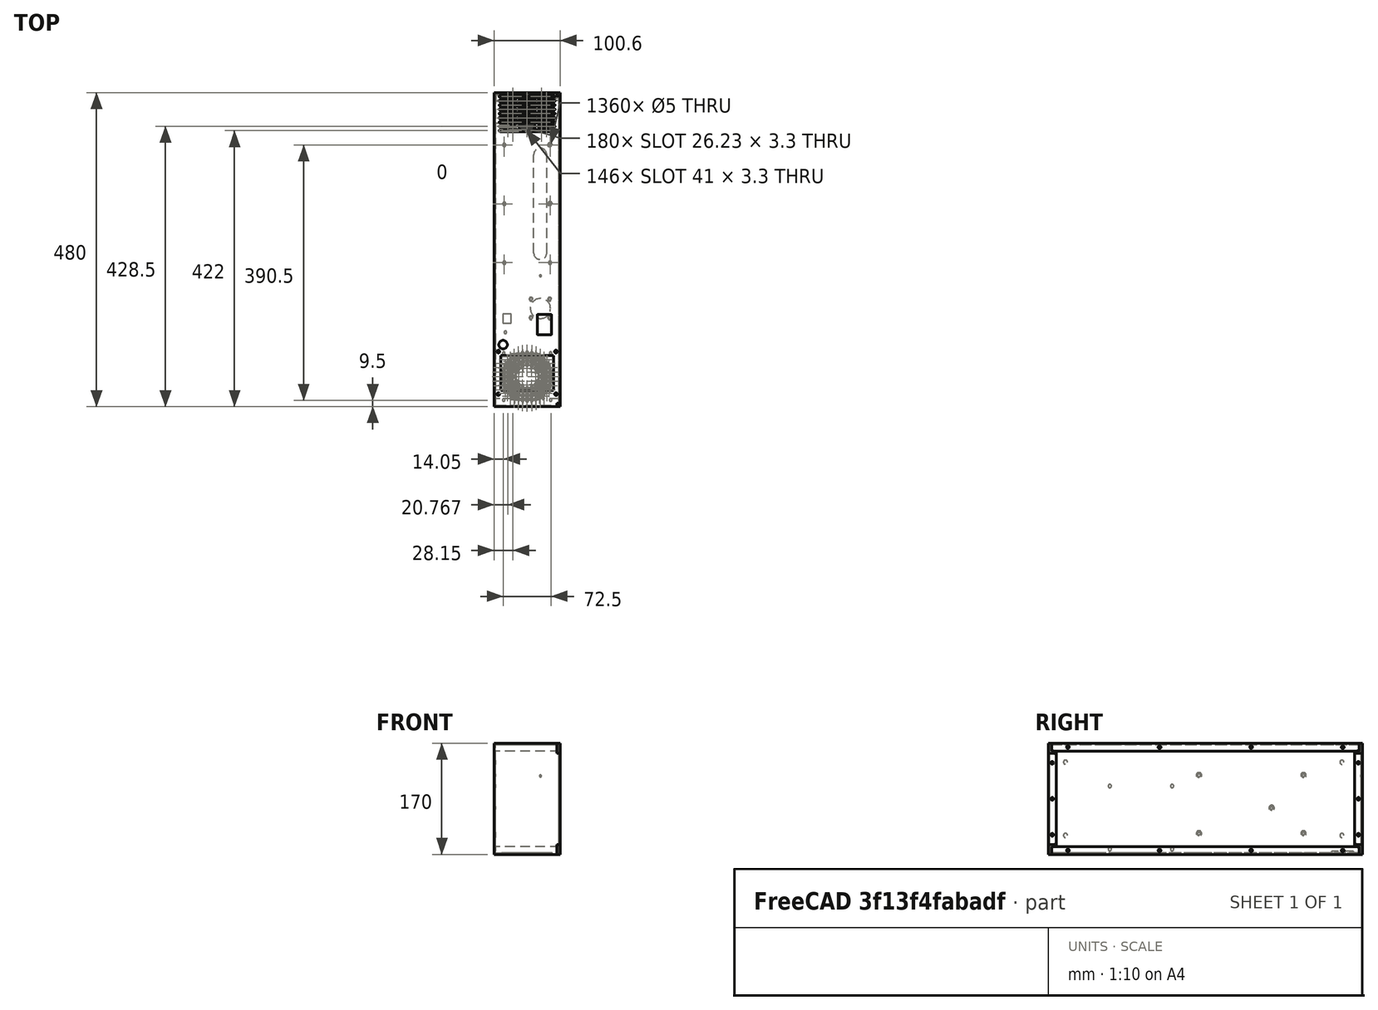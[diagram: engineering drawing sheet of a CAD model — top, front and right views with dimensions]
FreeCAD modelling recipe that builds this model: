
FCSTD DOCUMENT  (FreeCAD 0.17R13123 (Git))
Label: electronics_chassis_PP-FP0142_RevA
License: All rights reserved
LicenseURL: http://en.wikipedia.org/wiki/All_rights_reserved
objects: Drawing::FeatureView×251, Drawing::FeatureViewPython×31, Sketcher::SketchObject×21, PartDesign::Pocket×19, Drawing::FeatureViewPart×15, Drawing::FeaturePage×8, Drawing::FeatureViewSymbol×7, PartDesign::Fillet×4, PartDesign::Pad×2, PartDesign::Chamfer×2, Part::Feature×1
note: 70 computed .brp shape members not serialized (recipe doc carries the construction recipe); baked Part::Feature solids carry a one-line shape summary decoded from their .brp

FEATURE [Sketcher::SketchObject] Sketch
  MapMode = 5
  sketch-geometry (4):
    g0: LineSegment StartX=0 StartY=0 StartZ=0 EndX=-100.6 EndY=0 EndZ=0
    g1: LineSegment StartX=-100.6 StartY=0 StartZ=0 EndX=-100.6 EndY=480 EndZ=0
    g2: LineSegment StartX=-100.6 StartY=480 StartZ=0 EndX=0 EndY=480 EndZ=0
    g3: LineSegment StartX=0 StartY=480 StartZ=0 EndX=0 EndY=0 EndZ=0
  constraints (11):
    c: Coincident(g0,g1)
    c: Coincident(g1,g2)
    c: Coincident(g2,g3)
    c: Coincident(g3,g0)
    c: Horizontal(g0)
    c: Horizontal(g2)
    c: Vertical(g1)
    c: Vertical(g3)
    c: Coincident(g0,g-1)
    c: DistanceX(g0) = -100.6
    c: DistanceY(g3) = -480
FEATURE [PartDesign::Pad] Pad
  Length = 170
  Length2 = 100
  Profile = -> Sketch
  Type = 0
FEATURE [Sketcher::SketchObject] Sketch001
  ExternalGeometry = -> [Pad]
  MapMode = 5
  Placement = pos=(0,0,0) rot=(0.57735,0.57735,0.57735;2.0944rad)
  Support = -> [Pad]
  sketch-geometry (4):
    g0: LineSegment StartX=12 StartY=12 StartZ=0 EndX=468 EndY=12 EndZ=0
    g1: LineSegment StartX=468 StartY=12 StartZ=0 EndX=468 EndY=158 EndZ=0
    g2: LineSegment StartX=468 StartY=158 StartZ=0 EndX=12 EndY=158 EndZ=0
    g3: LineSegment StartX=12 StartY=158 StartZ=0 EndX=12 EndY=12 EndZ=0
  constraints (12):
    c: Coincident(g0,g1)
    c: Coincident(g0,g3)
    c: Coincident(g1,g2)
    c: Coincident(g2,g3)
    c: Horizontal(g0)
    c: Horizontal(g2)
    c: Vertical(g3)
    c: Vertical(g1)
    c: DistanceY(g-1,g0) = 12
    c: DistanceX(g-1,g0) = 12
    c: DistanceX(g0,g-5) = 12
    c: DistanceY(g-4,g2) = -12
FEATURE [PartDesign::Pocket] Pocket
  Length = 98.56
  Profile = -> Sketch001
  Type = 0
FEATURE [Sketcher::SketchObject] Sketch031
  ExternalGeometry = -> [Pocket]
  MapMode = 5
  Placement = pos=(-98.56,0,0) rot=(0.57735,0.57735,0.57735;2.0944rad)
  Support = -> [Pocket]
  sketch-geometry (4):
    g0: LineSegment StartX=2.03 StartY=167.97 StartZ=0 EndX=477.97 EndY=167.97 EndZ=0
    g1: LineSegment StartX=477.97 StartY=167.97 StartZ=0 EndX=477.97 EndY=2.03 EndZ=0
    g2: LineSegment StartX=477.97 StartY=2.03 StartZ=0 EndX=2.03 EndY=2.03 EndZ=0
    g3: LineSegment StartX=2.03 StartY=2.03 StartZ=0 EndX=2.03 EndY=167.97 EndZ=0
  constraints (12):
    c: Coincident(g0,g1)
    c: Coincident(g1,g2)
    c: Coincident(g2,g3)
    c: Coincident(g3,g0)
    c: Horizontal(g0)
    c: Horizontal(g2)
    c: Vertical(g1)
    c: Vertical(g3)
    c: DistanceX(g-1,g2) = 2.03
    c: DistanceY(g-1,g2) = 2.03
    c: DistanceY(g0,g-4) = 2.03
    c: DistanceX(g0,g-4) = 2.03
FEATURE [PartDesign::Pocket] Pocket001
  Length = 96.54
  Profile = -> Sketch031
  Reversed = true
  Type = 0
FEATURE [Sketcher::SketchObject] Sketch032
  ExternalGeometry = -> [Pocket001]
  MapMode = 5
  Placement = pos=(0,0,0) rot=(0.57735,0.57735,0.57735;2.0944rad)
  Support = -> [Pocket001]
  sketch-geometry (24):
    g0: LineSegment StartX=12 StartY=158 StartZ=0 EndX=5 EndY=158 EndZ=0
    g1: LineSegment StartX=5 StartY=158 StartZ=0 EndX=5 EndY=170 EndZ=0
    g2: LineSegment StartX=5 StartY=170 StartZ=0 EndX=0 EndY=170 EndZ=0
    g3: LineSegment StartX=0 StartY=170 StartZ=0 EndX=0 EndY=155 EndZ=0
    g4: LineSegment StartX=0 StartY=155 StartZ=0 EndX=12 EndY=155 EndZ=0
    g5: LineSegment StartX=12 StartY=155 StartZ=0 EndX=12 EndY=158 EndZ=0
    g6: LineSegment StartX=0 StartY=0 StartZ=0 EndX=0 EndY=15 EndZ=0
    g7: LineSegment StartX=0 StartY=15 StartZ=0 EndX=12 EndY=15 EndZ=0
    g8: LineSegment StartX=12 StartY=15 StartZ=0 EndX=12 EndY=12 EndZ=0
    g9: LineSegment StartX=12 StartY=12 StartZ=0 EndX=5 EndY=12 EndZ=0
    g10: LineSegment StartX=5 StartY=12 StartZ=0 EndX=5 EndY=0 EndZ=0
    g11: LineSegment StartX=5 StartY=0 StartZ=0 EndX=0 EndY=0 EndZ=0
    g12: LineSegment StartX=480 StartY=0 StartZ=0 EndX=480 EndY=15 EndZ=0
    g13: LineSegment StartX=480 StartY=15 StartZ=0 EndX=468 EndY=15 EndZ=0
    g14: LineSegment StartX=468 StartY=15 StartZ=0 EndX=468 EndY=12 EndZ=0
    g15: LineSegment StartX=468 StartY=12 StartZ=0 EndX=475 EndY=12 EndZ=0
    g16: LineSegment StartX=475 StartY=12 StartZ=0 EndX=475 EndY=0 EndZ=0
    g17: LineSegment StartX=480 StartY=0 StartZ=0 EndX=475 EndY=0 EndZ=0
    g18: LineSegment StartX=475 StartY=170 StartZ=0 EndX=480 EndY=170 EndZ=0
    g19: LineSegment StartX=480 StartY=170 StartZ=0 EndX=480 EndY=155 EndZ=0
    g20: LineSegment StartX=480 StartY=155 StartZ=0 EndX=468 EndY=155 EndZ=0
    g21: LineSegment StartX=468 StartY=155 StartZ=0 EndX=468 EndY=158 EndZ=0
    g22: LineSegment StartX=468 StartY=158 StartZ=0 EndX=475 EndY=158 EndZ=0
    g23: LineSegment StartX=475 StartY=158 StartZ=0 EndX=475 EndY=170 EndZ=0
  constraints (67):
    c: Coincident(g0,g1)
    c: Coincident(g1,g2)
    c: Coincident(g2,g3)
    c: Coincident(g3,g4)
    c: Coincident(g4,g5)
    c: Coincident(g6,g7)
    c: Coincident(g8,g9)
    c: Coincident(g9,g10)
    c: Coincident(g10,g11)
    c: Coincident(g12,g13)
    c: Coincident(g13,g14)
    c: Coincident(g14,g15)
    c: Coincident(g15,g16)
    c: Coincident(g18,g19)
    c: Coincident(g19,g20)
    c: Coincident(g20,g21)
    c: Coincident(g21,g22)
    c: Coincident(g22,g23)
    c: Vertical(g10)
    c: Vertical(g6)
    c: Vertical(g8)
    c: Horizontal(g7)
    c: Horizontal(g9)
    c: Horizontal(g11)
    c: Coincident(g6,g11)
    c: Distance(g6) = 15
    c: DistanceX(g11) = -5
    c: Coincident(g6,g-1)
    c: PointOnObject(g8,g-8)
    c: Coincident(g7,g8)
    c: Coincident(g8,g-8)
    c: Vertical(g3)
    c: Vertical(g1)
    c: Vertical(g5)
    c: Horizontal(g2)
    c: Horizontal(g0)
    c: Horizontal(g4)
    c: Coincident(g2,g-4)
    c: DistanceX(g1,g2) = -5
    c: DistanceY(g3,g2) = 15
    c: Coincident(g0,g5)
    c: PointOnObject(g0,g-5)
    c: Coincident(g0,g-6)
    c: Vertical(g23)
    c: Vertical(g21)
    c: Vertical(g19)
    c: Horizontal(g18)
    c: Horizontal(g22)
    c: Horizontal(g20)
    c: Coincident(g18,g23)
    c: DistanceY(g19) = -15
    c: DistanceX(g18) = 5
    c: Coincident(g18,g-10)
    c: Coincident(g21,g-9)
    c: Coincident(g12,g17)
    c: Horizontal(g13)
    c: Horizontal(g15)
    c: Horizontal(g17)
    c: Vertical(g14)
    c: Vertical(g16)
    c: Vertical(g12)
    c: Coincident(g16,g17)
    c: DistanceY(g12) = 15
    c: Coincident(g-10,g12)
    c: DistanceX(g16,g12) = 5
    c: PointOnObject(g-9,g15)
    c: Coincident(g14,g-9)
FEATURE [PartDesign::Pocket] Pocket002
  Length = 5
  Profile = -> Sketch032
  Type = 0
FEATURE [Sketcher::SketchObject] Sketch004  label="lcd"
  ExternalGeometry = -> [Pocket]
  MapMode = 5
  Placement = pos=(0,0,170) rot=(0,0,1;0rad)
  Support = -> [Pocket002]
  sketch-geometry (13):
    g0: LineSegment StartX=-90.6 StartY=25 StartZ=0 EndX=-10 EndY=25 EndZ=0
    g1: LineSegment StartX=-10 StartY=25 StartZ=0 EndX=-10 EndY=78.1 EndZ=0
    g2: LineSegment StartX=-10 StartY=78.1 StartZ=0 EndX=-90.6 EndY=78.1 EndZ=0
    g3: LineSegment StartX=-90.6 StartY=78.1 StartZ=0 EndX=-90.6 EndY=25 EndZ=0
    g4: Circle CenterX=-87.1 CenterY=94.75 CenterZ=0 NormalX=0 NormalY=0 NormalZ=1 AngleXU=0 Radius=6.5
    g5: LineSegment [constr] StartX=-94.3 StartY=84.05 StartZ=0 EndX=-6.3 EndY=84.05 EndZ=0
    g6: LineSegment [constr] StartX=-6.3 StartY=84.05 StartZ=0 EndX=-6.3 EndY=19.05 EndZ=0
    g7: LineSegment [constr] StartX=-6.3 StartY=19.05 StartZ=0 EndX=-94.3 EndY=19.05 EndZ=0
    g8: LineSegment [constr] StartX=-94.3 StartY=19.05 StartZ=0 EndX=-94.3 EndY=84.05 EndZ=0
    g9: Circle CenterX=-6.3 CenterY=84.05 CenterZ=0 NormalX=0 NormalY=0 NormalZ=1 AngleXU=0 Radius=2.11
    g10: Circle CenterX=-6.3 CenterY=19.05 CenterZ=0 NormalX=0 NormalY=0 NormalZ=1 AngleXU=0 Radius=2.11
    g11: Circle CenterX=-94.3 CenterY=19.05 CenterZ=0 NormalX=0 NormalY=0 NormalZ=1 AngleXU=0 Radius=2.11
    g12: Circle CenterX=-94.3 CenterY=84.05 CenterZ=0 NormalX=0 NormalY=0 NormalZ=1 AngleXU=0 Radius=2.11
  constraints (35):
    c: Coincident(g0,g1)
    c: Coincident(g0,g3)
    c: Coincident(g1,g2)
    c: Coincident(g2,g3)
    c: DistanceX(g-1,g1) = -10
    c: Distance(g0) = 80.6
    c: Vertical(g1)
    c: Vertical(g3)
    c: Horizontal(g0)
    c: Horizontal(g2)
    c: Distance(g3) = 53.1
    c: DistanceY(g2,g4) = 16.65
    c: Radius(g4) = 6.5
    c: DistanceY(g-1,g0) = 25
    c: DistanceX(g2,g4) = 3.5
    c: Coincident(g5,g6)
    c: Coincident(g6,g7)
    c: Coincident(g7,g8)
    c: Coincident(g8,g5)
    c: Horizontal(g5)
    c: Horizontal(g7)
    c: Vertical(g6)
    c: Vertical(g8)
    c: DistanceY(g8) = 65
    c: DistanceX(g7) = -88
    c: DistanceX(g6,g0) = -3.7
    c: DistanceY(g0,g6) = -5.95
    c: Coincident(g5,g9)
    c: Coincident(g6,g10)
    c: Coincident(g5,g12)
    c: Coincident(g7,g11)
    c: Radius(g9) = 2.11
    c: Equal(g9,g10)
    c: Equal(g10,g11)
    c: Equal(g11,g12)
FEATURE [PartDesign::Pocket] Pocket003  label="lcd-panel"
  Length = 5
  Profile = -> Sketch004
  Type = 0
FEATURE [Sketcher::SketchObject] Sketch015  label="intake"
  MapMode = 5
  Placement = pos=(0,0,170) rot=(0,0,1;0rad)
  Support = -> [Pocket003]
  sketch-geometry (99):
    g0: LineSegment [constr] StartX=-91.3 StartY=474 StartZ=0 EndX=-9.3 EndY=474 EndZ=0
    g1: LineSegment [constr] StartX=-9.3 StartY=474 StartZ=0 EndX=-9.3 EndY=422 EndZ=0
    g2: LineSegment [constr] StartX=-9.3 StartY=422 StartZ=0 EndX=-91.3 EndY=422 EndZ=0
    g3: LineSegment [constr] StartX=-91.3 StartY=422 StartZ=0 EndX=-91.3 EndY=474 EndZ=0
    g4: ArcOfCircle CenterX=-9.3 CenterY=422 CenterZ=0 NormalX=0 NormalY=0 NormalZ=1 AngleXU=0 Radius=1.65 StartAngle=4.71239 EndAngle=7.85398
    g5: ArcOfCircle CenterX=-47 CenterY=422 CenterZ=0 NormalX=0 NormalY=0 NormalZ=1 AngleXU=0 Radius=1.65 StartAngle=1.5708 EndAngle=4.71239
    g6: LineSegment StartX=-9.3 StartY=423.65 StartZ=0 EndX=-47 EndY=423.65 EndZ=0
    g7: LineSegment StartX=-9.3 StartY=420.35 StartZ=0 EndX=-47 EndY=420.35 EndZ=0
    g8: ArcOfCircle CenterX=-91.3 CenterY=422 CenterZ=0 NormalX=0 NormalY=0 NormalZ=1 AngleXU=0 Radius=1.65 StartAngle=1.5708 EndAngle=4.71239
    g9: ArcOfCircle CenterX=-53.6 CenterY=422 CenterZ=0 NormalX=0 NormalY=0 NormalZ=1 AngleXU=0 Radius=1.65 StartAngle=4.71239 EndAngle=7.85398
    g10: LineSegment StartX=-91.3 StartY=420.35 StartZ=0 EndX=-53.6 EndY=420.35 EndZ=0
    g11: LineSegment StartX=-91.3 StartY=423.65 StartZ=0 EndX=-53.6 EndY=423.65 EndZ=0
    g12: ArcOfCircle CenterX=-91.3 CenterY=428.5 CenterZ=0 NormalX=0 NormalY=0 NormalZ=1 AngleXU=0 Radius=1.65 StartAngle=1.5708 EndAngle=4.71239
    g13: ArcOfCircle CenterX=-68.3667 CenterY=428.5 CenterZ=0 NormalX=0 NormalY=0 NormalZ=1 AngleXU=0 Radius=1.65 StartAngle=4.71239 EndAngle=7.85398
    g14: LineSegment StartX=-91.3 StartY=426.85 StartZ=0 EndX=-68.3667 EndY=426.85 EndZ=0
    g15: LineSegment StartX=-91.3 StartY=430.15 StartZ=0 EndX=-68.3667 EndY=430.15 EndZ=0
    g16: ArcOfCircle CenterX=-61.7667 CenterY=428.5 CenterZ=0 NormalX=0 NormalY=0 NormalZ=1 AngleXU=0 Radius=1.65 StartAngle=1.5708 EndAngle=4.71239
    g17: ArcOfCircle CenterX=-38.8333 CenterY=428.5 CenterZ=0 NormalX=0 NormalY=0 NormalZ=1 AngleXU=0 Radius=1.65 StartAngle=4.71239 EndAngle=7.85398
    g18: LineSegment StartX=-61.7667 StartY=426.85 StartZ=0 EndX=-38.8333 EndY=426.85 EndZ=0
    g19: LineSegment StartX=-61.7667 StartY=430.15 StartZ=0 EndX=-38.8333 EndY=430.15 EndZ=0
    g20: ArcOfCircle CenterX=-32.2333 CenterY=428.5 CenterZ=0 NormalX=0 NormalY=0 NormalZ=1 AngleXU=0 Radius=1.65 StartAngle=1.5708 EndAngle=4.71239
    g21: ArcOfCircle CenterX=-9.3 CenterY=428.5 CenterZ=0 NormalX=0 NormalY=0 NormalZ=1 AngleXU=0 Radius=1.65 StartAngle=4.71239 EndAngle=7.85398
    g22: LineSegment StartX=-32.2333 StartY=426.85 StartZ=0 EndX=-9.3 EndY=426.85 EndZ=0
    g23: LineSegment StartX=-32.2333 StartY=430.15 StartZ=0 EndX=-9.3 EndY=430.15 EndZ=0
    g24: ArcOfCircle CenterX=-91.3 CenterY=435 CenterZ=0 NormalX=0 NormalY=0 NormalZ=1 AngleXU=0 Radius=1.65 StartAngle=1.5708 EndAngle=4.71239
    g25: ArcOfCircle CenterX=-53.6 CenterY=435 CenterZ=0 NormalX=0 NormalY=0 NormalZ=1 AngleXU=0 Radius=1.65 StartAngle=4.71239 EndAngle=7.85398
    g26: LineSegment StartX=-91.3 StartY=433.35 StartZ=0 EndX=-53.6 EndY=433.35 EndZ=0
    g27: LineSegment StartX=-91.3 StartY=436.65 StartZ=0 EndX=-53.6 EndY=436.65 EndZ=0
    g28: ArcOfCircle CenterX=-47 CenterY=435 CenterZ=0 NormalX=0 NormalY=0 NormalZ=1 AngleXU=0 Radius=1.65 StartAngle=1.5708 EndAngle=4.71239
    g29: ArcOfCircle CenterX=-9.3 CenterY=435 CenterZ=0 NormalX=0 NormalY=0 NormalZ=1 AngleXU=0 Radius=1.65 StartAngle=4.71239 EndAngle=7.85398
    g30: LineSegment StartX=-47 StartY=433.35 StartZ=0 EndX=-9.3 EndY=433.35 EndZ=0
    g31: LineSegment StartX=-47 StartY=436.65 StartZ=0 EndX=-9.3 EndY=436.65 EndZ=0
    g32: ArcOfCircle CenterX=-91.3 CenterY=441.5 CenterZ=0 NormalX=0 NormalY=0 NormalZ=1 AngleXU=0 Radius=1.65 StartAngle=1.5708 EndAngle=4.71239
    g33: ArcOfCircle CenterX=-68.3667 CenterY=441.5 CenterZ=0 NormalX=0 NormalY=0 NormalZ=1 AngleXU=0 Radius=1.65 StartAngle=4.71239 EndAngle=7.85398
    g34: LineSegment StartX=-91.3 StartY=439.85 StartZ=0 EndX=-68.3667 EndY=439.85 EndZ=0
    g35: LineSegment StartX=-91.3 StartY=443.15 StartZ=0 EndX=-68.3667 EndY=443.15 EndZ=0
    g36: ArcOfCircle CenterX=-61.7667 CenterY=441.5 CenterZ=0 NormalX=0 NormalY=0 NormalZ=1 AngleXU=0 Radius=1.65 StartAngle=1.5708 EndAngle=4.71239
    g37: ArcOfCircle CenterX=-38.8333 CenterY=441.5 CenterZ=0 NormalX=0 NormalY=0 NormalZ=1 AngleXU=0 Radius=1.65 StartAngle=4.71239 EndAngle=7.85398
    g38: LineSegment StartX=-61.7667 StartY=439.85 StartZ=0 EndX=-38.8333 EndY=439.85 EndZ=0
    g39: LineSegment StartX=-61.7667 StartY=443.15 StartZ=0 EndX=-38.8333 EndY=443.15 EndZ=0
    g40: ArcOfCircle CenterX=-32.2333 CenterY=441.5 CenterZ=0 NormalX=0 NormalY=0 NormalZ=1 AngleXU=0 Radius=1.65 StartAngle=1.5708 EndAngle=4.71239
    g41: ArcOfCircle CenterX=-9.3 CenterY=441.5 CenterZ=0 NormalX=0 NormalY=0 NormalZ=1 AngleXU=0 Radius=1.65 StartAngle=4.71239 EndAngle=7.85398
    g42: LineSegment StartX=-32.2333 StartY=439.85 StartZ=0 EndX=-9.3 EndY=439.85 EndZ=0
    g43: LineSegment StartX=-32.2333 StartY=443.15 StartZ=0 EndX=-9.3 EndY=443.15 EndZ=0
    g44: ArcOfCircle CenterX=-91.3 CenterY=448 CenterZ=0 NormalX=0 NormalY=0 NormalZ=1 AngleXU=0 Radius=1.65 StartAngle=1.5708 EndAngle=4.71239
    g45: ArcOfCircle CenterX=-53.6 CenterY=448 CenterZ=0 NormalX=0 NormalY=0 NormalZ=1 AngleXU=0 Radius=1.65 StartAngle=4.71239 EndAngle=7.85398
    g46: LineSegment StartX=-91.3 StartY=446.35 StartZ=0 EndX=-53.6 EndY=446.35 EndZ=0
    g47: LineSegment StartX=-91.3 StartY=449.65 StartZ=0 EndX=-53.6 EndY=449.65 EndZ=0
    g48: ArcOfCircle CenterX=-47 CenterY=448 CenterZ=0 NormalX=0 NormalY=0 NormalZ=1 AngleXU=0 Radius=1.65 StartAngle=1.5708 EndAngle=4.71239
    g49: ArcOfCircle CenterX=-9.3 CenterY=448 CenterZ=0 NormalX=0 NormalY=0 NormalZ=1 AngleXU=0 Radius=1.65 StartAngle=4.71239 EndAngle=7.85398
    g50: LineSegment StartX=-47 StartY=446.35 StartZ=0 EndX=-9.3 EndY=446.35 EndZ=0
    g51: LineSegment StartX=-47 StartY=449.65 StartZ=0 EndX=-9.3 EndY=449.65 EndZ=0
    g52: ArcOfCircle CenterX=-91.3 CenterY=454.5 CenterZ=0 NormalX=0 NormalY=0 NormalZ=1 AngleXU=0 Radius=1.65 StartAngle=1.5708 EndAngle=4.71239
    g53: ArcOfCircle CenterX=-68.3667 CenterY=454.5 CenterZ=0 NormalX=0 NormalY=0 NormalZ=1 AngleXU=0 Radius=1.65 StartAngle=4.71239 EndAngle=7.85398
    g54: LineSegment StartX=-91.3 StartY=452.85 StartZ=0 EndX=-68.3667 EndY=452.85 EndZ=0
    g55: LineSegment StartX=-91.3 StartY=456.15 StartZ=0 EndX=-68.3667 EndY=456.15 EndZ=0
    g56: ArcOfCircle CenterX=-61.7667 CenterY=454.5 CenterZ=0 NormalX=0 NormalY=0 NormalZ=1 AngleXU=0 Radius=1.65 StartAngle=1.5708 EndAngle=4.71239
    g57: ArcOfCircle CenterX=-38.8333 CenterY=454.5 CenterZ=0 NormalX=0 NormalY=0 NormalZ=1 AngleXU=0 Radius=1.65 StartAngle=4.71239 EndAngle=7.85398
    g58: LineSegment StartX=-61.7667 StartY=452.85 StartZ=0 EndX=-38.8333 EndY=452.85 EndZ=0
    g59: LineSegment StartX=-61.7667 StartY=456.15 StartZ=0 EndX=-38.8333 EndY=456.15 EndZ=0
    g60: ArcOfCircle CenterX=-32.2333 CenterY=454.5 CenterZ=0 NormalX=0 NormalY=0 NormalZ=1 AngleXU=0 Radius=1.65 StartAngle=1.5708 EndAngle=4.71239
    g61: ArcOfCircle CenterX=-9.3 CenterY=454.5 CenterZ=0 NormalX=0 NormalY=0 NormalZ=1 AngleXU=0 Radius=1.65 StartAngle=4.71239 EndAngle=7.85398
    g62: LineSegment StartX=-32.2333 StartY=452.85 StartZ=0 EndX=-9.3 EndY=452.85 EndZ=0
    g63: LineSegment StartX=-32.2333 StartY=456.15 StartZ=0 EndX=-9.3 EndY=456.15 EndZ=0
    g64: ArcOfCircle CenterX=-91.3 CenterY=461 CenterZ=0 NormalX=0 NormalY=0 NormalZ=1 AngleXU=0 Radius=1.65 StartAngle=1.5708 EndAngle=4.71239
    g65: ArcOfCircle CenterX=-53.6 CenterY=461 CenterZ=0 NormalX=0 NormalY=0 NormalZ=1 AngleXU=0 Radius=1.65 StartAngle=4.71239 EndAngle=7.85398
    g66: LineSegment StartX=-91.3 StartY=459.35 StartZ=0 EndX=-53.6 EndY=459.35 EndZ=0
    g67: LineSegment StartX=-91.3 StartY=462.65 StartZ=0 EndX=-53.6 EndY=462.65 EndZ=0
    g68: ArcOfCircle CenterX=-47 CenterY=461 CenterZ=0 NormalX=0 NormalY=0 NormalZ=1 AngleXU=0 Radius=1.65 StartAngle=1.5708 EndAngle=4.71239
    g69: ArcOfCircle CenterX=-9.3 CenterY=461 CenterZ=0 NormalX=0 NormalY=0 NormalZ=1 AngleXU=0 Radius=1.65 StartAngle=4.71239 EndAngle=7.85398
    g70: LineSegment StartX=-47 StartY=459.35 StartZ=0 EndX=-9.3 EndY=459.35 EndZ=0
    g71: LineSegment StartX=-47 StartY=462.65 StartZ=0 EndX=-9.3 EndY=462.65 EndZ=0
    g72: ArcOfCircle CenterX=-91.3 CenterY=467.5 CenterZ=0 NormalX=0 NormalY=0 NormalZ=1 AngleXU=0 Radius=1.65 StartAngle=1.5708 EndAngle=4.71239
    g73: ArcOfCircle CenterX=-68.3667 CenterY=467.5 CenterZ=0 NormalX=0 NormalY=0 NormalZ=1 AngleXU=0 Radius=1.65 StartAngle=4.71239 EndAngle=7.85398
    g74: LineSegment StartX=-91.3 StartY=465.85 StartZ=0 EndX=-68.3667 EndY=465.85 EndZ=0
    g75: LineSegment StartX=-91.3 StartY=469.15 StartZ=0 EndX=-68.3667 EndY=469.15 EndZ=0
    g76: ArcOfCircle CenterX=-61.7667 CenterY=467.5 CenterZ=0 NormalX=0 NormalY=0 NormalZ=1 AngleXU=0 Radius=1.65 StartAngle=1.5708 EndAngle=4.71239
    g77: ArcOfCircle CenterX=-38.8333 CenterY=467.5 CenterZ=0 NormalX=0 NormalY=0 NormalZ=1 AngleXU=0 Radius=1.65 StartAngle=4.71239 EndAngle=7.85398
    g78: LineSegment StartX=-61.7667 StartY=465.85 StartZ=0 EndX=-38.8333 EndY=465.85 EndZ=0
    g79: LineSegment StartX=-61.7667 StartY=469.15 StartZ=0 EndX=-38.8333 EndY=469.15 EndZ=0
    g80: ArcOfCircle CenterX=-32.2333 CenterY=467.5 CenterZ=0 NormalX=0 NormalY=0 NormalZ=1 AngleXU=0 Radius=1.65 StartAngle=1.5708 EndAngle=4.71239
    g81: ArcOfCircle CenterX=-9.3 CenterY=467.5 CenterZ=0 NormalX=0 NormalY=0 NormalZ=1 AngleXU=0 Radius=1.65 StartAngle=4.71239 EndAngle=7.85398
    g82: LineSegment StartX=-32.2333 StartY=465.85 StartZ=0 EndX=-9.3 EndY=465.85 EndZ=0
    g83: LineSegment StartX=-32.2333 StartY=469.15 StartZ=0 EndX=-9.3 EndY=469.15 EndZ=0
    g84: ArcOfCircle CenterX=-91.3 CenterY=474 CenterZ=0 NormalX=0 NormalY=0 NormalZ=1 AngleXU=0 Radius=1.65 StartAngle=1.5708 EndAngle=4.71239
    g85: ArcOfCircle CenterX=-53.6 CenterY=474 CenterZ=0 NormalX=0 NormalY=0 NormalZ=1 AngleXU=0 Radius=1.65 StartAngle=4.71239 EndAngle=7.85398
    g86: LineSegment StartX=-91.3 StartY=472.35 StartZ=0 EndX=-53.6 EndY=472.35 EndZ=0
    g87: LineSegment StartX=-91.3 StartY=475.65 StartZ=0 EndX=-53.6 EndY=475.65 EndZ=0
    g88: LineSegment [constr] StartX=-91.3 StartY=435 StartZ=0 EndX=-9.3 EndY=435 EndZ=0
    g89: LineSegment [constr] StartX=-9.3 StartY=448 StartZ=0 EndX=-91.3 EndY=448 EndZ=0
    g90: LineSegment [constr] StartX=-91.3 StartY=441.5 StartZ=0 EndX=-9.3 EndY=441.5 EndZ=0
    g91: LineSegment [constr] StartX=-91.3 StartY=428.5 StartZ=0 EndX=-9.3 EndY=428.5 EndZ=0
    g92: LineSegment [constr] StartX=-91.3 StartY=454.5 StartZ=0 EndX=-9.3 EndY=454.5 EndZ=0
    g93: LineSegment [constr] StartX=-91.3 StartY=461 StartZ=0 EndX=-9.3 EndY=461 EndZ=0
    g94: LineSegment [constr] StartX=-91.3 StartY=467.5 StartZ=0 EndX=-9.3 EndY=467.5 EndZ=0
    g95: ArcOfCircle CenterX=-47 CenterY=474 CenterZ=0 NormalX=0 NormalY=0 NormalZ=1 AngleXU=0 Radius=1.65 StartAngle=1.5708 EndAngle=4.71239
    g96: ArcOfCircle CenterX=-9.3 CenterY=474 CenterZ=0 NormalX=0 NormalY=0 NormalZ=1 AngleXU=0 Radius=1.65 StartAngle=4.71239 EndAngle=7.85398
    g97: LineSegment StartX=-47 StartY=472.35 StartZ=0 EndX=-9.3 EndY=472.35 EndZ=0
    g98: LineSegment StartX=-47 StartY=475.65 StartZ=0 EndX=-9.3 EndY=475.65 EndZ=0
  constraints (243):
    c: Coincident(g1,g2)
    c: Coincident(g2,g3)
    c: Coincident(g3,g0)
    c: Horizontal(g0)
    c: Horizontal(g2)
    c: Vertical(g1)
    c: Vertical(g3)
    c: DistanceX(g2) = -82
    c: DistanceX(g-1,g1) = -9.3
    c: Tangent(g4,g7) = 1.5708
    c: Tangent(g4,g6) = -1.5708
    c: Tangent(g6,g5) = -1.5708
    c: Tangent(g7,g5) = 1.5708
    c: Horizontal(g6)
    c: Equal(g4,g5)
    c: Tangent(g8,g11) = 1.5708
    c: Tangent(g8,g10) = -1.5708
    c: Tangent(g10,g9) = -1.5708
    c: Tangent(g11,g9) = 1.5708
    c: Horizontal(g10)
    c: Equal(g8,g9)
    c: Tangent(g12,g15) = 1.5708
    c: Tangent(g12,g14) = -1.5708
    c: Tangent(g14,g13) = -1.5708
    c: Tangent(g15,g13) = 1.5708
    c: Horizontal(g14)
    c: Equal(g12,g13)
    c: Tangent(g16,g19) = 1.5708
    c: Tangent(g16,g18) = -1.5708
    c: Tangent(g18,g17) = -1.5708
    c: Tangent(g19,g17) = 1.5708
    c: Horizontal(g18)
    c: Equal(g16,g17)
    c: Tangent(g20,g23) = 1.5708
    c: Tangent(g20,g22) = -1.5708
    c: Tangent(g22,g21) = -1.5708
    c: Tangent(g23,g21) = 1.5708
    c: Horizontal(g22)
    c: Equal(g20,g21)
    c: Tangent(g24,g27) = 1.5708
    c: Tangent(g24,g26) = -1.5708
    c: Tangent(g26,g25) = -1.5708
    c: Tangent(g27,g25) = 1.5708
    c: Horizontal(g26)
    c: Equal(g24,g25)
    c: Tangent(g28,g31) = 1.5708
    c: Tangent(g28,g30) = -1.5708
    c: Tangent(g30,g29) = -1.5708
    c: Tangent(g31,g29) = 1.5708
    c: Horizontal(g30)
    c: Equal(g28,g29)
    c: Tangent(g32,g35) = 1.5708
    c: Tangent(g32,g34) = -1.5708
    c: Tangent(g34,g33) = -1.5708
    c: Tangent(g35,g33) = 1.5708
    c: Horizontal(g34)
    c: Equal(g32,g33)
    c: Tangent(g36,g39) = 1.5708
    c: Tangent(g36,g38) = -1.5708
    c: Tangent(g38,g37) = -1.5708
    c: Tangent(g39,g37) = 1.5708
    c: Horizontal(g38)
    c: Equal(g36,g37)
    c: Tangent(g40,g43) = 1.5708
    c: Tangent(g40,g42) = -1.5708
    c: Tangent(g42,g41) = -1.5708
    c: Tangent(g43,g41) = 1.5708
    c: Horizontal(g42)
    c: Equal(g40,g41)
    c: Tangent(g44,g47) = 1.5708
    c: Tangent(g44,g46) = -1.5708
    c: Tangent(g46,g45) = -1.5708
    c: Tangent(g47,g45) = 1.5708
    c: Horizontal(g46)
    c: Equal(g44,g45)
    c: Tangent(g48,g51) = 1.5708
    c: Tangent(g48,g50) = -1.5708
    c: Tangent(g50,g49) = -1.5708
    c: Tangent(g51,g49) = 1.5708
    c: Horizontal(g50)
    c: Equal(g48,g49)
    c: Coincident(g1,g4)
    c: Radius(g4) = 1.65
    c: Coincident(g2,g8)
    c: DistanceX(g5,g9) = -6.6
    c: Tangent(g52,g55) = 1.5708
    c: Tangent(g52,g54) = -1.5708
    c: Tangent(g54,g53) = -1.5708
    c: Tangent(g55,g53) = 1.5708
    c: Horizontal(g54)
    c: Equal(g52,g53)
    c: Tangent(g56,g59) = 1.5708
    c: Tangent(g56,g58) = -1.5708
    c: Tangent(g58,g57) = -1.5708
    c: Tangent(g59,g57) = 1.5708
    c: Horizontal(g58)
    c: Equal(g56,g57)
    c: Tangent(g60,g63) = 1.5708
    c: Tangent(g60,g62) = -1.5708
    c: Tangent(g62,g61) = -1.5708
    c: Tangent(g63,g61) = 1.5708
    c: Horizontal(g62)
    c: Equal(g60,g61)
    c: Tangent(g64,g67) = 1.5708
    c: Tangent(g64,g66) = -1.5708
    c: Tangent(g66,g65) = -1.5708
    c: Tangent(g67,g65) = 1.5708
    c: Horizontal(g66)
    c: Equal(g64,g65)
    c: Tangent(g68,g71) = 1.5708
    c: Tangent(g68,g70) = -1.5708
    c: Tangent(g70,g69) = -1.5708
    c: Tangent(g71,g69) = 1.5708
    c: Horizontal(g70)
    c: Equal(g68,g69)
    c: Tangent(g72,g75) = 1.5708
    c: Tangent(g72,g74) = -1.5708
    c: Tangent(g74,g73) = -1.5708
    c: Tangent(g75,g73) = 1.5708
    c: Horizontal(g74)
    c: Equal(g72,g73)
    c: Tangent(g76,g79) = 1.5708
    c: Tangent(g76,g78) = -1.5708
    c: Tangent(g78,g77) = -1.5708
    c: Tangent(g79,g77) = 1.5708
    c: Horizontal(g78)
    c: Equal(g76,g77)
    c: Tangent(g80,g83) = 1.5708
    c: Tangent(g80,g82) = -1.5708
    c: Tangent(g82,g81) = -1.5708
    c: Tangent(g83,g81) = 1.5708
    c: Horizontal(g82)
    c: Equal(g80,g81)
    c: Tangent(g84,g87) = 1.5708
    c: Tangent(g84,g86) = -1.5708
    c: Tangent(g86,g85) = -1.5708
    c: Tangent(g87,g85) = 1.5708
    c: Horizontal(g86)
    c: Equal(g84,g85)
    c: Horizontal(g94)
    c: Horizontal(g93)
    c: Horizontal(g92)
    c: Horizontal(g89)
    c: Horizontal(g90)
    c: Horizontal(g88)
    c: Horizontal(g91)
    c: PointOnObject(g94,g1)
    c: PointOnObject(g93,g1)
    c: DistanceY(g94,g93) = -6.5
    c: PointOnObject(g92,g1)
    c: DistanceY(g92,g93) = 6.5
    c: PointOnObject(g89,g1)
    c: DistanceY(g89,g92) = 6.5
    c: DistanceY(g94,g0) = 6.5
    c: PointOnObject(g90,g1)
    c: DistanceY(g90,g89) = 6.5
    c: DistanceY(g88,g90) = 6.5
    c: PointOnObject(g88,g1)
    c: PointOnObject(g91,g1)
    c: DistanceY(g91,g88) = 6.5
    c: DistanceY(g1,g91) = 6.5
    c: Equal(g4,g9)
    c: Equal(g9,g21)
    c: Equal(g21,g13)
    c: Equal(g13,g17)
    c: Equal(g17,g25)
    c: Equal(g25,g29)
    c: Equal(g29,g33)
    c: Equal(g33,g37)
    c: Equal(g37,g41)
    c: Equal(g41,g49)
    c: Equal(g49,g45)
    c: Equal(g45,g53)
    c: Equal(g53,g57)
    c: Equal(g57,g61)
    c: Equal(g61,g69)
    c: Equal(g69,g65)
    c: Equal(g65,g81)
    c: Equal(g81,g77)
    c: Equal(g77,g73)
    c: Equal(g73,g85)
    c: PointOnObject(g91,g3)
    c: PointOnObject(g88,g3)
    c: PointOnObject(g90,g3)
    c: PointOnObject(g89,g3)
    c: PointOnObject(g92,g3)
    c: PointOnObject(g93,g3)
    c: PointOnObject(g94,g3)
    c: Coincident(g12,g91)
    c: Coincident(g24,g88)
    c: Coincident(g32,g90)
    c: PointOnObject(g16,g91)
    c: PointOnObject(g20,g91)
    c: DistanceX(g13,g16) = 6.6
    c: Equal(g7,g10)
    c: Equal(g10,g30)
    c: Equal(g30,g26)
    c: Equal(g26,g46)
    c: Equal(g46,g50)
    c: Equal(g50,g66)
    c: Equal(g66,g70)
    c: Equal(g70,g86)
    c: DistanceX(g17,g20) = 6.6
    c: Coincident(g21,g91)
    c: Coincident(g44,g89)
    c: Coincident(g52,g92)
    c: Coincident(g64,g93)
    c: Coincident(g72,g94)
    c: Coincident(g84,g0)
    c: Tangent(g95,g98) = 1.5708
    c: Tangent(g95,g97) = -1.5708
    c: Tangent(g97,g96) = -1.5708
    c: Tangent(g98,g96) = 1.5708
    c: Horizontal(g97)
    c: Equal(g95,g96)
    c: Equal(g4,g96)
    c: Coincident(g0,g1)
    c: Coincident(g0,g96)
    c: Coincident(g81,g94)
    c: Coincident(g69,g93)
    c: Coincident(g61,g92)
    c: Coincident(g49,g89)
    c: Coincident(g41,g90)
    c: Coincident(g29,g88)
    c: Equal(g14,g18)
    c: Equal(g18,g22)
    c: Equal(g22,g39)
    c: Equal(g39,g35)
    c: Equal(g35,g43)
    c: Equal(g43,g62)
    c: Equal(g62,g58)
    c: Equal(g58,g54)
    c: Equal(g54,g74)
    c: Equal(g74,g78)
    c: Equal(g78,g82)
    c: PointOnObject(g36,g90)
    c: PointOnObject(g56,g92)
    c: PointOnObject(g76,g94)
    c: DistanceX(g85,g95) = 6.6
    c: DistanceX(g73,g76) = 6.6
    c: DistanceX(g53,g56) = 6.6
    c: DistanceX(g33,g36) = 6.6
    c: DistanceY(g-1,g1) = 422
FEATURE [PartDesign::Pocket] Pocket004  label="air-inlet"
  Length = 5
  Profile = -> Sketch015
  Type = 0
FEATURE [Sketcher::SketchObject] Sketch014  label="pwr"
  MapMode = 5
  Placement = pos=(0,0,170) rot=(0,0,1;0rad)
  Support = -> [Pocket004]
  sketch-geometry (8):
    g0: LineSegment StartX=-34.5 StartY=140.6 StartZ=0 EndX=-13.5 EndY=140.6 EndZ=0
    g1: LineSegment StartX=-13 StartY=140.1 StartZ=0 EndX=-13 EndY=110.5 EndZ=0
    g2: LineSegment StartX=-13.5 StartY=110 StartZ=0 EndX=-34.5 EndY=110 EndZ=0
    g3: LineSegment StartX=-35 StartY=110.5 StartZ=0 EndX=-35 EndY=140.1 EndZ=0
    g4: ArcOfCircle CenterX=-34.5 CenterY=140.1 CenterZ=0 NormalX=0 NormalY=0 NormalZ=1 AngleXU=0 Radius=0.5 StartAngle=1.5708 EndAngle=3.14159
    g5: ArcOfCircle CenterX=-34.5 CenterY=110.5 CenterZ=0 NormalX=0 NormalY=0 NormalZ=1 AngleXU=0 Radius=0.5 StartAngle=3.14159 EndAngle=4.71239
    g6: ArcOfCircle CenterX=-13.5 CenterY=110.5 CenterZ=0 NormalX=0 NormalY=0 NormalZ=1 AngleXU=0 Radius=0.5 StartAngle=4.71239 EndAngle=6.28319
    g7: ArcOfCircle CenterX=-13.5 CenterY=140.1 CenterZ=0 NormalX=0 NormalY=0 NormalZ=1 AngleXU=0 Radius=0.5 StartAngle=0 EndAngle=1.5708
  constraints (20):
    c: Horizontal(g0)
    c: Horizontal(g2)
    c: Vertical(g1)
    c: Vertical(g3)
    c: Tangent(g0,g4) = 1.5708
    c: Tangent(g3,g4) = 1.5708
    c: Tangent(g3,g5) = 1.5708
    c: Tangent(g2,g5) = 1.5708
    c: Tangent(g2,g6) = 1.5708
    c: Tangent(g1,g6) = 1.5708
    c: Tangent(g1,g7) = 1.5708
    c: Tangent(g0,g7) = 1.5708
    c: Radius(g4) = 0.5
    c: Equal(g4,g7)
    c: Equal(g7,g6)
    c: Equal(g6,g5)
    c: DistanceX(g-1,g1) = -13
    c: DistanceY(g-1,g2) = 110
    c: Distance(g0) = 21
    c: DistanceY(g2,g0) = 30.6
FEATURE [PartDesign::Pocket] Pocket005  label="pwr-switch"
  Length = 5
  Profile = -> Sketch014
  Type = 0
FEATURE [Sketcher::SketchObject] Sketch016  label="exhaust"
  MapMode = 5
  Placement = pos=(0,0,0) rot=(1,0,0;3.14159rad)
  Support = -> [Pocket005]
  sketch-geometry (163):
    g0: LineSegment [constr] StartX=-86.05 StartY=-10 StartZ=0 EndX=-14.55 EndY=-10 EndZ=0
    g1: LineSegment [constr] StartX=-14.55 StartY=-10 StartZ=0 EndX=-14.55 EndY=-81.5 EndZ=0
    g2: LineSegment [constr] StartX=-14.55 StartY=-81.5 StartZ=0 EndX=-86.05 EndY=-81.5 EndZ=0
    g3: LineSegment [constr] StartX=-86.05 StartY=-81.5 StartZ=0 EndX=-86.05 EndY=-10 EndZ=0
    g4: Circle CenterX=-86.05 CenterY=-10 CenterZ=0 NormalX=0 NormalY=0 NormalZ=1 AngleXU=0 Radius=2
    g5: Circle CenterX=-14.55 CenterY=-10 CenterZ=0 NormalX=0 NormalY=0 NormalZ=1 AngleXU=0 Radius=2
    g6: Circle CenterX=-14.55 CenterY=-81.5 CenterZ=0 NormalX=0 NormalY=0 NormalZ=1 AngleXU=0 Radius=2
    g7: Circle CenterX=-86.05 CenterY=-81.5 CenterZ=0 NormalX=0 NormalY=0 NormalZ=1 AngleXU=0 Radius=2
    g8: Circle [constr] CenterX=-50.3 CenterY=-45.75 CenterZ=0 NormalX=0 NormalY=0 NormalZ=1 AngleXU=0 Radius=16
    g9: Circle [constr] CenterX=-50.3 CenterY=-45.75 CenterZ=0 NormalX=0 NormalY=0 NormalZ=1 AngleXU=0 Radius=18.25
    g10: Circle [constr] CenterX=-50.3 CenterY=-45.75 CenterZ=0 NormalX=0 NormalY=0 NormalZ=1 AngleXU=0 Radius=24.25
    g11: Circle [constr] CenterX=-50.3 CenterY=-45.75 CenterZ=0 NormalX=0 NormalY=0 NormalZ=1 AngleXU=0 Radius=30.25
    g12: Circle [constr] CenterX=-50.3 CenterY=-45.75 CenterZ=0 NormalX=0 NormalY=0 NormalZ=1 AngleXU=0 Radius=36.25
    g13: LineSegment [constr] StartX=-50.3 StartY=-9.5 StartZ=0 EndX=-50.3 EndY=-82 EndZ=0
    g14: LineSegment [constr] StartX=-86.55 StartY=-45.75 StartZ=0 EndX=-14.05 EndY=-45.75 EndZ=0
    g15: LineSegment [constr] StartX=-85.8535 StartY=-38.678 StartZ=0 EndX=-14.7465 EndY=-52.822 EndZ=0
    g16: LineSegment [constr] StartX=-83.7906 StartY=-31.8777 StartZ=0 EndX=-16.8094 EndY=-59.6223 EndZ=0
    g17: LineSegment [constr] StartX=-80.4408 StartY=-25.6106 StartZ=0 EndX=-20.1592 EndY=-65.8894 EndZ=0
    g18: LineSegment [constr] StartX=-75.9326 StartY=-20.1174 StartZ=0 EndX=-24.6674 EndY=-71.3826 EndZ=0
    g19: LineSegment [constr] StartX=-70.4394 StartY=-15.6092 StartZ=0 EndX=-30.1606 EndY=-75.8908 EndZ=0
    g20: LineSegment [constr] StartX=-64.1723 StartY=-12.2594 StartZ=0 EndX=-36.4277 EndY=-79.2406 EndZ=0
    g21: LineSegment [constr] StartX=-43.228 StartY=-10.1965 StartZ=0 EndX=-57.372 EndY=-81.3035 EndZ=0
    g22: LineSegment [constr] StartX=-36.4277 StartY=-12.2594 StartZ=0 EndX=-64.1723 EndY=-79.2406 EndZ=0
    g23: LineSegment [constr] StartX=-70.4394 StartY=-75.8908 StartZ=0 EndX=-30.1606 EndY=-15.6092 EndZ=0
    g24: LineSegment [constr] StartX=-24.6674 StartY=-20.1174 StartZ=0 EndX=-75.9326 EndY=-71.3826 EndZ=0
    g25: LineSegment [constr] StartX=-80.4408 StartY=-65.8894 StartZ=0 EndX=-20.1592 EndY=-25.6106 EndZ=0
    g26: LineSegment [constr] StartX=-83.7906 StartY=-59.6223 StartZ=0 EndX=-16.8094 EndY=-31.8777 EndZ=0
    g27: LineSegment [constr] StartX=-14.7465 StartY=-38.678 StartZ=0 EndX=-85.8535 EndY=-52.822 EndZ=0
    g28: LineSegment [constr] StartX=-57.372 StartY=-10.1965 StartZ=0 EndX=-43.228 EndY=-81.3035 EndZ=0
    g29: Circle CenterX=-50.3 CenterY=-9.5 CenterZ=0 NormalX=0 NormalY=0 NormalZ=1 AngleXU=0 Radius=2.5
    g30: Circle CenterX=-43.228 CenterY=-10.1965 CenterZ=0 NormalX=0 NormalY=0 NormalZ=1 AngleXU=0 Radius=2.5
    g31: Circle CenterX=-36.4277 CenterY=-12.2594 CenterZ=0 NormalX=0 NormalY=0 NormalZ=1 AngleXU=0 Radius=2.5
    g32: Circle CenterX=-30.1606 CenterY=-15.6092 CenterZ=0 NormalX=0 NormalY=0 NormalZ=1 AngleXU=0 Radius=2.5
    g33: Circle CenterX=-24.6674 CenterY=-20.1174 CenterZ=0 NormalX=0 NormalY=0 NormalZ=1 AngleXU=0 Radius=2.5
    g34: Circle CenterX=-20.1592 CenterY=-25.6106 CenterZ=0 NormalX=0 NormalY=0 NormalZ=1 AngleXU=0 Radius=2.5
    g35: Circle CenterX=-16.8094 CenterY=-31.8777 CenterZ=0 NormalX=0 NormalY=0 NormalZ=1 AngleXU=0 Radius=2.5
    g36: Circle CenterX=-14.7465 CenterY=-38.678 CenterZ=0 NormalX=0 NormalY=0 NormalZ=1 AngleXU=0 Radius=2.5
    g37: Circle CenterX=-14.05 CenterY=-45.75 CenterZ=0 NormalX=0 NormalY=0 NormalZ=1 AngleXU=0 Radius=2.5
    g38: Circle CenterX=-57.372 CenterY=-10.1965 CenterZ=0 NormalX=0 NormalY=0 NormalZ=1 AngleXU=0 Radius=2.5
    g39: Circle CenterX=-64.1723 CenterY=-12.2594 CenterZ=0 NormalX=0 NormalY=0 NormalZ=1 AngleXU=0 Radius=2.5
    g40: Circle CenterX=-70.4394 CenterY=-15.6092 CenterZ=0 NormalX=0 NormalY=0 NormalZ=1 AngleXU=0 Radius=2.5
    g41: Circle CenterX=-75.9326 CenterY=-20.1174 CenterZ=0 NormalX=0 NormalY=0 NormalZ=1 AngleXU=0 Radius=2.5
    g42: Circle CenterX=-80.4408 CenterY=-25.6106 CenterZ=0 NormalX=0 NormalY=0 NormalZ=1 AngleXU=0 Radius=2.5
    g43: Circle CenterX=-83.7906 CenterY=-31.8777 CenterZ=0 NormalX=0 NormalY=0 NormalZ=1 AngleXU=0 Radius=2.5
    g44: Circle CenterX=-85.8535 CenterY=-38.678 CenterZ=0 NormalX=0 NormalY=0 NormalZ=1 AngleXU=0 Radius=2.5
    g45: Circle CenterX=-86.55 CenterY=-45.75 CenterZ=0 NormalX=0 NormalY=0 NormalZ=1 AngleXU=0 Radius=2.5
    g46: Circle CenterX=-85.8535 CenterY=-52.822 CenterZ=0 NormalX=0 NormalY=0 NormalZ=1 AngleXU=0 Radius=2.5
    g47: Circle CenterX=-83.7906 CenterY=-59.6223 CenterZ=0 NormalX=0 NormalY=0 NormalZ=1 AngleXU=0 Radius=2.5
    g48: Circle CenterX=-80.4408 CenterY=-65.8894 CenterZ=0 NormalX=0 NormalY=0 NormalZ=1 AngleXU=0 Radius=2.5
    g49: Circle CenterX=-75.9326 CenterY=-71.3826 CenterZ=0 NormalX=0 NormalY=0 NormalZ=1 AngleXU=0 Radius=2.5
    g50: Circle CenterX=-70.4394 CenterY=-75.8908 CenterZ=0 NormalX=0 NormalY=0 NormalZ=1 AngleXU=0 Radius=2.5
    g51: Circle CenterX=-64.1723 CenterY=-79.2406 CenterZ=0 NormalX=0 NormalY=0 NormalZ=1 AngleXU=0 Radius=2.5
    g52: Circle CenterX=-57.372 CenterY=-81.3035 CenterZ=0 NormalX=0 NormalY=0 NormalZ=1 AngleXU=0 Radius=2.5
    g53: Circle CenterX=-50.3 CenterY=-82 CenterZ=0 NormalX=0 NormalY=0 NormalZ=1 AngleXU=0 Radius=2.5
    g54: Circle CenterX=-43.228 CenterY=-81.3035 CenterZ=0 NormalX=0 NormalY=0 NormalZ=1 AngleXU=0 Radius=2.5
    g55: Circle CenterX=-36.4277 CenterY=-79.2406 CenterZ=0 NormalX=0 NormalY=0 NormalZ=1 AngleXU=0 Radius=2.5
    g56: Circle CenterX=-30.1606 CenterY=-75.8908 CenterZ=0 NormalX=0 NormalY=0 NormalZ=1 AngleXU=0 Radius=2.5
    g57: Circle CenterX=-24.6674 CenterY=-71.3826 CenterZ=0 NormalX=0 NormalY=0 NormalZ=1 AngleXU=0 Radius=2.5
    g58: Circle CenterX=-20.1592 CenterY=-65.8894 CenterZ=0 NormalX=0 NormalY=0 NormalZ=1 AngleXU=0 Radius=2.5
    g59: Circle CenterX=-16.8094 CenterY=-59.6223 CenterZ=0 NormalX=0 NormalY=0 NormalZ=1 AngleXU=0 Radius=2.5
    g60: Circle CenterX=-14.7465 CenterY=-52.822 CenterZ=0 NormalX=0 NormalY=0 NormalZ=1 AngleXU=0 Radius=2.5
    g61: Circle CenterX=-50.3 CenterY=-15.5 CenterZ=0 NormalX=0 NormalY=0 NormalZ=1 AngleXU=0 Radius=2.5
    g62: Circle CenterX=-20.05 CenterY=-45.75 CenterZ=0 NormalX=0 NormalY=0 NormalZ=1 AngleXU=0 Radius=2.5
    g63: Circle CenterX=-80.55 CenterY=-45.75 CenterZ=0 NormalX=0 NormalY=0 NormalZ=1 AngleXU=0 Radius=2.5
    g64: Circle CenterX=-50.3 CenterY=-76 CenterZ=0 NormalX=0 NormalY=0 NormalZ=1 AngleXU=0 Radius=2.5
    g65: LineSegment [constr] StartX=-37.1595 StartY=-18.5032 StartZ=0 EndX=-63.4405 EndY=-72.9968 EndZ=0
    g66: LineSegment [constr] StartX=-69.1711 StartY=-69.392 StartZ=0 EndX=-31.4289 EndY=-22.108 EndZ=0
    g67: LineSegment [constr] StartX=-57.0518 StartY=-75.2369 StartZ=0 EndX=-43.5482 EndY=-16.2631 EndZ=0
    g68: LineSegment [constr] StartX=-73.9575 StartY=-64.6017 StartZ=0 EndX=-26.6425 EndY=-26.8983 EndZ=0
    g69: LineSegment [constr] StartX=-77.5576 StartY=-58.8682 StartZ=0 EndX=-23.0424 EndY=-32.6318 EndZ=0
    g70: LineSegment [constr] StartX=-20.8076 StartY=-39.0224 StartZ=0 EndX=-79.7924 EndY=-52.4776 EndZ=0
    g71: LineSegment [constr] StartX=-57.0276 StartY=-16.2576 StartZ=0 EndX=-43.5724 EndY=-75.2424 EndZ=0
    g72: LineSegment [constr] StartX=-63.4182 StartY=-18.4924 StartZ=0 EndX=-37.1818 EndY=-73.0076 EndZ=0
    g73: LineSegment [constr] StartX=-69.1517 StartY=-22.0925 StartZ=0 EndX=-31.4483 EndY=-69.4075 EndZ=0
    g74: LineSegment [constr] StartX=-73.941 StartY=-26.8776 StartZ=0 EndX=-26.659 EndY=-64.6224 EndZ=0
    g75: LineSegment [constr] StartX=-77.5461 StartY=-32.608 StartZ=0 EndX=-23.0539 EndY=-58.892 EndZ=0
    g76: LineSegment [constr] StartX=-79.7865 StartY=-38.9967 StartZ=0 EndX=-20.8135 EndY=-52.5033 EndZ=0
    g77: Circle CenterX=-79.7865 CenterY=-38.9967 CenterZ=0 NormalX=0 NormalY=0 NormalZ=1 AngleXU=0 Radius=2.5
    g78: Circle CenterX=-77.5461 CenterY=-32.608 CenterZ=0 NormalX=0 NormalY=0 NormalZ=1 AngleXU=0 Radius=2.5
    g79: Circle CenterX=-73.941 CenterY=-26.8776 CenterZ=0 NormalX=0 NormalY=0 NormalZ=1 AngleXU=0 Radius=2.5
    g80: Circle CenterX=-69.1517 CenterY=-22.0925 CenterZ=0 NormalX=0 NormalY=0 NormalZ=1 AngleXU=0 Radius=2.5
    g81: Circle CenterX=-63.4182 CenterY=-18.4924 CenterZ=0 NormalX=0 NormalY=0 NormalZ=1 AngleXU=0 Radius=2.5
    g82: Circle CenterX=-57.0276 CenterY=-16.2576 CenterZ=0 NormalX=0 NormalY=0 NormalZ=1 AngleXU=0 Radius=2.5
    g83: Circle CenterX=-43.5482 CenterY=-16.2631 CenterZ=0 NormalX=0 NormalY=0 NormalZ=1 AngleXU=0 Radius=2.5
    g84: Circle CenterX=-37.1595 CenterY=-18.5032 CenterZ=0 NormalX=0 NormalY=0 NormalZ=1 AngleXU=0 Radius=2.5
    g85: Circle CenterX=-31.4289 CenterY=-22.108 CenterZ=0 NormalX=0 NormalY=0 NormalZ=1 AngleXU=0 Radius=2.5
    g86: Circle CenterX=-26.6425 CenterY=-26.8983 CenterZ=0 NormalX=0 NormalY=0 NormalZ=1 AngleXU=0 Radius=2.5
    g87: Circle CenterX=-23.0424 CenterY=-32.6318 CenterZ=0 NormalX=0 NormalY=0 NormalZ=1 AngleXU=0 Radius=2.5
    g88: Circle CenterX=-20.8076 CenterY=-39.0224 CenterZ=0 NormalX=0 NormalY=0 NormalZ=1 AngleXU=0 Radius=2.5
    g89: Circle CenterX=-20.8135 CenterY=-52.5033 CenterZ=0 NormalX=0 NormalY=0 NormalZ=1 AngleXU=0 Radius=2.5
    g90: Circle CenterX=-23.0539 CenterY=-58.892 CenterZ=0 NormalX=0 NormalY=0 NormalZ=1 AngleXU=0 Radius=2.5
    g91: Circle CenterX=-26.659 CenterY=-64.6224 CenterZ=0 NormalX=0 NormalY=0 NormalZ=1 AngleXU=0 Radius=2.5
    g92: Circle CenterX=-31.4483 CenterY=-69.4075 CenterZ=0 NormalX=0 NormalY=0 NormalZ=1 AngleXU=0 Radius=2.5
    g93: Circle CenterX=-37.1818 CenterY=-73.0076 CenterZ=0 NormalX=0 NormalY=0 NormalZ=1 AngleXU=0 Radius=2.5
    g94: Circle CenterX=-43.5724 CenterY=-75.2424 CenterZ=0 NormalX=0 NormalY=0 NormalZ=1 AngleXU=0 Radius=2.5
    g95: Circle CenterX=-57.0518 CenterY=-75.2369 CenterZ=0 NormalX=0 NormalY=0 NormalZ=1 AngleXU=0 Radius=2.5
    g96: Circle CenterX=-63.4405 CenterY=-72.9968 CenterZ=0 NormalX=0 NormalY=0 NormalZ=1 AngleXU=0 Radius=2.5
    g97: Circle CenterX=-69.1711 CenterY=-69.392 CenterZ=0 NormalX=0 NormalY=0 NormalZ=1 AngleXU=0 Radius=2.5
    g98: Circle CenterX=-73.9575 CenterY=-64.6017 CenterZ=0 NormalX=0 NormalY=0 NormalZ=1 AngleXU=0 Radius=2.5
    g99: Circle CenterX=-77.5576 CenterY=-58.8682 CenterZ=0 NormalX=0 NormalY=0 NormalZ=1 AngleXU=0 Radius=2.5
    g100: Circle CenterX=-79.7924 CenterY=-52.4776 CenterZ=0 NormalX=0 NormalY=0 NormalZ=1 AngleXU=0 Radius=2.5
    g101: LineSegment [constr] StartX=-33.1527 StartY=-28.6027 StartZ=0 EndX=-67.4473 EndY=-62.8973 EndZ=0
    g102: LineSegment [constr] StartX=-29.2989 StartY=-33.625 StartZ=0 EndX=-71.3011 EndY=-57.875 EndZ=0
    g103: LineSegment [constr] StartX=-26.8763 StartY=-39.4736 StartZ=0 EndX=-73.7237 EndY=-52.0264 EndZ=0
    g104: LineSegment [constr] StartX=-73.7237 StartY=-39.4736 StartZ=0 EndX=-26.8763 EndY=-52.0264 EndZ=0
    g105: LineSegment [constr] StartX=-56.5764 StartY=-22.3263 StartZ=0 EndX=-44.0236 EndY=-69.1737 EndZ=0
    g106: LineSegment [constr] StartX=-62.425 StartY=-24.7489 StartZ=0 EndX=-38.175 EndY=-66.7511 EndZ=0
    g107: LineSegment [constr] StartX=-67.4473 StartY=-28.6027 StartZ=0 EndX=-33.1527 EndY=-62.8973 EndZ=0
    g108: LineSegment [constr] StartX=-71.3011 StartY=-33.625 StartZ=0 EndX=-29.2989 EndY=-57.875 EndZ=0
    g109: Circle CenterX=-44.0236 CenterY=-22.3263 CenterZ=0 NormalX=0 NormalY=0 NormalZ=1 AngleXU=0 Radius=2.5
    g110: Circle CenterX=-38.175 CenterY=-24.7489 CenterZ=0 NormalX=0 NormalY=0 NormalZ=1 AngleXU=0 Radius=2.5
    g111: Circle CenterX=-33.1527 CenterY=-28.6027 CenterZ=0 NormalX=0 NormalY=0 NormalZ=1 AngleXU=0 Radius=2.5
    g112: Circle CenterX=-29.2989 CenterY=-33.625 CenterZ=0 NormalX=0 NormalY=0 NormalZ=1 AngleXU=0 Radius=2.5
    g113: Circle CenterX=-26.8763 CenterY=-39.4736 CenterZ=0 NormalX=0 NormalY=0 NormalZ=1 AngleXU=0 Radius=2.5
    g114: Circle CenterX=-26.05 CenterY=-45.75 CenterZ=0 NormalX=0 NormalY=0 NormalZ=1 AngleXU=0 Radius=2.5
    g115: Circle CenterX=-26.8763 CenterY=-52.0264 CenterZ=0 NormalX=0 NormalY=0 NormalZ=1 AngleXU=0 Radius=2.5
    g116: Circle CenterX=-29.2989 CenterY=-57.875 CenterZ=0 NormalX=0 NormalY=0 NormalZ=1 AngleXU=0 Radius=2.5
    g117: Circle CenterX=-33.1527 CenterY=-62.8973 CenterZ=0 NormalX=0 NormalY=0 NormalZ=1 AngleXU=0 Radius=2.5
    g118: Circle CenterX=-38.175 CenterY=-66.7511 CenterZ=0 NormalX=0 NormalY=0 NormalZ=1 AngleXU=0 Radius=2.5
    g119: Circle CenterX=-44.0236 CenterY=-69.1737 CenterZ=0 NormalX=0 NormalY=0 NormalZ=1 AngleXU=0 Radius=2.5
    g120: Circle CenterX=-50.3 CenterY=-70 CenterZ=0 NormalX=0 NormalY=0 NormalZ=1 AngleXU=0 Radius=2.5
    g121: Circle CenterX=-56.5764 CenterY=-69.1737 CenterZ=0 NormalX=0 NormalY=0 NormalZ=1 AngleXU=0 Radius=2.5
    g122: Circle CenterX=-62.425 CenterY=-66.7511 CenterZ=0 NormalX=0 NormalY=0 NormalZ=1 AngleXU=0 Radius=2.5
    g123: Circle CenterX=-67.4473 CenterY=-62.8973 CenterZ=0 NormalX=0 NormalY=0 NormalZ=1 AngleXU=0 Radius=2.5
    g124: Circle CenterX=-71.3011 CenterY=-57.875 CenterZ=0 NormalX=0 NormalY=0 NormalZ=1 AngleXU=0 Radius=2.5
    g125: Circle CenterX=-73.7237 CenterY=-52.0264 CenterZ=0 NormalX=0 NormalY=0 NormalZ=1 AngleXU=0 Radius=2.5
    g126: Circle CenterX=-73.7237 CenterY=-39.4736 CenterZ=0 NormalX=0 NormalY=0 NormalZ=1 AngleXU=0 Radius=2.5
    g127: Circle CenterX=-74.55 CenterY=-45.75 CenterZ=0 NormalX=0 NormalY=0 NormalZ=1 AngleXU=0 Radius=2.5
    g128: Circle CenterX=-71.3011 CenterY=-33.625 CenterZ=0 NormalX=0 NormalY=0 NormalZ=1 AngleXU=0 Radius=2.5
    g129: Circle CenterX=-67.4473 CenterY=-28.6027 CenterZ=0 NormalX=0 NormalY=0 NormalZ=1 AngleXU=0 Radius=2.5
    g130: Circle CenterX=-62.425 CenterY=-24.7489 CenterZ=0 NormalX=0 NormalY=0 NormalZ=1 AngleXU=0 Radius=2.5
    g131: Circle CenterX=-56.5764 CenterY=-22.3263 CenterZ=0 NormalX=0 NormalY=0 NormalZ=1 AngleXU=0 Radius=2.5
    g132: Circle CenterX=-50.3 CenterY=-21.5 CenterZ=0 NormalX=0 NormalY=0 NormalZ=1 AngleXU=0 Radius=2.5
    g133: LineSegment [constr] StartX=-43.316 StartY=-28.8892 StartZ=0 EndX=-57.284 EndY=-62.6108 EndZ=0
    g134: LineSegment [constr] StartX=-37.3953 StartY=-32.8453 StartZ=0 EndX=-63.2047 EndY=-58.6547 EndZ=0
    g135: LineSegment [constr] StartX=-33.4392 StartY=-38.766 StartZ=0 EndX=-67.1608 EndY=-52.734 EndZ=0
    g136: LineSegment [constr] StartX=-68.55 StartY=-45.75 StartZ=0 EndX=-32.05 EndY=-45.75 EndZ=0
    g137: LineSegment [constr] StartX=-67.1608 StartY=-38.766 StartZ=0 EndX=-33.4392 EndY=-52.734 EndZ=0
    g138: LineSegment [constr] StartX=-63.2047 StartY=-32.8453 StartZ=0 EndX=-37.3953 EndY=-58.6547 EndZ=0
    g139: LineSegment [constr] StartX=-57.284 StartY=-28.8892 StartZ=0 EndX=-43.316 EndY=-62.6108 EndZ=0
    g140: LineSegment [constr] StartX=-50.3 StartY=-27.5 StartZ=0 EndX=-50.3 EndY=-64 EndZ=0
    g141: Circle CenterX=-50.3 CenterY=-27.5 CenterZ=0 NormalX=0 NormalY=0 NormalZ=1 AngleXU=0 Radius=2.5
    g142: Circle CenterX=-43.316 CenterY=-28.8892 CenterZ=0 NormalX=0 NormalY=0 NormalZ=1 AngleXU=0 Radius=2.5
    g143: Circle CenterX=-37.3953 CenterY=-32.8453 CenterZ=0 NormalX=0 NormalY=0 NormalZ=1 AngleXU=0 Radius=2.5
    g144: Circle CenterX=-33.4392 CenterY=-38.766 CenterZ=0 NormalX=0 NormalY=0 NormalZ=1 AngleXU=0 Radius=2.5
    g145: Circle CenterX=-32.05 CenterY=-45.75 CenterZ=0 NormalX=0 NormalY=0 NormalZ=1 AngleXU=0 Radius=2.5
    g146: Circle CenterX=-33.4392 CenterY=-52.734 CenterZ=0 NormalX=0 NormalY=0 NormalZ=1 AngleXU=0 Radius=2.5
    g147: Circle CenterX=-37.3953 CenterY=-58.6547 CenterZ=0 NormalX=0 NormalY=0 NormalZ=1 AngleXU=0 Radius=2.5
    g148: Circle CenterX=-43.316 CenterY=-62.6108 CenterZ=0 NormalX=0 NormalY=0 NormalZ=1 AngleXU=0 Radius=2.5
    g149: Circle CenterX=-50.3 CenterY=-64 CenterZ=0 NormalX=0 NormalY=0 NormalZ=1 AngleXU=0 Radius=2.5
    g150: Circle CenterX=-57.284 CenterY=-62.6108 CenterZ=0 NormalX=0 NormalY=0 NormalZ=1 AngleXU=0 Radius=2.5
    g151: Circle CenterX=-63.2047 CenterY=-58.6547 CenterZ=0 NormalX=0 NormalY=0 NormalZ=1 AngleXU=0 Radius=2.5
    g152: Circle CenterX=-68.55 CenterY=-45.75 CenterZ=0 NormalX=0 NormalY=0 NormalZ=1 AngleXU=0 Radius=2.5
    g153: Circle CenterX=-67.1608 CenterY=-52.734 CenterZ=0 NormalX=0 NormalY=0 NormalZ=1 AngleXU=0 Radius=2.5
    g154: Circle CenterX=-67.1608 CenterY=-38.766 CenterZ=0 NormalX=0 NormalY=0 NormalZ=1 AngleXU=0 Radius=2.5
    g155: Circle CenterX=-63.2047 CenterY=-32.8453 CenterZ=0 NormalX=0 NormalY=0 NormalZ=1 AngleXU=0 Radius=2.5
    g156: Circle CenterX=-57.284 CenterY=-28.8892 CenterZ=0 NormalX=0 NormalY=0 NormalZ=1 AngleXU=0 Radius=2.5
    g157: LineSegment [constr] StartX=-80.55 StartY=-45.75 StartZ=0 EndX=-20.05 EndY=-45.75 EndZ=0
    g158: LineSegment [constr] StartX=-50.3 StartY=-15.5 StartZ=0 EndX=-50.3 EndY=-76 EndZ=0
    g159: LineSegment [constr] StartX=-50.3 StartY=-21.5 StartZ=0 EndX=-50.3 EndY=-70 EndZ=0
    g160: LineSegment [constr] StartX=-74.55 StartY=-45.75 StartZ=0 EndX=-26.05 EndY=-45.75 EndZ=0
    g161: LineSegment [constr] StartX=-38.175 StartY=-24.7489 StartZ=0 EndX=-62.425 EndY=-66.7511 EndZ=0
    g162: LineSegment [constr] StartX=-44.0236 StartY=-22.3263 StartZ=0 EndX=-56.5764 EndY=-69.1737 EndZ=0
  constraints (431):
    c: Coincident(g1,g0)
    c: Coincident(g0,g3)
    c: Coincident(g2,g1)
    c: Coincident(g2,g3)
    c: DistanceY(g-1,g0) = -10
    c: Distance(g1) = 71.5
    c: Coincident(g6,g1)
    c: Radius(g6) = 2
    c: Equal(g6,g5)
    c: Equal(g5,g4)
    c: Equal(g4,g7)
    c: Vertical(g1)
    c: Coincident(g5,g0)
    c: Radius(g12) = 36.25
    c: DistanceX(g0) = 71.5
    c: Horizontal(g2)
    c: Horizontal(g0)
    c: Vertical(g3)
    c: Radius(g11) = 30.25
    c: Radius(g10) = 24.25
    c: Radius(g9) = 18.25
    c: PointOnObject(g12,g13)
    c: Vertical(g13)
    c: PointOnObject(g13,g12)
    c: PointOnObject(g13,g12)
    c: PointOnObject(g12,g14)
    c: Horizontal(g14)
    c: PointOnObject(g14,g12)
    c: PointOnObject(g14,g12)
    c: Coincident(g53,g13)
    c: PointOnObject(g12,g28)
    c: PointOnObject(g28,g12)
    c: PointOnObject(g28,g12)
    c: PointOnObject(g12,g20)
    c: PointOnObject(g12,g19)
    c: PointOnObject(g12,g18)
    c: PointOnObject(g12,g17)
    c: Angle(g13,g28) = 0.19635
    c: Angle(g28,g20) = 0.19635
    c: PointOnObject(g20,g12)
    c: Angle(g20,g19) = 0.19635
    c: PointOnObject(g19,g12)
    c: Coincident(g54,g28)
    c: Radius(g53) = 2.5
    c: Angle(g19,g18) = 0.19635
    c: PointOnObject(g18,g12)
    c: Angle(g18,g17) = 0.19635
    c: PointOnObject(g17,g12)
    c: PointOnObject(g12,g16)
    c: PointOnObject(g12,g15)
    c: PointOnObject(g12,g27)
    c: Angle(g17,g16) = 0.19635
    c: PointOnObject(g16,g12)
    c: Angle(g16,g15) = 0.19635
    c: PointOnObject(g15,g12)
    c: Angle(g14,g27) = 0.19635
    c: PointOnObject(g27,g12)
    c: PointOnObject(g12,g26)
    c: Angle(g27,g26) = 0.19635
    c: PointOnObject(g26,g12)
    c: PointOnObject(g12,g25)
    c: Angle(g26,g25) = 0.19635
    c: PointOnObject(g25,g12)
    c: PointOnObject(g12,g24)
    c: Angle(g25,g24) = 0.19635
    c: PointOnObject(g24,g12)
    c: PointOnObject(g12,g23)
    c: Angle(g24,g23) = 0.19635
    c: PointOnObject(g23,g12)
    c: PointOnObject(g12,g22)
    c: Angle(g23,g22) = 0.19635
    c: PointOnObject(g22,g12)
    c: PointOnObject(g12,g21)
    c: Angle(g22,g21) = 0.19635
    c: PointOnObject(g21,g12)
    c: PointOnObject(g20,g12)
    c: PointOnObject(g19,g12)
    c: PointOnObject(g18,g12)
    c: PointOnObject(g17,g12)
    c: PointOnObject(g16,g12)
    c: PointOnObject(g15,g12)
    c: PointOnObject(g27,g12)
    c: PointOnObject(g26,g12)
    c: PointOnObject(g25,g12)
    c: PointOnObject(g24,g12)
    c: PointOnObject(g23,g12)
    c: PointOnObject(g22,g12)
    c: PointOnObject(g21,g12)
    c: Coincident(g4,g0)
    c: Coincident(g7,g2)
    c: DistanceX(g-1,g0) = -14.55
    c: Coincident(g20,g55)
    c: Coincident(g19,g56)
    c: Coincident(g18,g57)
    c: Coincident(g17,g58)
    c: Coincident(g16,g59)
    c: Coincident(g15,g60)
    c: Coincident(g14,g37)
    c: Coincident(g27,g36)
    c: Coincident(g26,g35)
    c: Coincident(g25,g34)
    c: Coincident(g24,g33)
    c: Coincident(g23,g32)
    c: Coincident(g22,g31)
    c: Coincident(g21,g30)
    c: Coincident(g13,g29)
    c: Coincident(g28,g38)
    c: Coincident(g20,g39)
    c: Coincident(g19,g40)
    c: Coincident(g18,g41)
    c: Coincident(g17,g42)
    c: Coincident(g16,g43)
    c: Coincident(g15,g44)
    c: Coincident(g14,g45)
    c: Coincident(g27,g46)
    c: Coincident(g26,g47)
    c: Coincident(g25,g48)
    c: Coincident(g24,g49)
    c: Coincident(g23,g50)
    c: Coincident(g22,g51)
    c: Coincident(g21,g52)
    c: Equal(g53,g54)
    c: Equal(g54,g55)
    c: Equal(g55,g56)
    c: Equal(g56,g57)
    c: Equal(g57,g58)
    c: Equal(g58,g59)
    c: Equal(g59,g60)
    c: Equal(g60,g37)
    c: Equal(g37,g36)
    c: Equal(g36,g35)
    c: Equal(g35,g34)
    c: Equal(g34,g33)
    c: Equal(g33,g32)
    c: Equal(g32,g31)
    c: Equal(g31,g30)
    c: Equal(g30,g29)
    c: Equal(g29,g38)
    c: Equal(g38,g39)
    c: Equal(g39,g40)
    c: Equal(g40,g41)
    c: Equal(g41,g42)
    c: Equal(g42,g43)
    c: Equal(g43,g44)
    c: Equal(g44,g45)
    c: Equal(g45,g46)
    c: Equal(g46,g47)
    c: Equal(g47,g48)
    c: Equal(g48,g49)
    c: Equal(g49,g50)
    c: Equal(g50,g51)
    c: Equal(g51,g52)
    c: Vertical(g158)
    c: Horizontal(g157)
    c: PointOnObject(g157,g11)
    c: PointOnObject(g70,g11)
    c: PointOnObject(g69,g11)
    c: PointOnObject(g68,g11)
    c: PointOnObject(g67,g11)
    c: PointOnObject(g66,g11)
    c: PointOnObject(g65,g11)
    c: PointOnObject(g158,g11)
    c: PointOnObject(g71,g11)
    c: PointOnObject(g72,g11)
    c: PointOnObject(g73,g11)
    c: PointOnObject(g74,g11)
    c: PointOnObject(g75,g11)
    c: PointOnObject(g76,g11)
    c: PointOnObject(g157,g11)
    c: PointOnObject(g69,g11)
    c: PointOnObject(g70,g11)
    c: PointOnObject(g68,g11)
    c: PointOnObject(g67,g11)
    c: PointOnObject(g66,g11)
    c: PointOnObject(g65,g11)
    c: PointOnObject(g158,g11)
    c: PointOnObject(g71,g11)
    c: PointOnObject(g72,g11)
    c: PointOnObject(g73,g11)
    c: PointOnObject(g74,g11)
    c: PointOnObject(g75,g11)
    c: PointOnObject(g76,g11)
    c: PointOnObject(g11,g158)
    c: PointOnObject(g11,g157)
    c: PointOnObject(g11,g70)
    c: PointOnObject(g11,g74)
    c: PointOnObject(g11,g75)
    c: PointOnObject(g11,g76)
    c: PointOnObject(g11,g69)
    c: PointOnObject(g11,g73)
    c: PointOnObject(g11,g66)
    c: PointOnObject(g11,g72)
    c: PointOnObject(g11,g71)
    c: PointOnObject(g11,g68)
    c: PointOnObject(g11,g67)
    c: PointOnObject(g11,g65)
    c: Angle(g157,g70) = 0.224275
    c: Angle(g70,g69) = 0.224275
    c: Angle(g69,g68) = 0.224275
    c: Angle(g68,g66) = 0.224327
    c: Angle(g66,g65) = 0.224275
    c: Angle(g65,g67) = 0.224275
    c: Angle(g158,g71) = 0.224275
    c: Angle(g71,g72) = 0.224275
    c: Angle(g72,g73) = 0.224275
    c: Angle(g73,g74) = 0.224275
    c: Angle(g74,g75) = 0.224275
    c: Angle(g75,g76) = 0.224275
    c: Coincident(g64,g158)
    c: Coincident(g71,g94)
    c: Coincident(g72,g93)
    c: Coincident(g73,g92)
    c: Coincident(g74,g91)
    c: Coincident(g75,g90)
    c: Coincident(g76,g89)
    c: Coincident(g62,g157)
    c: Coincident(g70,g88)
    c: Coincident(g69,g87)
    c: Coincident(g68,g86)
    c: Coincident(g66,g85)
    c: Coincident(g65,g84)
    c: Coincident(g67,g83)
    c: Coincident(g61,g158)
    c: Coincident(g71,g82)
    c: Coincident(g72,g81)
    c: Coincident(g73,g80)
    c: Coincident(g74,g79)
    c: Coincident(g75,g78)
    c: Coincident(g76,g77)
    c: Coincident(g63,g157)
    c: Coincident(g70,g100)
    c: Coincident(g69,g99)
    c: Coincident(g68,g98)
    c: Coincident(g66,g97)
    c: Coincident(g65,g96)
    c: Coincident(g67,g95)
    c: Radius(g64) = 2.5
    c: Equal(g64,g94)
    c: Equal(g94,g93)
    c: Equal(g93,g92)
    c: Equal(g92,g91)
    c: Equal(g91,g90)
    c: Equal(g90,g89)
    c: Equal(g89,g62)
    c: Equal(g62,g88)
    c: Equal(g88,g87)
    c: Equal(g87,g86)
    c: Equal(g86,g85)
    c: Equal(g85,g84)
    c: Equal(g84,g83)
    c: Equal(g83,g61)
    c: Equal(g61,g82)
    c: Equal(g82,g81)
    c: Equal(g81,g80)
    c: Equal(g80,g79)
    c: Equal(g79,g78)
    c: Equal(g78,g77)
    c: Equal(g77,g63)
    c: Equal(g63,g100)
    c: Equal(g100,g99)
    c: Equal(g99,g98)
    c: Equal(g98,g97)
    c: Equal(g97,g96)
    c: Equal(g96,g95)
    c: Horizontal(g160)
    c: Vertical(g159)
    c: PointOnObject(g10,g159)
    c: PointOnObject(g10,g160)
    c: PointOnObject(g160,g10)
    c: PointOnObject(g160,g10)
    c: PointOnObject(g159,g10)
    c: PointOnObject(g159,g10)
    c: PointOnObject(g10,g105)
    c: PointOnObject(g10,g106)
    c: PointOnObject(g105,g10)
    c: PointOnObject(g106,g10)
    c: PointOnObject(g105,g10)
    c: PointOnObject(g106,g10)
    c: Angle(g159,g105) = 0.261799
    c: Angle(g105,g106) = 0.261799
    c: PointOnObject(g10,g107)
    c: PointOnObject(g107,g10)
    c: PointOnObject(g107,g10)
    c: Angle(g106,g107) = 0.261799
    c: PointOnObject(g10,g108)
    c: PointOnObject(g108,g10)
    c: PointOnObject(g108,g10)
    c: Angle(g107,g108) = 0.261799
    c: PointOnObject(g10,g104)
    c: PointOnObject(g104,g10)
    c: PointOnObject(g104,g10)
    c: Angle(g108,g104) = 0.261799
    c: PointOnObject(g10,g103)
    c: PointOnObject(g103,g10)
    c: PointOnObject(g103,g10)
    c: Angle(g160,g103) = 0.261799
    c: PointOnObject(g10,g102)
    c: PointOnObject(g102,g10)
    c: PointOnObject(g102,g10)
    c: Angle(g103,g102) = 0.261799
    c: PointOnObject(g10,g101)
    c: PointOnObject(g101,g10)
    c: PointOnObject(g101,g10)
    c: Angle(g102,g101) = 0.261799
    c: PointOnObject(g10,g161)
    c: PointOnObject(g10,g162)
    c: PointOnObject(g161,g10)
    c: PointOnObject(g162,g10)
    c: PointOnObject(g162,g10)
    c: PointOnObject(g161,g10)
    c: Angle(g101,g161) = 0.261799
    c: Angle(g161,g162) = 0.261799
    c: Coincident(g120,g159)
    c: Coincident(g106,g118)
    c: Coincident(g107,g117)
    c: Coincident(g108,g116)
    c: Coincident(g104,g115)
    c: Coincident(g114,g160)
    c: Coincident(g103,g113)
    c: Coincident(g102,g112)
    c: Coincident(g101,g111)
    c: Coincident(g110,g161)
    c: Coincident(g109,g162)
    c: Coincident(g132,g159)
    c: Coincident(g105,g131)
    c: Coincident(g106,g130)
    c: Coincident(g107,g129)
    c: Coincident(g108,g128)
    c: Coincident(g104,g126)
    c: Coincident(g127,g160)
    c: Coincident(g103,g125)
    c: Coincident(g102,g124)
    c: Coincident(g101,g123)
    c: Coincident(g122,g161)
    c: Coincident(g121,g162)
    c: Coincident(g105,g119)
    c: Radius(g120) = 2.5
    c: Equal(g119,g120)
    c: Equal(g120,g118)
    c: Equal(g118,g117)
    c: Equal(g117,g116)
    c: Equal(g116,g115)
    c: Equal(g115,g114)
    c: Equal(g114,g113)
    c: Equal(g113,g112)
    c: Equal(g112,g111)
    c: Equal(g111,g110)
    c: Equal(g110,g109)
    c: Equal(g109,g132)
    c: Equal(g132,g131)
    c: Equal(g131,g130)
    c: Equal(g130,g129)
    c: Equal(g129,g128)
    c: Equal(g128,g126)
    c: Equal(g126,g127)
    c: Equal(g127,g125)
    c: Equal(g125,g124)
    c: Equal(g124,g123)
    c: Equal(g123,g122)
    c: Equal(g122,g121)
    c: PointOnObject(g9,g136)
    c: Horizontal(g136)
    c: PointOnObject(g136,g9)
    c: PointOnObject(g136,g9)
    c: PointOnObject(g9,g135)
    c: PointOnObject(g135,g9)
    c: PointOnObject(g135,g9)
    c: Angle(g136,g135) = 0.392699
    c: PointOnObject(g9,g134)
    c: PointOnObject(g134,g9)
    c: PointOnObject(g134,g9)
    c: Angle(g135,g134) = 0.392699
    c: PointOnObject(g9,g133)
    c: PointOnObject(g133,g9)
    c: PointOnObject(g133,g9)
    c: Angle(g134,g133) = 0.392699
    c: PointOnObject(g140,g9)
    c: PointOnObject(g140,g9)
    c: PointOnObject(g9,g140)
    c: Vertical(g140)
    c: PointOnObject(g9,g139)
    c: PointOnObject(g139,g9)
    c: PointOnObject(g139,g9)
    c: Angle(g140,g139) = 0.392699
    c: PointOnObject(g9,g138)
    c: PointOnObject(g138,g9)
    c: PointOnObject(g138,g9)
    c: Angle(g139,g138) = 0.392699
    c: PointOnObject(g9,g137)
    c: PointOnObject(g137,g9)
    c: PointOnObject(g137,g9)
    c: Angle(g138,g137) = 0.392699
    c: DistanceX(g8,g0) = 35.75
    c: DistanceY(g0,g8) = -35.75
    c: Radius(g8) = 16
    c: Coincident(g140,g149)
    c: Coincident(g139,g148)
    c: Coincident(g138,g147)
    c: Coincident(g137,g146)
    c: Coincident(g136,g145)
    c: Coincident(g135,g144)
    c: Coincident(g134,g143)
    c: Coincident(g133,g142)
    c: Coincident(g140,g141)
    c: Coincident(g139,g156)
    c: Coincident(g138,g155)
    c: Coincident(g137,g154)
    c: Coincident(g136,g152)
    c: Coincident(g135,g153)
    c: Coincident(g134,g151)
    c: Coincident(g133,g150)
    c: Radius(g149) = 2.5
    c: Equal(g149,g148)
    c: Equal(g148,g147)
    c: Equal(g147,g146)
    c: Equal(g146,g145)
    c: Equal(g145,g144)
    c: Equal(g144,g143)
    c: Equal(g143,g142)
    c: Equal(g142,g141)
    c: Equal(g141,g156)
    c: Equal(g156,g155)
    c: Equal(g155,g154)
    c: Equal(g154,g152)
    c: Equal(g152,g153)
    c: Equal(g153,g151)
    c: Equal(g151,g150)
    c: Coincident(g8,g12)
    c: Coincident(g11,g8)
    c: Coincident(g8,g10)
    c: Coincident(g8,g9)
FEATURE [PartDesign::Pocket] Pocket006  label="exhaust001"
  Length = 5
  Profile = -> Sketch016
  Type = 0
FEATURE [Sketcher::SketchObject] Sketch018  label="pwr-input"
  MapMode = 5
  Placement = pos=(0,0,0) rot=(1,0,0;3.14159rad)
  Support = -> [Pocket006]
  sketch-geometry (8):
    g0: LineSegment [constr] StartX=-68.3 StartY=-450 StartZ=0 EndX=-32.3 EndY=-450 EndZ=0
    g1: LineSegment StartX=-64.8 StartY=-433.5 StartZ=0 EndX=-35.8 EndY=-433.5 EndZ=0
    g2: LineSegment StartX=-35.8 StartY=-433.5 StartZ=0 EndX=-35.8 EndY=-466.5 EndZ=0
    g3: LineSegment StartX=-35.8 StartY=-466.5 StartZ=0 EndX=-64.8 EndY=-466.5 EndZ=0
    g4: LineSegment StartX=-64.8 StartY=-466.5 StartZ=0 EndX=-64.8 EndY=-433.5 EndZ=0
    g5: LineSegment [constr] StartX=-50.3 StartY=-433.5 StartZ=0 EndX=-50.3 EndY=-466.5 EndZ=0
    g6: Circle CenterX=-68.3 CenterY=-450 CenterZ=0 NormalX=0 NormalY=0 NormalZ=1 AngleXU=0 Radius=1.7
    g7: Circle CenterX=-32.3 CenterY=-450 CenterZ=0 NormalX=0 NormalY=0 NormalZ=1 AngleXU=0 Radius=1.7
  constraints (24):
    c: DistanceY(g-1,g0) = -450
    c: DistanceX(g-1,g5) = -50.3
    c: Coincident(g3,g4)
    c: Coincident(g2,g3)
    c: Coincident(g1,g2)
    c: Coincident(g1,g4)
    c: Horizontal(g1)
    c: Horizontal(g3)
    c: Vertical(g2)
    c: Vertical(g4)
    c: DistanceX(g5,g0) = 18
    c: Coincident(g7,g0)
    c: DistanceX(g0) = 36
    c: Coincident(g0,g6)
    c: DistanceY(g2) = -33
    c: DistanceY(g0,g1) = 16.5
    c: Horizontal(g0)
    c: DistanceX(g3) = -29
    c: Radius(g7) = 1.7
    c: Equal(g7,g6)
    c: PointOnObject(g5,g1)
    c: PointOnObject(g5,g3)
    c: Vertical(g5)
    c: DistanceX(g5,g2) = 14.5
FEATURE [PartDesign::Pocket] Pocket007  label="input-power"
  Length = 5
  Profile = -> Sketch018
  Type = 0
FEATURE [Sketcher::SketchObject] Sketch017  label="pwrattach"
  MapMode = 5
  Placement = pos=(-100.6,0,0) rot=(-0.57735,0.57735,0.57735;4.18879rad)
  Support = -> [Pocket007]
  sketch-geometry (9):
    g0: LineSegment [constr] StartX=-390 StartY=121.03 StartZ=0 EndX=-230.3 EndY=121.03 EndZ=0
    g1: LineSegment [constr] StartX=-230.3 StartY=121.03 StartZ=0 EndX=-230.3 EndY=32.03 EndZ=0
    g2: LineSegment [constr] StartX=-230.3 StartY=32.03 StartZ=0 EndX=-390 EndY=32.03 EndZ=0
    g3: LineSegment [constr] StartX=-390 StartY=32.03 StartZ=0 EndX=-390 EndY=121.03 EndZ=0
    g4: Circle CenterX=-341.3 CenterY=71.03 CenterZ=0 NormalX=0 NormalY=0 NormalZ=1 AngleXU=0 Radius=2.1
    g5: Circle CenterX=-390 CenterY=121.03 CenterZ=0 NormalX=0 NormalY=0 NormalZ=1 AngleXU=0 Radius=2.1
    g6: Circle CenterX=-230.3 CenterY=121.03 CenterZ=0 NormalX=0 NormalY=0 NormalZ=1 AngleXU=0 Radius=2.1
    g7: Circle CenterX=-230.3 CenterY=32.03 CenterZ=0 NormalX=0 NormalY=0 NormalZ=1 AngleXU=0 Radius=2.1
    g8: Circle CenterX=-390 CenterY=32.03 CenterZ=0 NormalX=0 NormalY=0 NormalZ=1 AngleXU=0 Radius=2.1
  constraints (23):
    c: Coincident(g0,g1)
    c: Coincident(g0,g3)
    c: Coincident(g1,g2)
    c: Coincident(g2,g3)
    c: DistanceY(g-1,g1) = 32.03
    c: DistanceY(g1) = -89
    c: DistanceX(g-1,g1) = -230.3
    c: DistanceX(g2) = -159.7
    c: DistanceY(g1,g4) = 39
    c: DistanceX(g1,g4) = -111
    c: Radius(g6) = 2.1
    c: Equal(g7,g8)
    c: Equal(g8,g4)
    c: Equal(g4,g5)
    c: Equal(g5,g6)
    c: Coincident(g0,g6)
    c: Coincident(g0,g5)
    c: Coincident(g2,g8)
    c: Coincident(g1,g7)
    c: Horizontal(g2)
    c: Horizontal(g0)
    c: Vertical(g1)
    c: Vertical(g3)
FEATURE [PartDesign::Pocket] Pocket008  label="power-attach"
  Length = 5
  Profile = -> Sketch017
  Type = 0
FEATURE [Sketcher::SketchObject] Sketch019
  MapMode = 5
  Placement = pos=(0,0,0) rot=(1,0,0;3.14159rad)
  Support = -> [Pocket008]
  sketch-geometry (26):
    g0: Circle CenterX=-30 CenterY=-150 CenterZ=0 NormalX=0 NormalY=0 NormalZ=1 AngleXU=0 Radius=15.365
    g1: LineSegment [constr] StartX=-30 StartY=-150 StartZ=0 EndX=-30 EndY=-180 EndZ=0
    g2: LineSegment [constr] StartX=-30 StartY=-150 StartZ=0 EndX=30 EndY=-150 EndZ=0
    g3: LineSegment [constr] StartX=-44.29 StartY=-135.75 StartZ=0 EndX=-15.75 EndY=-135.75 EndZ=0
    g4: LineSegment [constr] StartX=-15.75 StartY=-135.75 StartZ=0 EndX=-15.75 EndY=-164.29 EndZ=0
    g5: LineSegment [constr] StartX=-15.75 StartY=-164.29 StartZ=0 EndX=-44.29 EndY=-164.29 EndZ=0
    g6: LineSegment [constr] StartX=-44.29 StartY=-164.29 StartZ=0 EndX=-44.29 EndY=-135.75 EndZ=0
    g7: Circle CenterX=-44.29 CenterY=-135.75 CenterZ=0 NormalX=0 NormalY=0 NormalZ=1 AngleXU=0 Radius=1.905
    g8: Circle CenterX=-15.75 CenterY=-135.75 CenterZ=0 NormalX=0 NormalY=0 NormalZ=1 AngleXU=0 Radius=1.905
    g9: Circle CenterX=-15.75 CenterY=-164.29 CenterZ=0 NormalX=0 NormalY=0 NormalZ=1 AngleXU=0 Radius=1.905
    g10: Circle CenterX=-44.29 CenterY=-164.29 CenterZ=0 NormalX=0 NormalY=0 NormalZ=1 AngleXU=0 Radius=1.905
    g11: LineSegment [constr] StartX=-85.3 StartY=-220 StartZ=0 EndX=-15.3 EndY=-220 EndZ=0
    g12: LineSegment [constr] StartX=-15.3 StartY=-220 StartZ=0 EndX=-15.3 EndY=-400 EndZ=0
    g13: LineSegment [constr] StartX=-15.3 StartY=-400 StartZ=0 EndX=-85.3 EndY=-400 EndZ=0
    g14: LineSegment [constr] StartX=-85.3 StartY=-400 StartZ=0 EndX=-85.3 EndY=-220 EndZ=0
    g15: Circle CenterX=-85.3 CenterY=-220 CenterZ=0 NormalX=0 NormalY=0 NormalZ=1 AngleXU=0 Radius=2.5
    g16: Circle CenterX=-15.3 CenterY=-220 CenterZ=0 NormalX=0 NormalY=0 NormalZ=1 AngleXU=0 Radius=2.5
    g17: Circle CenterX=-15.3 CenterY=-400 CenterZ=0 NormalX=0 NormalY=0 NormalZ=1 AngleXU=0 Radius=2.5
    g18: Circle CenterX=-85.3 CenterY=-400 CenterZ=0 NormalX=0 NormalY=0 NormalZ=1 AngleXU=0 Radius=2.5
    g19: ArcOfCircle CenterX=-30.3 CenterY=-235 CenterZ=0 NormalX=0 NormalY=0 NormalZ=1 AngleXU=0 Radius=10 StartAngle=0 EndAngle=3.14159
    g20: ArcOfCircle CenterX=-30.3 CenterY=-385 CenterZ=0 NormalX=0 NormalY=0 NormalZ=1 AngleXU=0 Radius=10 StartAngle=3.14159 EndAngle=6.28319
    g21: LineSegment StartX=-40.3 StartY=-235 StartZ=0 EndX=-40.3 EndY=-385 EndZ=0
    g22: LineSegment StartX=-20.3 StartY=-235 StartZ=0 EndX=-20.3 EndY=-385 EndZ=0
    g23: Circle CenterX=-85.3 CenterY=-310 CenterZ=0 NormalX=0 NormalY=0 NormalZ=1 AngleXU=0 Radius=2.5
    g24: Circle CenterX=-15.3 CenterY=-310 CenterZ=0 NormalX=0 NormalY=0 NormalZ=1 AngleXU=0 Radius=2.5
    g25: LineSegment [constr] StartX=-85.3 StartY=-310 StartZ=0 EndX=-15.3 EndY=-310 EndZ=0
  constraints (67):
    c: Vertical(g1)
    c: Horizontal(g2)
    c: Coincident(g2,g1)
    c: DistanceX(g-1,g1) = -30
    c: Coincident(g0,g1)
    c: Radius(g0) = 15.365
    c: Coincident(g3,g4)
    c: Coincident(g4,g5)
    c: Coincident(g5,g6)
    c: Coincident(g6,g3)
    c: Horizontal(g3)
    c: Horizontal(g5)
    c: Vertical(g4)
    c: Vertical(g6)
    c: Equal(g6,g5)
    c: DistanceY(g0,g4) = -14.29
    c: Distance(g2) = 60
    c: Coincident(g4,g9)
    c: Coincident(g3,g8)
    c: Coincident(g3,g7)
    c: Coincident(g5,g10)
    c: Radius(g7) = 1.905
    c: Equal(g8,g9)
    c: Equal(g9,g10)
    c: DistanceY(g-1,g2) = -150
    c: Coincident(g11,g12)
    c: Coincident(g12,g13)
    c: Coincident(g13,g14)
    c: Coincident(g14,g11)
    c: Horizontal(g11)
    c: Horizontal(g13)
    c: Vertical(g12)
    c: Vertical(g14)
    c: DistanceX(g13) = -70
    c: DistanceY(g14) = 180
    c: Coincident(g12,g17)
    c: Coincident(g13,g18)
    c: Coincident(g11,g15)
    c: Coincident(g11,g16)
    c: Equal(g16,g15)
    c: Equal(g15,g18)
    c: Equal(g18,g17)
    c: Radius(g15) = 2.5
    c: DistanceY(g-1,g11) = -220
    c: DistanceX(g-1,g11) = -15.3
    c: Equal(g7,g10)
    c: DistanceY(g-1,g3) = -135.75
    c: DistanceX(g-1,g3) = -15.75
    c: DistanceY(g1) = -30
    c: Tangent(g19,g22) = 1.5708
    c: Tangent(g19,g21) = -1.5708
    c: Tangent(g21,g20) = -1.5708
    c: Tangent(g22,g20) = 1.5708
    c: Vertical(g21)
    c: Equal(g19,g20)
    c: Radius(g19) = 10
    c: DistanceX(g19,g11) = 5
    c: DistanceY(g19,g11) = 15
    c: DistanceY(g20,g12) = -15
    c: DistanceY(g11,g24) = -90
    c: Horizontal(g25)
    c: Coincident(g25,g24)
    c: PointOnObject(g24,g12)
    c: PointOnObject(g25,g14)
    c: Coincident(g23,g25)
    c: Equal(g18,g24)
    c: Equal(g24,g23)
FEATURE [PartDesign::Pocket] Pocket009  label="cable-exit"
  Length = 5
  Profile = -> Sketch019
  Type = 0
FEATURE [Sketcher::SketchObject] Sketch021
  MapMode = 5
  Placement = pos=(-100.6,0,0) rot=(-0.57735,0.57735,0.57735;4.18879rad)
  Support = -> [Pocket009]
  sketch-geometry (8):
    g0: LineSegment [constr] StartX=-189.25 StartY=104.52 StartZ=0 EndX=-94 EndY=104.52 EndZ=0
    g1: LineSegment [constr] StartX=-94 StartY=104.52 StartZ=0 EndX=-94 EndY=8 EndZ=0
    g2: LineSegment [constr] StartX=-94 StartY=8 StartZ=0 EndX=-189.25 EndY=8 EndZ=0
    g3: LineSegment [constr] StartX=-189.25 StartY=8 StartZ=0 EndX=-189.25 EndY=104.52 EndZ=0
    g4: Circle CenterX=-189.25 CenterY=104.52 CenterZ=0 NormalX=0 NormalY=0 NormalZ=1 AngleXU=0 Radius=2.5
    g5: Circle CenterX=-94 CenterY=104.52 CenterZ=0 NormalX=0 NormalY=0 NormalZ=1 AngleXU=0 Radius=2.5
    g6: Circle CenterX=-94 CenterY=8 CenterZ=0 NormalX=0 NormalY=0 NormalZ=1 AngleXU=0 Radius=2.5
    g7: Circle CenterX=-189.25 CenterY=8 CenterZ=0 NormalX=0 NormalY=0 NormalZ=1 AngleXU=0 Radius=2.5
  constraints (20):
    c: Coincident(g0,g1)
    c: Coincident(g1,g2)
    c: Coincident(g2,g3)
    c: Coincident(g3,g0)
    c: Horizontal(g0)
    c: Horizontal(g2)
    c: Vertical(g1)
    c: Vertical(g3)
    c: DistanceX(g0) = 95.25
    c: DistanceY(g3) = 96.52
    c: Coincident(g0,g4)
    c: Coincident(g0,g5)
    c: Coincident(g1,g6)
    c: Coincident(g7,g2)
    c: Radius(g7) = 2.5
    c: Equal(g7,g6)
    c: Equal(g6,g5)
    c: Equal(g5,g4)
    c: DistanceX(g-1,g1) = -94
    c: DistanceY(g-1,g1) = 8
FEATURE [PartDesign::Pocket] Pocket010  label="board-attach"
  Length = 5
  Profile = -> Sketch021
  Type = 0
FEATURE [Sketcher::SketchObject] Sketch022
  MapMode = 5
  Placement = pos=(0,0,0) rot=(1,0,0;3.14159rad)
  Support = -> [Pocket010]
  sketch-geometry (10):
    g0: LineSegment StartX=-87.6 StartY=-127.5 StartZ=0 EndX=-74.6 EndY=-127.5 EndZ=0
    g1: LineSegment StartX=-74.6 StartY=-127.5 StartZ=0 EndX=-74.6 EndY=-141.5 EndZ=0
    g2: LineSegment StartX=-74.6 StartY=-141.5 StartZ=0 EndX=-87.6 EndY=-141.5 EndZ=0
    g3: LineSegment StartX=-87.6 StartY=-141.5 StartZ=0 EndX=-87.6 EndY=-127.5 EndZ=0
    g4: LineSegment [constr] StartX=-110 StartY=-94 StartZ=0 EndX=0 EndY=-94 EndZ=0
    g5: LineSegment [constr] StartX=-110 StartY=-90.19 StartZ=0 EndX=0 EndY=-90.19 EndZ=0
    g6: LineSegment [constr] StartX=-110 StartY=-193.06 StartZ=0 EndX=0 EndY=-193.06 EndZ=0
    g7: LineSegment [constr] StartX=-110 StartY=-113.49 StartZ=0 EndX=0 EndY=-113.49 EndZ=0
    g8: LineSegment [constr] StartX=-110 StartY=-90.19 StartZ=0 EndX=-110 EndY=-193.06 EndZ=0
    g9: Circle CenterX=-83.6 CenterY=-113.49 CenterZ=0 NormalX=0 NormalY=0 NormalZ=1 AngleXU=0 Radius=2
  constraints (33):
    c: Coincident(g0,g1)
    c: Coincident(g1,g2)
    c: Coincident(g2,g3)
    c: Coincident(g3,g0)
    c: Horizontal(g0)
    c: Horizontal(g2)
    c: Vertical(g1)
    c: Vertical(g3)
    c: DistanceY(g1) = -14
    c: DistanceX(g0) = 13
    c: DistanceX(g-1,g0) = -74.6
    c: DistanceY(g-1,g0) = -127.5
    c: DistanceY(g-1,g4) = -94
    c: Horizontal(g4)
    c: Horizontal(g5)
    c: DistanceY(g4,g5) = 3.81
    c: Horizontal(g6)
    c: DistanceY(g5,g6) = -102.87
    c: Horizontal(g7)
    c: DistanceY(g6,g7) = 79.57
    c: PointOnObject(g5,g-2)
    c: PointOnObject(g7,g-2)
    c: PointOnObject(g6,g-2)
    c: Vertical(g8)
    c: Coincident(g5,g8)
    c: Coincident(g6,g8)
    c: PointOnObject(g4,g8)
    c: PointOnObject(g7,g8)
    c: PointOnObject(g4,g-2)
    c: DistanceX(g-1,g5) = -110
    c: PointOnObject(g9,g7)
    c: DistanceX(g0,g9) = 4
    c: Radius(g9) = 2
FEATURE [PartDesign::Pocket] Pocket011  label="usb"
  Length = 5
  Profile = -> Sketch022
  Type = 0
FEATURE [Sketcher::SketchObject] Sketch023
  MapMode = 5
  Placement = pos=(0,0,158) rot=(1,0,0;3.14159rad)
  Support = -> [Pocket011]
  sketch-geometry (8):
    g0: LineSegment [constr] StartX=31.3 StartY=141 StartZ=0 EndX=448.7 EndY=141 EndZ=0
    g1: LineSegment [constr] StartX=31.3 StartY=29 StartZ=0 EndX=448.7 EndY=29 EndZ=0
    g2: LineSegment [constr] StartX=31.3 StartY=141 StartZ=0 EndX=31.3 EndY=29 EndZ=0
    g3: LineSegment [constr] StartX=448.7 StartY=141 StartZ=0 EndX=448.7 EndY=29 EndZ=0
    g4: Circle CenterX=31.3 CenterY=141 CenterZ=0 NormalX=0 NormalY=0 NormalZ=1 AngleXU=0 Radius=3.175
    g5: Circle CenterX=448.7 CenterY=141 CenterZ=0 NormalX=0 NormalY=0 NormalZ=1 AngleXU=0 Radius=3.175
    g6: Circle CenterX=448.7 CenterY=29 CenterZ=0 NormalX=0 NormalY=0 NormalZ=1 AngleXU=0 Radius=3.175
    g7: Circle CenterX=31.3 CenterY=29 CenterZ=0 NormalX=0 NormalY=0 NormalZ=1 AngleXU=0 Radius=3.175
  constraints (4):
    c: Coincident(g0,g2)
    c: Coincident(g0,g3)
    c: Coincident(g1,g2)
    c: Coincident(g1,g3)
FEATURE [PartDesign::Pocket] Pocket012  label="chassis-attach"
  Length = 5
  Profile = -> Sketch023
  Type = 0
FEATURE [Sketcher::SketchObject] Sketch027
  MapMode = 5
  Placement = pos=(0,0,0) rot=(0.57735,0.57735,0.57735;2.0944rad)
  Support = -> [Pocket012]
  sketch-geometry (29):
    g0: LineSegment [constr] StartX=6 StartY=85 StartZ=0 EndX=474 EndY=85 EndZ=0
    g1: LineSegment [constr] StartX=6 StartY=164 StartZ=0 EndX=6 EndY=6 EndZ=0
    g2: LineSegment [constr] StartX=6 StartY=30 StartZ=0 EndX=474 EndY=30 EndZ=0
    g3: LineSegment [constr] StartX=474 StartY=164 StartZ=0 EndX=474 EndY=30 EndZ=0
    g4: LineSegment [constr] StartX=310 StartY=164 StartZ=0 EndX=310 EndY=6 EndZ=0
    g5: LineSegment [constr] StartX=170 StartY=164 StartZ=0 EndX=170 EndY=6 EndZ=0
    g6: LineSegment [constr] StartX=0 StartY=0 StartZ=0 EndX=480 EndY=0 EndZ=0
    g7: LineSegment [constr] StartX=480 StartY=0 StartZ=0 EndX=480 EndY=170 EndZ=0
    g8: LineSegment [constr] StartX=480 StartY=170 StartZ=0 EndX=0 EndY=170 EndZ=0
    g9: LineSegment [constr] StartX=0 StartY=170 StartZ=0 EndX=0 EndY=0 EndZ=0
    g10: LineSegment [constr] StartX=6 StartY=164 StartZ=0 EndX=474 EndY=164 EndZ=0
    g11: LineSegment [constr] StartX=6 StartY=6 StartZ=0 EndX=450 EndY=6 EndZ=0
    g12: LineSegment [constr] StartX=30 StartY=164 StartZ=0 EndX=30 EndY=6 EndZ=0
    g13: LineSegment [constr] StartX=450 StartY=164 StartZ=0 EndX=450 EndY=6 EndZ=0
    g14: LineSegment [constr] StartX=6 StartY=140 StartZ=0 EndX=474 EndY=140 EndZ=0
    g15: Circle CenterX=450 CenterY=164 CenterZ=0 NormalX=0 NormalY=0 NormalZ=1 AngleXU=0 Radius=2.11
    g16: Circle CenterX=474 CenterY=140 CenterZ=0 NormalX=0 NormalY=0 NormalZ=1 AngleXU=0 Radius=2.11
    g17: Circle CenterX=474 CenterY=85 CenterZ=0 NormalX=0 NormalY=0 NormalZ=1 AngleXU=0 Radius=2.11
    g18: Circle CenterX=474 CenterY=30 CenterZ=0 NormalX=0 NormalY=0 NormalZ=1 AngleXU=0 Radius=2.11
    g19: Circle CenterX=450 CenterY=6 CenterZ=0 NormalX=0 NormalY=0 NormalZ=1 AngleXU=0 Radius=2.11
    g20: Circle CenterX=310 CenterY=6 CenterZ=0 NormalX=0 NormalY=0 NormalZ=1 AngleXU=0 Radius=2.11
    g21: Circle CenterX=170 CenterY=6 CenterZ=0 NormalX=0 NormalY=0 NormalZ=1 AngleXU=0 Radius=2.11
    g22: Circle CenterX=30 CenterY=6 CenterZ=0 NormalX=0 NormalY=0 NormalZ=1 AngleXU=0 Radius=2.11
    g23: Circle CenterX=6 CenterY=30 CenterZ=0 NormalX=0 NormalY=0 NormalZ=1 AngleXU=0 Radius=2.11
    g24: Circle CenterX=6 CenterY=85 CenterZ=0 NormalX=0 NormalY=0 NormalZ=1 AngleXU=0 Radius=2.11
    g25: Circle CenterX=6 CenterY=140 CenterZ=0 NormalX=0 NormalY=0 NormalZ=1 AngleXU=0 Radius=2.11
    g26: Circle CenterX=30 CenterY=164 CenterZ=0 NormalX=0 NormalY=0 NormalZ=1 AngleXU=0 Radius=2.11
    g27: Circle CenterX=170 CenterY=164 CenterZ=0 NormalX=0 NormalY=0 NormalZ=1 AngleXU=0 Radius=2.11
    g28: Circle CenterX=310 CenterY=164 CenterZ=0 NormalX=0 NormalY=0 NormalZ=1 AngleXU=0 Radius=2.11
  constraints (78):
    c: Horizontal(g0)
    c: Horizontal(g2)
    c: Vertical(g1)
    c: Vertical(g5)
    c: Vertical(g4)
    c: Vertical(g3)
    c: Coincident(g6,g7)
    c: Coincident(g7,g8)
    c: Coincident(g8,g9)
    c: Coincident(g9,g6)
    c: Horizontal(g6)
    c: Horizontal(g8)
    c: Vertical(g7)
    c: Vertical(g9)
    c: Coincident(g6,g-1)
    c: DistanceY(g7) = 170
    c: DistanceX(g8) = -480
    c: DistanceX(g-1,g1) = 6
    c: DistanceY(g-1,g2) = 30
    c: DistanceY(g-1,g0) = 85
    c: PointOnObject(g0,g1)
    c: DistanceX(g-1,g3) = 474
    c: Coincident(g2,g3)
    c: PointOnObject(g0,g3)
    c: Horizontal(g11)
    c: Horizontal(g10)
    c: DistanceY(g-1,g11) = 6
    c: Coincident(g1,g11)
    c: DistanceY(g-1,g10) = 164
    c: Coincident(g1,g10)
    c: Coincident(g3,g10)
    c: Vertical(g12)
    c: Vertical(g13)
    c: DistanceX(g-1,g12) = 30
    c: PointOnObject(g2,g1)
    c: PointOnObject(g12,g11)
    c: DistanceX(g-1,g13) = 450
    c: Coincident(g11,g13)
    c: PointOnObject(g13,g10)
    c: PointOnObject(g4,g10)
    c: PointOnObject(g5,g10)
    c: PointOnObject(g5,g11)
    c: PointOnObject(g4,g11)
    c: DistanceX(g12,g5) = 140
    c: DistanceX(g4,g11) = 140
    c: PointOnObject(g12,g10)
    c: Horizontal(g14)
    c: DistanceY(g-1,g14) = 140
    c: PointOnObject(g14,g1)
    c: PointOnObject(g14,g3)
    c: Coincident(g13,g15)
    c: Radius(g15) = 2.11
    c: Coincident(g14,g16)
    c: Coincident(g0,g17)
    c: Coincident(g2,g18)
    c: Coincident(g11,g19)
    c: Coincident(g4,g20)
    c: Coincident(g5,g21)
    c: Coincident(g12,g22)
    c: Coincident(g2,g23)
    c: Coincident(g0,g24)
    c: Coincident(g14,g25)
    c: Coincident(g12,g26)
    c: Coincident(g5,g27)
    c: Coincident(g4,g28)
    c: Equal(g15,g16)
    c: Equal(g16,g17)
    c: Equal(g17,g18)
    c: Equal(g18,g19)
    c: Equal(g19,g20)
    c: Equal(g20,g28)
    c: Equal(g28,g27)
    c: Equal(g27,g21)
    c: Equal(g21,g22)
    c: Equal(g22,g26)
    c: Equal(g26,g25)
    c: Equal(g25,g24)
    c: Equal(g24,g23)
FEATURE [PartDesign::Pocket] Pocket013  label="cover-attach"
  Length = 5
  Profile = -> Sketch027
  Type = 0
FEATURE [Sketcher::SketchObject] Sketch033
  MapMode = 5
  Placement = pos=(-100.6,0,0) rot=(-0.57735,0.57735,0.57735;4.18879rad)
  Support = -> [Pocket013]
  sketch-geometry (8):
    g0: LineSegment [constr] StartX=-448.75 StartY=141 StartZ=0 EndX=-26.25 EndY=141 EndZ=0
    g1: LineSegment [constr] StartX=-26.25 StartY=141 StartZ=0 EndX=-26.25 EndY=29 EndZ=0
    g2: LineSegment [constr] StartX=-26.25 StartY=29 StartZ=0 EndX=-448.75 EndY=29 EndZ=0
    g3: LineSegment [constr] StartX=-448.75 StartY=29 StartZ=0 EndX=-448.75 EndY=141 EndZ=0
    g4: Circle CenterX=-448.75 CenterY=141 CenterZ=0 NormalX=0 NormalY=0 NormalZ=1 AngleXU=0 Radius=3.175
    g5: Circle CenterX=-26.25 CenterY=141 CenterZ=0 NormalX=0 NormalY=0 NormalZ=1 AngleXU=0 Radius=3.175
    g6: Circle CenterX=-26.25 CenterY=29 CenterZ=0 NormalX=0 NormalY=0 NormalZ=1 AngleXU=0 Radius=3.175
    g7: Circle CenterX=-448.75 CenterY=29 CenterZ=0 NormalX=0 NormalY=0 NormalZ=1 AngleXU=0 Radius=3.175
  constraints (20):
    c: Coincident(g0,g1)
    c: Coincident(g0,g3)
    c: Coincident(g1,g2)
    c: Coincident(g2,g3)
    c: DistanceY(g-1,g1) = 29
    c: DistanceY(g1) = -112
    c: DistanceX(g-1,g1) = -26.25
    c: DistanceX(g2) = -422.5
    c: Radius(g6) = 3.175
    c: Equal(g6,g5)
    c: Equal(g5,g4)
    c: Equal(g4,g7)
    c: Coincident(g0,g4)
    c: Coincident(g2,g7)
    c: Coincident(g1,g6)
    c: Coincident(g0,g5)
    c: Horizontal(g2)
    c: Horizontal(g0)
    c: Vertical(g3)
    c: Vertical(g1)
FEATURE [PartDesign::Pocket] Pocket014  label="Electronics-attach"
  Length = 5
  Profile = -> Sketch033
  Type = 0
FEATURE [Sketcher::SketchObject] Sketch034
  ExternalGeometry = -> [Pocket014]
  MapMode = 5
  Placement = pos=(0,480,0) rot=(0,0.707107,0.707107;3.14159rad)
  Support = -> [Pocket014]
  sketch-geometry (1):
    g0: Circle CenterX=30 CenterY=120 CenterZ=0 NormalX=0 NormalY=0 NormalZ=1 AngleXU=0 Radius=1.5
  constraints (3):
    c: DistanceY(g0,g-4) = 50
    c: DistanceX(g-1,g0) = 30
    c: Radius(g0) = 1.5
FEATURE [PartDesign::Pocket] Pocket015
  Length = 5
  Profile = -> Sketch034
  Type = 0
FEATURE [Sketcher::SketchObject] Sketch035
  MapMode = 5
  Placement = pos=(0,0,0) rot=(1,0,0;3.14159rad)
  Support = -> [Pocket015]
  sketch-geometry (1):
    g0: Circle CenterX=-30 CenterY=-200 CenterZ=0 NormalX=0 NormalY=0 NormalZ=1 AngleXU=0 Radius=1.5
  constraints (3):
    c: DistanceY(g-1,g0) = -200
    c: DistanceX(g-1,g0) = -30
    c: Radius(g0) = 1.5
FEATURE [PartDesign::Pocket] Pocket016
  Length = 5
  Profile = -> Sketch035
  Type = 0
FEATURE [PartDesign::Chamfer] Chamfer
  Base = -> Pocket016 [Edge159,Edge158,Edge161,Edge157,Edge160]
  Size = 1
FEATURE [PartDesign::Fillet] Fillet
  Base = -> Chamfer [Edge330,Edge611,Edge320,Edge308,Edge345,Edge626,Edge846,Edge838]
  Radius = 1
FEATURE [PartDesign::Fillet] Fillet001
  Base = -> Fillet [Edge571,Edge48,Edge47,Edge199,Edge200,Edge183,Edge184,Edge45,Edge20,Edge19,Edge8,Edge18]
  Radius = 1
FEATURE [PartDesign::Fillet] Fillet002
  Base = -> Fillet001 [Edge206,Edge28,Edge42,Edge39,Edge38,Edge338,Edge339,Edge202,Edge203,Edge757,Edge350,Edge346]
  Radius = 1
FEATURE [PartDesign::Fillet] Fillet003
  Base = -> Fillet002 [Edge55,Edge48,Edge6,Edge36,Edge593,Edge595,Edge789,Edge792]
  Radius = 1
FEATURE [Drawing::FeatureView] dim014
  Rotation = 0
  ViewResult = <g>  <circle cx ="38.400000" cy ="74.185000" r="0.500000" stroke="none" fill="rgb(0,0,255)" /> \n<line x1="42.344533" y1="59.726702" x2="38.400000" y2="74.185000" style="stroke:rgb(0,0,255);stroke-width:0.20" />\n<polygon points="38.595427,73.468680 40.108589,70.771859 39.385033,70.574458 38.661478,70.377056" style="fill:rgb(0,0,255);stroke:rgb(0,0,255);stroke-width:0" />\n<line x1="42.344533" y1="59.726702" x2="65.346502" y2="59.726702" style="stroke:rgb(0,0,255);stroke-width:0.20" />\n<text x="53.845517" y="58.726702" font-family="Verdana" font-size="3.6" fill="rgb(0,0,255)" text-anchor="middle"  >40X R1.65</text> </g>
  Visible = true
  X = 0
  Y = 0
FEATURE [Drawing::FeatureView] dim009
  Rotation = 0
  ViewResult = <g> <line x1="47.917500" y1="113.085000" x2="47.917500" y2="125.774028" style="stroke:rgb(0,0,255);stroke-width:0.20" />\n<line x1="49.357500" y1="113.085000" x2="49.357500" y2="125.774028" style="stroke:rgb(0,0,255);stroke-width:0.20" />\n<line x1="47.917500" y1="124.774028" x2="49.357500" y2="124.774028" style="stroke:rgb(0,0,255);stroke-width:0.20" />\n<polygon points="47.917500,124.774028 44.917500,124.024028 44.917500,124.774028 44.917500,125.524028" style="fill:rgb(0,0,255);stroke:rgb(0,0,255);stroke-width:0" />\n<polygon points="49.357500,124.774028 52.357500,125.524028 52.357500,124.774028 52.357500,124.024028" style="fill:rgb(0,0,255);stroke:rgb(0,0,255);stroke-width:0" />\n<text x="61.201965" y="126.243168" font-family="Verdana" font-size="3.6" fill="rgb(0,0,255)" text-anchor="middle"  >7X 3.2 </text> </g> 
  Visible = true
  X = 0
  Y = 0
FEATURE [Drawing::FeatureView] dim048
  Rotation = 0
  ViewResult = <g> <line x1="46.580000" y1="105.540000" x2="25.897898" y2="105.540000" style="stroke:rgb(0,0,255);stroke-width:0.20" />\n<line x1="53.679987" y1="107.080000" x2="25.897898" y2="107.080000" style="stroke:rgb(0,0,255);stroke-width:0.20" />\n<line x1="26.897898" y1="105.540000" x2="26.897898" y2="107.080000" style="stroke:rgb(0,0,255);stroke-width:0.20" />\n<polygon points="26.897898,105.540000 27.647898,102.540000 26.897898,102.540000 26.147898,102.540000" style="fill:rgb(0,0,255);stroke:rgb(0,0,255);stroke-width:0" />\n<polygon points="26.897898,107.080000 26.147898,110.080000 26.897898,110.080000 27.647898,110.080000" style="fill:rgb(0,0,255);stroke:rgb(0,0,255);stroke-width:0" />\n<text x="25.897898" y="106.310000" font-family="Verdana" font-size="3.6" fill="rgb(0,0,255)" text-anchor="middle" transform="rotate(-90.000000 25.897898,106.310000)" >3.85</text> </g> 
  Visible = true
  X = 0
  Y = 0
FEATURE [Drawing::FeatureView] dim031
  Rotation = 0
  ViewResult = <g>  <circle cx ="176.955000" cy ="76.075000" r="0.500000" stroke="none" fill="rgb(0,0,255)" /> \n<line x1="164.516077" y1="60.363793" x2="176.955000" y2="76.075000" style="stroke:rgb(0,0,255);stroke-width:0.20" />\n<polygon points="176.815336,75.898595 175.541164,73.080974 174.953145,73.546522 174.365127,74.012069" style="fill:rgb(0,0,255);stroke:rgb(0,0,255);stroke-width:0" />\n<line x1="164.516077" y1="60.363793" x2="144.229884" y2="60.363793" style="stroke:rgb(0,0,255);stroke-width:0.20" />\n<text x="154.372980" y="59.363793" font-family="Verdana" font-size="3.6" fill="rgb(0,0,255)" text-anchor="middle"  >4 X R0.50</text> </g>
  Visible = true
  X = 0
  Y = 0
FEATURE [Drawing::FeatureView] centerLines002
  Rotation = 0
  ViewResult = <g transform="scale(0.450000,0.450000)" stroke="rgb(0,0,255)"  stroke-width="0.666667" > <path d="M 514.283333,249.855556 L 514.283333,245.411111 M 514.283333,240.966667 L 514.283333,227.633333 M 514.283333,223.188889 L 514.283333,218.744444 M 514.283333,214.300000 L 514.283333,200.966667 M 514.283333,196.522222 L 514.283333,192.077778 M 514.283333,187.633333 L 514.283333,174.300000 M 514.283333,169.855556 L 514.283333,165.411111 "/>\n<path d="M 514.283333,249.855556 L 513.575097,249.855556 "/>\n<path d="M 514.283333,249.855556 L 514.283333,245.411111 M 514.283333,240.966667 L 514.283333,227.633333 M 514.283333,223.188889 L 514.283333,218.744444 M 514.283333,214.300000 L 514.283333,200.966667 M 514.283333,196.522222 L 514.283333,192.077778 M 514.283333,187.633333 L 514.283333,179.339843 "/>\n<path d="M 514.283333,249.855556 L 509.838889,249.855556 M 505.394444,249.855556 L 492.061111,249.855556 M 487.616667,249.855556 L 483.172222,249.855556 M 478.727778,249.855556 L 465.394444,249.855556 M 460.950000,249.855556 L 456.505556,249.855556 M 452.061111,249.855556 L 448.954668,249.855556 "/> </g> 
  Visible = true
  X = 0
  Y = 0
FEATURE [Drawing::FeatureView] dimText008
  Rotation = 0
  ViewResult = <g> <text x="160.909225" y="120.823067" font-family="inherit" font-size="3" fill="rgb(0,0,0)" text-anchor="inherit"  >OVERSPRAY IS ALLOWED</text> </g>
  Visible = true
  X = 0
  Y = 0
FEATURE [Drawing::FeatureView] centerLines006
  Rotation = 0
  ViewResult = <g transform="scale(0.400000,0.400000)" stroke="rgb(0,0,255)"  stroke-width="0.750000" > <path d="M 277.500000,214.700000 L 277.500000,219.700000 M 277.500000,224.700000 L 277.500000,239.700000 M 277.500000,244.700000 L 277.500000,249.700000 M 277.500000,254.700000 L 277.500000,269.700000 M 277.500000,274.700000 L 277.500000,279.700000 "/>\n<path d="M 277.500000,214.700000 L 277.500000,219.700000 M 277.500000,224.700000 L 277.500000,239.700000 M 277.500000,244.700000 L 277.500000,249.700000 M 277.500000,254.700000 L 277.500000,269.700000 M 277.500000,274.700000 L 277.500000,279.700000 "/> </g> 
  Visible = true
  X = 0
  Y = 0
FEATURE [Drawing::FeatureView] dimText009
  Rotation = 0
  ViewResult = <g> <text x="105.348014" y="38.964334" font-family="inherit" font-size="3.6" fill="rgb(0,0,255)" text-anchor="inherit"  >INSTALL STANDOFF TOWARD INSIDE</text> </g>
  Visible = true
  X = 0
  Y = 0
FEATURE [Drawing::FeatureView] dim045
  Rotation = 0
  ViewResult = <g> <line x1="46.580000" y1="94.220000" x2="39.431425" y2="94.220000" style="stroke:rgb(0,0,255);stroke-width:0.20" />\n<line x1="46.580000" y1="105.540000" x2="39.431425" y2="105.540000" style="stroke:rgb(0,0,255);stroke-width:0.20" />\n<line x1="40.431425" y1="94.220000" x2="40.431425" y2="105.540000" style="stroke:rgb(0,0,255);stroke-width:0.20" />\n<polygon points="40.431425,94.220000 39.681425,97.220000 40.431425,97.220000 41.181425,97.220000" style="fill:rgb(0,0,255);stroke:rgb(0,0,255);stroke-width:0" />\n<polygon points="40.431425,105.540000 41.181425,102.540000 40.431425,102.540000 39.681425,102.540000" style="fill:rgb(0,0,255);stroke:rgb(0,0,255);stroke-width:0" />\n<text x="39.431425" y="99.880000" font-family="Verdana" font-size="3.6" fill="rgb(0,0,255)" text-anchor="middle" transform="rotate(-90.000000 39.431425,99.880000)" >29.0</text> </g> 
  Visible = true
  X = 0
  Y = 0
FEATURE [Drawing::FeatureView] dim024
  Rotation = 0
  ViewResult = <g> <line x1="180.390435" y1="75.850000" x2="180.390435" y2="70.000000" style="stroke:rgb(0,0,255);stroke-width:0.20" />\n<polygon points="180.390435,75.850000 179.640435,78.850000 180.390435,78.850000 181.140435,78.850000" style="fill:rgb(0,0,255);stroke:rgb(0,0,255);stroke-width:0" />\n<polygon points="180.390435,70.000000 181.140435,67.000000 180.390435,67.000000 179.640435,67.000000" style="fill:rgb(0,0,255);stroke:rgb(0,0,255);stroke-width:0" />\n<text x="181.008916" y="62.260470" font-family="Verdana" font-size="3.6" fill="rgb(0,0,255)" text-anchor="middle" transform="rotate(-90.000000 181.008916,62.260470)" >13.0</text> </g> 
  Visible = true
  X = 0
  Y = 0
FEATURE [Drawing::FeatureViewPart] Ortho025  label="Ortho_-1_0"
  Direction = (-1,0,0)
  HiddenWidth = 0.15
  LineWidth = 0.35
  Rotation = 270
  Scale = 0.3
  ShowHiddenLines = false
  ShowSmoothLines = false
  Tolerance = 0.05
  ViewResult = <blob: 6110 chars omitted>
  Visible = true
  X = 50
  Y = 30
FEATURE [Drawing::FeatureView] dim028
  Rotation = 0
  ViewResult = <g> <line x1="240.000000" y1="115.920000" x2="240.000000" y2="134.143497" style="stroke:rgb(0,0,255);stroke-width:0.20" />\n<line x1="197.362500" y1="111.195042" x2="197.362500" y2="134.143497" style="stroke:rgb(0,0,255);stroke-width:0.20" />\n<line x1="240.000000" y1="133.143497" x2="197.362500" y2="133.143497" style="stroke:rgb(0,0,255);stroke-width:0.20" />\n<polygon points="240.000000,133.143497 237.000000,132.393497 237.000000,133.143497 237.000000,133.893497" style="fill:rgb(0,0,255);stroke:rgb(0,0,255);stroke-width:0" />\n<polygon points="197.362500,133.143497 200.362500,133.893497 200.362500,133.143497 200.362500,132.393497" style="fill:rgb(0,0,255);stroke:rgb(0,0,255);stroke-width:0" />\n<text x="218.681250" y="132.143497" font-family="Verdana" font-size="3.6" fill="rgb(0,0,255)" text-anchor="middle" transform="rotate(0.000000 218.681250,132.143497)" >94.75</text> </g> 
  Visible = true
  X = 0
  Y = 0
FEATURE [Drawing::FeatureViewPart] Ortho023  label="Ortho_1_0"
  Direction = (0,1,0)
  HiddenWidth = 0.15
  LineWidth = 0.35
  Rotation = 90
  Scale = 0.3
  ShowHiddenLines = false
  ShowSmoothLines = false
  Tolerance = 0.05
  ViewResult = <blob: 7038 chars omitted>
  Visible = true
  X = 250
  Y = 30
FEATURE [Drawing::FeatureView] dimText005
  Rotation = 0
  ViewResult = <g> <text x="156.580673" y="105.579036" font-family="inherit" font-size="3" fill="rgb(0,0,0)" text-anchor="inherit"  >4. BREAK ALL CORNERS PRIOR TO POWDER COATING</text> </g>
  Visible = true
  X = 0
  Y = 0
FEATURE [Drawing::FeatureView] dim002
  Rotation = 0
  ViewResult = <g> <line x1="131.400000" y1="40.000000" x2="140.736959" y2="40.000000" style="stroke:rgb(0,0,255);stroke-width:0.20" />\n<line x1="131.400000" y1="160.000000" x2="140.736959" y2="160.000000" style="stroke:rgb(0,0,255);stroke-width:0.20" />\n<line x1="139.736959" y1="40.000000" x2="139.736959" y2="160.000000" style="stroke:rgb(0,0,255);stroke-width:0.20" />\n<polygon points="139.736959,40.000000 138.986959,43.000000 139.736959,43.000000 140.486959,43.000000" style="fill:rgb(0,0,255);stroke:rgb(0,0,255);stroke-width:0" />\n<polygon points="139.736959,160.000000 140.486959,157.000000 139.736959,157.000000 138.986959,157.000000" style="fill:rgb(0,0,255);stroke:rgb(0,0,255);stroke-width:0" />\n<text x="138.736959" y="100.000000" font-family="Verdana" font-size="3.6" fill="rgb(0,0,255)" text-anchor="middle" transform="rotate(-90.000000 138.736959,100.000000)" >480.0</text> </g> 
  Visible = true
  X = 0
  Y = 0
FEATURE [Drawing::FeatureView] dim046
  Rotation = 0
  ViewResult = <g> \n  <line x1="53.680000" y1="107.080000" x2="32.178869" y2="107.080000" style="stroke:rgb(0,0,255);stroke-width:0.20" />\n<line x1="53.680000" y1="92.680000" x2="32.178869" y2="92.680000" style="stroke:rgb(0,0,255);stroke-width:0.20" />\n<line x1="33.178869" y1="107.080000" x2="33.178869" y2="92.680000" style="stroke:rgb(0,0,255);stroke-width:0.20" /> \n  <polygon points="33.178869,92.680000 32.428869,95.680000 33.178869,95.680000 33.928869,95.680000" style="fill:rgb(0,0,255);stroke:rgb(0,0,255);stroke-width:0" /><polygon points="33.178869,107.080000 33.928869,104.080000 33.178869,104.080000 32.428869,104.080000" style="fill:rgb(0,0,255);stroke:rgb(0,0,255);stroke-width:0" /> \n  <text x="32.178869" y="99.880000" font-family="Verdana" font-size="3.6" fill="rgb(0,0,255)" text-anchor="middle" transform="rotate(-90.000000 32.178869,99.880000)" >36.0</text> </g>
  Visible = true
  X = 0
  Y = 0
FEATURE [Drawing::FeatureView] dim013
  Rotation = 0
  ViewResult = <g> <line x1="23.350000" y1="115.270000" x2="14.861821" y2="115.270000" style="stroke:rgb(0,0,255);stroke-width:0.20" />\n<line x1="25.442287" y1="111.085000" x2="14.861821" y2="111.085000" style="stroke:rgb(0,0,255);stroke-width:0.20" />\n<line x1="15.861821" y1="115.270000" x2="15.861821" y2="111.085000" style="stroke:rgb(0,0,255);stroke-width:0.20" />\n<polygon points="15.861821,115.270000 15.111821,118.270000 15.861821,118.270000 16.611821,118.270000" style="fill:rgb(0,0,255);stroke:rgb(0,0,255);stroke-width:0" />\n<polygon points="15.861821,111.085000 16.611821,108.085000 15.861821,108.085000 15.111821,108.085000" style="fill:rgb(0,0,255);stroke:rgb(0,0,255);stroke-width:0" />\n<text x="16.755351" y="124.761063" font-family="Verdana" font-size="3.6" fill="rgb(0,0,255)" text-anchor="middle" transform="rotate(-90.000000 16.755351,124.761063)" >8X 9.3</text> </g> 
  Visible = true
  X = 0
  Y = 0
FEATURE [Drawing::FeatureView] centerLines004
  Rotation = 0
  ViewResult = <g transform="scale(0.400000,0.400000)" stroke="rgb(0,0,255)"  stroke-width="0.750000" > <path d="M 187.500000,214.700000 L 187.500000,219.700000 M 187.500000,224.700000 L 187.500000,239.700000 M 187.500000,244.700000 L 187.500000,249.700000 M 187.500000,254.700000 L 187.500000,269.700000 M 187.500000,274.700000 L 187.500000,279.700000 M 187.500000,284.700000 L 187.500000,284.945538 "/>\n<path d="M 187.500000,214.700000 L 190.026719,214.700000 "/>\n<path d="M 187.500000,214.700000 L 187.500000,217.065346 "/>\n<path d="M 187.500000,214.700000 L 192.500000,214.700000 M 197.500000,214.700000 L 212.500000,214.700000 M 217.500000,214.700000 L 222.500000,214.700000 M 227.500000,214.700000 L 242.500000,214.700000 M 247.500000,214.700000 L 252.500000,214.700000 M 257.500000,214.700000 L 272.500000,214.700000 M 277.500000,214.700000 L 282.500000,214.700000 M 287.500000,214.700000 L 302.500000,214.700000 M 307.500000,214.700000 L 312.500000,214.700000 M 317.500000,214.700000 L 332.500000,214.700000 M 337.500000,214.700000 L 342.500000,214.700000 M 347.500000,214.700000 L 362.500000,214.700000 "/> </g> 
  Visible = true
  X = 0
  Y = 0
FEATURE [Drawing::FeatureView] dim042
  Rotation = 0
  ViewResult = <g> <line x1="114.000188" y1="113.880000" x2="129.850311" y2="113.880000" style="stroke:rgb(0,0,255);stroke-width:0.20" />\n<line x1="128.850311" y1="120.000000" x2="128.850311" y2="113.880000" style="stroke:rgb(0,0,255);stroke-width:0.20" />\n<polygon points="128.850311,120.000000 128.100311,123.000000 128.850311,123.000000 129.600311,123.000000" style="fill:rgb(0,0,255);stroke:rgb(0,0,255);stroke-width:0" />\n<polygon points="128.850311,113.880000 129.600311,110.880000 128.850311,110.880000 128.100311,110.880000" style="fill:rgb(0,0,255);stroke:rgb(0,0,255);stroke-width:0" />\n<text x="129.881113" y="128.231829" font-family="Verdana" font-size="3.6" fill="rgb(0,0,255)" text-anchor="middle" transform="rotate(-90.000000 129.881113,128.231829)" >15.3</text> </g> 
  Visible = true
  X = 0
  Y = 0
FEATURE [Drawing::FeatureView] dim044
  Rotation = 0
  ViewResult = <g> <line x1="48.580000" y1="92.220000" x2="48.580000" y2="73.566152" style="stroke:rgb(0,0,255);stroke-width:0.20" />\n<line x1="55.000000" y1="89.999989" x2="55.000000" y2="73.566152" style="stroke:rgb(0,0,255);stroke-width:0.20" />\n<line x1="48.580000" y1="74.566152" x2="55.000000" y2="74.566152" style="stroke:rgb(0,0,255);stroke-width:0.20" />\n<polygon points="48.580000,74.566152 45.580000,73.816152 45.580000,74.566152 45.580000,75.316152" style="fill:rgb(0,0,255);stroke:rgb(0,0,255);stroke-width:0" />\n<polygon points="55.000000,74.566152 58.000000,75.316152 58.000000,74.566152 58.000000,73.816152" style="fill:rgb(0,0,255);stroke:rgb(0,0,255);stroke-width:0" />\n<text x="38.685129" y="75.801942" font-family="Verdana" font-size="3.6" fill="rgb(0,0,255)" text-anchor="middle"  >16.5</text> </g> 
  Visible = true
  X = 0
  Y = 0
FEATURE [Drawing::FeatureView] dim005
  Rotation = 0
  ViewResult = <g> <line x1="43.750000" y1="38.750000" x2="43.750000" y2="33.216154" style="stroke:rgb(0,0,255);stroke-width:0.20" />\n<line x1="78.750000" y1="38.750000" x2="78.750000" y2="33.216154" style="stroke:rgb(0,0,255);stroke-width:0.20" />\n<line x1="43.750000" y1="34.216154" x2="78.750000" y2="34.216154" style="stroke:rgb(0,0,255);stroke-width:0.20" />\n<polygon points="43.750000,34.216154 46.750000,34.966154 46.750000,34.216154 46.750000,33.466154" style="fill:rgb(0,0,255);stroke:rgb(0,0,255);stroke-width:0" />\n<polygon points="78.750000,34.216154 75.750000,33.466154 75.750000,34.216154 75.750000,34.966154" style="fill:rgb(0,0,255);stroke:rgb(0,0,255);stroke-width:0" />\n<text x="61.250000" y="33.216154" font-family="Verdana" font-size="3.6" fill="rgb(0,0,255)" text-anchor="middle"  >140.0</text> </g> 
  Visible = true
  X = 0
  Y = 0
FEATURE [Drawing::FeatureView] dimText010
  Rotation = 0
  ViewResult = <g> <text x="162.494967" y="167.722687" font-family="inherit" font-size="3.6" fill="rgb(0,0,255)" text-anchor="inherit"  >INSTALL STANDOFF TOWARD OUTSIDE</text> </g>
  Visible = true
  X = 0
  Y = 0
FEATURE [Drawing::FeatureView] dim011
  Rotation = 0
  ViewResult = <g> \n  <line x1="25.442500" y1="91.150000" x2="14.882830" y2="91.150000" style="stroke:rgb(0,0,255);stroke-width:0.20" />\n<line x1="25.442500" y1="94.120000" x2="14.882830" y2="94.120000" style="stroke:rgb(0,0,255);stroke-width:0.20" />\n<line x1="15.882830" y1="91.150000" x2="15.882830" y2="94.120000" style="stroke:rgb(0,0,255);stroke-width:0.20" /> \n  <polygon points="15.882830,94.120000 15.132830,97.120000 15.882830,97.120000 16.632830,97.120000" style="fill:rgb(0,0,255);stroke:rgb(0,0,255);stroke-width:0" /><polygon points="15.882830,91.150000 16.632830,88.150000 15.882830,88.150000 15.132830,88.150000" style="fill:rgb(0,0,255);stroke:rgb(0,0,255);stroke-width:0" /> \n  <text x="13.886449" y="92.720976" font-family="Verdana" font-size="3.6" fill="rgb(0,0,255)" text-anchor="middle" transform="rotate(-90.000000 13.886449,92.720976)" >4X 6.6</text> </g>
  Visible = true
  X = 0
  Y = 0
FEATURE [Drawing::FeatureView] dim052
  Rotation = 0
  ViewResult = <g>  <circle cx ="180.700000" cy ="102.284000" r="0.500000" stroke="none" fill="rgb(0,0,255)" /> \n<line x1="152.186533" y1="45.527110" x2="181.042072" y2="102.964904" style="stroke:rgb(0,0,255);stroke-width:0.20" />\n<polygon points="180.357928,101.603096 179.681369,98.585685 179.011188,98.922370 178.341006,99.259055" style="fill:rgb(0,0,255);stroke:rgb(0,0,255);stroke-width:0" />\n<polygon points="181.042072,102.964904 181.718631,105.982315 182.388812,105.645630 183.058994,105.308945" style="fill:rgb(0,0,255);stroke:rgb(0,0,255);stroke-width:0" />\n<line x1="152.186533" y1="45.527110" x2="109.379597" y2="45.527110" style="stroke:rgb(0,0,255);stroke-width:0.20" />\n<text x="124.685869" y="38.840638" font-family="Verdana" font-size="3.6" fill="rgb(0,0,255)" text-anchor="middle"  >4 X Ø3.81 THRU</text> </g>
  Visible = true
  X = 0
  Y = 0
FEATURE [Drawing::FeatureView] centerLines001
  Rotation = 0
  ViewResult = <g transform="scale(0.450000,0.450000)" stroke="rgb(0,0,255)"  stroke-width="0.666667" > <path d="M 449.283333,161.855556 L 449.283333,166.300000 M 449.283333,170.744444 L 449.283333,184.077778 M 449.283333,188.522222 L 449.283333,192.966667 M 449.283333,197.411111 L 449.283333,210.744444 M 449.283333,215.188889 L 449.283333,219.633333 M 449.283333,224.077778 L 449.283333,237.411111 M 449.283333,241.855556 L 449.283333,246.300000 "/>\n<path d="M 449.283333,161.855556 L 448.954668,161.855556 "/>\n<path d="M 449.283333,161.855556 L 449.283333,166.300000 M 449.283333,170.744444 L 449.283333,184.077778 M 449.283333,188.522222 L 449.283333,192.966667 M 449.283333,197.411111 L 449.283333,210.744444 M 449.283333,215.188889 L 449.283333,219.633333 M 449.283333,224.077778 L 449.283333,237.411111 M 449.283333,241.855556 L 449.283333,246.300000 "/>\n<path d="M 449.283333,161.855556 L 453.727778,161.855556 M 458.172222,161.855556 L 471.505556,161.855556 M 475.950000,161.855556 L 480.394444,161.855556 M 484.838889,161.855556 L 498.172222,161.855556 M 502.616667,161.855556 L 507.061111,161.855556 M 511.505556,161.855556 L 514.059145,161.855556 "/> </g> 
  Visible = true
  X = 0
  Y = 0
FEATURE [Drawing::FeatureView] dim032
  Rotation = 0
  ViewResult = <g>  <circle cx ="202.177500" cy ="72.835000" r="0.500000" stroke="none" fill="rgb(0,0,255)" /> \n<line x1="167.940509" y1="41.037603" x2="202.177500" y2="72.835000" style="stroke:rgb(0,0,255);stroke-width:0.20" />\n<polygon points="201.481772,72.188847 199.793970,69.597743 199.283581,70.147290 198.773192,70.696838" style="fill:rgb(0,0,255);stroke:rgb(0,0,255);stroke-width:0" />\n<line x1="167.940509" y1="41.037603" x2="106.906876" y2="41.037603" style="stroke:rgb(0,0,255);stroke-width:0.20" />\n<text x="138.333693" y="33.810321" font-family="Verdana" font-size="3.6" fill="rgb(0,0,255)" text-anchor="middle"  >4 X TSO-M25-1400Z1 BLIND INSERTS</text> </g>
  Visible = true
  X = 0
  Y = 0
FEATURE [Drawing::FeatureView] dim027
  Rotation = 0
  ViewResult = <g> <line x1="228.750000" y1="112.770000" x2="228.750000" y2="126.882774" style="stroke:rgb(0,0,255);stroke-width:0.20" />\n<line x1="204.855000" y1="112.770000" x2="204.855000" y2="126.882774" style="stroke:rgb(0,0,255);stroke-width:0.20" />\n<line x1="228.750000" y1="125.882774" x2="204.855000" y2="125.882774" style="stroke:rgb(0,0,255);stroke-width:0.20" />\n<polygon points="228.750000,125.882774 225.750000,125.132774 225.750000,125.882774 225.750000,126.632774" style="fill:rgb(0,0,255);stroke:rgb(0,0,255);stroke-width:0" />\n<polygon points="204.855000,125.882774 207.855000,126.632774 207.855000,125.882774 207.855000,125.132774" style="fill:rgb(0,0,255);stroke:rgb(0,0,255);stroke-width:0" />\n<text x="216.802500" y="124.882774" font-family="Verdana" font-size="3.6" fill="rgb(0,0,255)" text-anchor="middle" transform="rotate(0.000000 216.802500,124.882774)" >53.1</text> </g> 
  Visible = true
  X = 0
  Y = 0
FEATURE [Drawing::FeatureView] centerLines003
  Rotation = 0
  ViewResult = <g transform="scale(0.450000,0.450000)" stroke="rgb(0,0,255)"  stroke-width="0.666667" > <path d="M 438.583333,242.655556 L 438.583333,247.100000 "/>\n<path d="M 438.583333,242.655556 L 434.138889,242.655556 "/>\n<path d="M 438.583333,242.655556 L 438.583333,238.211111 "/>\n<path d="M 438.583333,242.655556 L 442.420018,242.655556 "/> </g> 
  Visible = true
  X = 0
  Y = 0
FEATURE [Drawing::FeatureView] dimText007
  Rotation = 0
  ViewResult = <g> <text x="161.097423" y="115.929921" font-family="inherit" font-size="3" fill="rgb(0,0,0)" text-anchor="inherit"  >SEE PAGE 6 FOR FURTHER MASKING DETAILS AND WHERE</text> </g>
  Visible = true
  X = 0
  Y = 0
FEATURE [Drawing::FeatureView] dim004
  Rotation = 0
  ViewResult = <g> <line x1="152.500000" y1="38.750000" x2="152.500000" y2="30.104935" style="stroke:rgb(0,0,255);stroke-width:0.20" />\n<line x1="195.000000" y1="38.750000" x2="195.000000" y2="30.104935" style="stroke:rgb(0,0,255);stroke-width:0.20" />\n<line x1="152.500000" y1="31.104935" x2="195.000000" y2="31.104935" style="stroke:rgb(0,0,255);stroke-width:0.20" />\n<polygon points="152.500000,31.104935 155.500000,31.854935 155.500000,31.104935 155.500000,30.354935" style="fill:rgb(0,0,255);stroke:rgb(0,0,255);stroke-width:0" />\n<polygon points="195.000000,31.104935 192.000000,30.354935 192.000000,31.104935 192.000000,31.854935" style="fill:rgb(0,0,255);stroke:rgb(0,0,255);stroke-width:0" />\n<text x="173.750000" y="30.104935" font-family="Verdana" font-size="3.6" fill="rgb(0,0,255)" text-anchor="middle"  >170.0</text> </g> 
  Visible = true
  X = 0
  Y = 0
FEATURE [Drawing::FeatureView] dim033
  Rotation = 0
  ViewResult = <g> <line x1="48.580000" y1="107.540000" x2="48.580000" y2="131.823696" style="stroke:rgb(0,0,255);stroke-width:0.20" />\n<line x1="61.420000" y1="107.540000" x2="61.420000" y2="131.823696" style="stroke:rgb(0,0,255);stroke-width:0.20" />\n<line x1="48.580000" y1="130.823696" x2="61.420000" y2="130.823696" style="stroke:rgb(0,0,255);stroke-width:0.20" />\n<polygon points="48.580000,130.823696 51.580000,131.573696 51.580000,130.823696 51.580000,130.073696" style="fill:rgb(0,0,255);stroke:rgb(0,0,255);stroke-width:0" />\n<polygon points="61.420000,130.823696 58.420000,130.073696 58.420000,130.823696 58.420000,131.573696" style="fill:rgb(0,0,255);stroke:rgb(0,0,255);stroke-width:0" />\n<text x="55.000000" y="129.823696" font-family="Verdana" font-size="3.6" fill="rgb(0,0,255)" text-anchor="middle"  >33.0</text> </g> 
  Visible = true
  X = 0
  Y = 0
FEATURE [Drawing::FeatureView] dim003
  Rotation = 0
  ViewResult = <g> <line x1="105.000000" y1="39.250000" x2="105.000000" y2="30.617251" style="stroke:rgb(0,0,255);stroke-width:0.20" />\n<line x1="130.150000" y1="38.750000" x2="130.150000" y2="30.617251" style="stroke:rgb(0,0,255);stroke-width:0.20" />\n<line x1="105.000000" y1="31.617251" x2="130.150000" y2="31.617251" style="stroke:rgb(0,0,255);stroke-width:0.20" />\n<polygon points="105.000000,31.617251 108.000000,32.367251 108.000000,31.617251 108.000000,30.867251" style="fill:rgb(0,0,255);stroke:rgb(0,0,255);stroke-width:0" />\n<polygon points="130.150000,31.617251 127.150000,30.867251 127.150000,31.617251 127.150000,32.367251" style="fill:rgb(0,0,255);stroke:rgb(0,0,255);stroke-width:0" />\n<text x="117.575000" y="30.617251" font-family="Verdana" font-size="3.6" fill="rgb(0,0,255)" text-anchor="middle" transform="rotate(0.000000 117.575000,30.617251)" >100.6</text> </g> 
  Visible = true
  X = 0
  Y = 0
FEATURE [Drawing::FeatureView] dim029
  Rotation = 0
  ViewResult = <g> <line x1="190.500000" y1="88.200000" x2="190.500000" y2="141.222701" style="stroke:rgb(0,0,255);stroke-width:0.20" />\n<line x1="240.000000" y1="115.920000" x2="240.000000" y2="141.222701" style="stroke:rgb(0,0,255);stroke-width:0.20" />\n<line x1="190.500000" y1="140.222701" x2="240.000000" y2="140.222701" style="stroke:rgb(0,0,255);stroke-width:0.20" />\n<polygon points="190.500000,140.222701 193.500000,140.972701 193.500000,140.222701 193.500000,139.472701" style="fill:rgb(0,0,255);stroke:rgb(0,0,255);stroke-width:0" />\n<polygon points="240.000000,140.222701 237.000000,139.472701 237.000000,140.222701 237.000000,140.972701" style="fill:rgb(0,0,255);stroke:rgb(0,0,255);stroke-width:0" />\n<text x="215.250000" y="139.222701" font-family="Verdana" font-size="3.6" fill="rgb(0,0,255)" text-anchor="middle"  >110.0</text> </g> 
  Visible = true
  X = 0
  Y = 0
FEATURE [Drawing::FeatureView] centerLines005
  Rotation = 0
  ViewResult = <g transform="scale(0.400000,0.400000)" stroke="rgb(0,0,255)"  stroke-width="0.750000" > <path d="M 367.500000,284.700000 L 367.500000,279.700000 M 367.500000,274.700000 L 367.500000,259.700000 M 367.500000,254.700000 L 367.500000,249.700000 M 367.500000,244.700000 L 367.500000,229.700000 M 367.500000,224.700000 L 367.500000,219.700000 M 367.500000,214.700000 L 367.500000,214.229127 "/>\n<path d="M 367.500000,284.700000 L 367.384990,284.700000 "/>\n<path d="M 367.500000,284.700000 L 367.500000,284.189212 "/>\n<path d="M 367.500000,284.700000 L 362.500000,284.700000 M 357.500000,284.700000 L 342.500000,284.700000 M 337.500000,284.700000 L 332.500000,284.700000 M 327.500000,284.700000 L 312.500000,284.700000 M 307.500000,284.700000 L 302.500000,284.700000 M 297.500000,284.700000 L 282.500000,284.700000 M 277.500000,284.700000 L 272.500000,284.700000 M 267.500000,284.700000 L 252.500000,284.700000 M 247.500000,284.700000 L 242.500000,284.700000 M 237.500000,284.700000 L 222.500000,284.700000 M 217.500000,284.700000 L 212.500000,284.700000 M 207.500000,284.700000 L 192.500000,284.700000 M 187.500000,284.700000 L 187.190499,284.700000 "/> </g> 
  Visible = true
  X = 0
  Y = 0
FEATURE [Drawing::FeatureView] dimText004
  Rotation = 0
  ViewResult = <g> <text x="156.392475" y="100.309494" font-family="inherit" font-size="3" fill="rgb(0,0,0)" text-anchor="inherit"  >3. MATERIAL: 5052 H32 AL, 2.03 MM THICK</text> </g>
  Visible = true
  X = 0
  Y = 0
FEATURE [Drawing::FeatureView] dim001
  Rotation = 0
  ViewResult = <g> <line x1="40.000000" y1="160.750000" x2="40.000000" y2="170.509742" style="stroke:rgb(0,0,255);stroke-width:0.20" />\n<line x1="43.000000" y1="159.000000" x2="43.000000" y2="170.509742" style="stroke:rgb(0,0,255);stroke-width:0.20" />\n<line x1="40.000000" y1="169.509742" x2="43.000000" y2="169.509742" style="stroke:rgb(0,0,255);stroke-width:0.20" />\n<polygon points="40.000000,169.509742 37.000000,168.759742 37.000000,169.509742 37.000000,170.259742" style="fill:rgb(0,0,255);stroke:rgb(0,0,255);stroke-width:0" />\n<polygon points="43.000000,169.509742 46.000000,170.259742 46.000000,169.509742 46.000000,168.759742" style="fill:rgb(0,0,255);stroke:rgb(0,0,255);stroke-width:0" />\n<text x="51.761957" y="170.462152" font-family="Verdana" font-size="3.6" fill="rgb(0,0,255)" text-anchor="middle"  >12.0</text> </g> 
  Visible = true
  X = 0
  Y = 0
FEATURE [Drawing::FeatureView] dim050
  Rotation = 0
  ViewResult = <g>  <circle cx ="55.000000" cy ="92.680000" r="0.500000" stroke="none" fill="rgb(0,0,255)" /> \n<line x1="79.028190" y1="20.472883" x2="54.785294" y2="93.325214" style="stroke:rgb(0,0,255);stroke-width:0.20" />\n<polygon points="55.214706,92.034786 56.873573,89.425062 56.161940,89.188253 55.450307,88.951445" style="fill:rgb(0,0,255);stroke:rgb(0,0,255);stroke-width:0" />\n<polygon points="54.785294,93.325214 53.126427,95.934938 53.838060,96.171747 54.549693,96.408555" style="fill:rgb(0,0,255);stroke:rgb(0,0,255);stroke-width:0" />\n<line x1="79.028190" y1="20.472883" x2="120.832958" y2="20.472883" style="stroke:rgb(0,0,255);stroke-width:0.20" />\n<text x="101.430964" y="13.359200" font-family="Verdana" font-size="3.6" fill="rgb(0,0,255)" text-anchor="middle"  >2 X S-M3-2-Z1 PEM NUT</text> </g>
  Visible = true
  X = 0
  Y = 0
FEATURE [Drawing::FeatureView] dim038
  Rotation = 0
  ViewResult = <g> \n  <line x1="75.000000" y1="83.880000" x2="75.000000" y2="73.990582" style="stroke:rgb(0,0,255);stroke-width:0.20" />\n<line x1="111.000000" y1="83.880000" x2="111.000000" y2="73.990582" style="stroke:rgb(0,0,255);stroke-width:0.20" />\n<line x1="75.000000" y1="74.990582" x2="111.000000" y2="74.990582" style="stroke:rgb(0,0,255);stroke-width:0.20" /> \n  <polygon points="111.000000,74.990582 108.000000,74.240582 108.000000,74.990582 108.000000,75.740582" style="fill:rgb(0,0,255);stroke:rgb(0,0,255);stroke-width:0" /><polygon points="75.000000,74.990582 78.000000,75.740582 78.000000,74.990582 78.000000,74.240582" style="fill:rgb(0,0,255);stroke:rgb(0,0,255);stroke-width:0" /> \n  <text x="93.000000" y="73.990582" font-family="Verdana" font-size="3.6" fill="rgb(0,0,255)" text-anchor="middle"  >90.0</text> </g>
  Visible = true
  X = 0
  Y = 0
FEATURE [Drawing::FeatureView] dimText006
  Rotation = 0
  ViewResult = <g> <text x="156.957069" y="110.848577" font-family="inherit" font-size="3" fill="rgb(0,0,0)" text-anchor="inherit"  >5. MASK ALL THREADS PRIOR TO POWDER COATING AND</text> </g>
  Visible = true
  X = 0
  Y = 0
FEATURE [Drawing::FeatureView] dim021
  Rotation = 0
  ViewResult = <g> <line x1="43.000000" y1="120.000000" x2="43.000000" y2="126.465283" style="stroke:rgb(0,0,255);stroke-width:0.20" />\n<line x1="48.580000" y1="107.540000" x2="48.580000" y2="126.465283" style="stroke:rgb(0,0,255);stroke-width:0.20" />\n<line x1="43.000000" y1="125.465283" x2="48.580000" y2="125.465283" style="stroke:rgb(0,0,255);stroke-width:0.20" />\n<polygon points="43.000000,125.465283 40.000000,124.715283 40.000000,125.465283 40.000000,126.215283" style="fill:rgb(0,0,255);stroke:rgb(0,0,255);stroke-width:0" />\n<polygon points="48.580000,125.465283 51.580000,126.215283 51.580000,125.465283 51.580000,124.715283" style="fill:rgb(0,0,255);stroke:rgb(0,0,255);stroke-width:0" />\n<text x="33.672881" y="126.273304" font-family="Verdana" font-size="3.6" fill="rgb(0,0,255)" text-anchor="middle"  >14.0</text> </g> 
  Visible = true
  X = 0
  Y = 0
FEATURE [Drawing::FeatureView] dim041
  Rotation = 0
  ViewResult = <g> <line x1="135.378726" y1="111.880000" x2="135.378726" y2="120.000000" style="stroke:rgb(0,0,255);stroke-width:0.20" />\n<polygon points="135.378726,111.880000 134.628726,114.880000 135.378726,114.880000 136.128726,114.880000" style="fill:rgb(0,0,255);stroke:rgb(0,0,255);stroke-width:0" />\n<polygon points="135.378726,120.000000 136.128726,117.000000 135.378726,117.000000 134.628726,117.000000" style="fill:rgb(0,0,255);stroke:rgb(0,0,255);stroke-width:0" />\n<text x="136.478249" y="125.964064" font-family="Verdana" font-size="3.6" fill="rgb(0,0,255)" text-anchor="middle" transform="rotate(-90.000000 136.478249,125.964064)" >20.3</text> </g> 
  Visible = true
  X = 0
  Y = 0
FEATURE [Drawing::FeatureView] dim037
  Rotation = 0
  ViewResult = <g>  <circle cx ="81.000000" cy ="107.880000" r="0.500000" stroke="none" fill="rgb(0,0,255)" /> \n<line x1="85.613873" y1="135.149659" x2="81.000000" y2="107.880000" style="stroke:rgb(0,0,255);stroke-width:0.20" />\n<polygon points="81.667294,111.823947 81.906313,108.740869 81.166823,108.865987 80.427333,108.991104" style="fill:rgb(0,0,255);stroke:rgb(0,0,255);stroke-width:0" />\n<line x1="85.613873" y1="135.149659" x2="107.232092" y2="135.149659" style="stroke:rgb(0,0,255);stroke-width:0.20" />\n<text x="96.422982" y="134.149659" font-family="Verdana" font-size="3.6" fill="rgb(0,0,255)" text-anchor="middle"  >2 X R10.0</text> </g>
  Visible = true
  X = 0
  Y = 0
FEATURE [Drawing::FeatureView] dim010
  Rotation = 0
  ViewResult = <g> \n  <line x1="28.367500" y1="74.185000" x2="14.945857" y2="74.185000" style="stroke:rgb(0,0,255);stroke-width:0.20" />\n<line x1="28.367500" y1="84.504985" x2="14.945857" y2="84.504985" style="stroke:rgb(0,0,255);stroke-width:0.20" />\n<line x1="15.945857" y1="74.185000" x2="15.945857" y2="84.504985" style="stroke:rgb(0,0,255);stroke-width:0.20" /> \n  <polygon points="15.945857,84.504985 16.695857,81.504985 15.945857,81.504985 15.195857,81.504985" style="fill:rgb(0,0,255);stroke:rgb(0,0,255);stroke-width:0" /><polygon points="15.945857,74.185000 15.195857,77.185000 15.945857,77.185000 16.695857,77.185000" style="fill:rgb(0,0,255);stroke:rgb(0,0,255);stroke-width:0" /> \n  <text x="13.886449" y="75.796866" font-family="Verdana" font-size="3.6" fill="rgb(0,0,255)" text-anchor="middle" transform="rotate(-90.000000 13.886449,75.796866)" >4X 22.9</text> </g>
  Visible = true
  X = 0
  Y = 0
FEATURE [Drawing::FeatureView] centerLines008
  Rotation = 0
  ViewResult = <g transform="scale(0.400000,0.400000)" stroke="rgb(0,0,255)"  stroke-width="0.750000" > <path d="M 577.500000,285.450000 L 577.500000,280.450000 M 577.500000,275.450000 L 577.500000,260.450000 M 577.500000,255.450000 L 577.500000,250.450000 M 577.500000,245.450000 L 577.500000,230.450000 M 577.500000,225.450000 L 577.500000,220.450000 M 577.500000,215.450000 L 577.500000,213.259195 "/>\n<path d="M 577.500000,285.450000 L 577.738545,285.450000 "/>\n<path d="M 577.500000,285.450000 L 577.500000,285.737494 "/>\n<path d="M 577.500000,285.450000 L 572.500000,285.450000 M 567.500000,285.450000 L 552.500000,285.450000 M 547.500000,285.450000 L 542.500000,285.450000 M 537.500000,285.450000 L 522.500000,285.450000 M 517.500000,285.450000 L 512.500000,285.450000 M 507.500000,285.450000 L 505.558510,285.450000 "/> </g> 
  Visible = true
  X = 0
  Y = 0
FEATURE [Drawing::FeatureView] dimText003
  Rotation = 0
  ViewResult = <g> <text x="156.392475" y="94.663556" font-family="inherit" font-size="3" fill="rgb(0,0,0)" text-anchor="inherit"  >2. 3D MODEL GOVERNS DIMENSIONS NOT SHOWN ON PRINT ⌓ 1mm</text> </g>
  Visible = true
  X = 0
  Y = 0
FEATURE [Drawing::FeatureView] dim030
  Rotation = 0
  ViewResult = <g> <line x1="176.730000" y1="88.200000" x2="176.730000" y2="148.483424" style="stroke:rgb(0,0,255);stroke-width:0.20" />\n<line x1="240.000000" y1="115.920000" x2="240.000000" y2="148.483424" style="stroke:rgb(0,0,255);stroke-width:0.20" />\n<line x1="176.730000" y1="147.483424" x2="240.000000" y2="147.483424" style="stroke:rgb(0,0,255);stroke-width:0.20" />\n<polygon points="176.730000,147.483424 179.730000,148.233424 179.730000,147.483424 179.730000,146.733424" style="fill:rgb(0,0,255);stroke:rgb(0,0,255);stroke-width:0" />\n<polygon points="240.000000,147.483424 237.000000,146.733424 237.000000,147.483424 237.000000,148.233424" style="fill:rgb(0,0,255);stroke:rgb(0,0,255);stroke-width:0" />\n<text x="208.365000" y="146.483424" font-family="Verdana" font-size="3.6" fill="rgb(0,0,255)" text-anchor="middle" transform="rotate(0.000000 208.365000,146.483424)" >140.6</text> </g> 
  Visible = true
  X = 0
  Y = 0
FEATURE [Drawing::FeatureView] centerLines009
  Rotation = 0
  ViewResult = <g transform="scale(0.400000,0.400000)" stroke="rgb(0,0,255)"  stroke-width="0.750000" > <path d="M 423.210000,255.710000 L 423.210000,255.389070 "/>\n<path d="M 423.210000,255.710000 L 428.210000,255.710000 M 433.210000,255.710000 L 448.210000,255.710000 "/>\n<path d="M 423.210000,255.710000 L 423.210000,260.710000 M 423.210000,265.710000 L 423.210000,280.710000 "/>\n<path d="M 423.210000,255.710000 L 423.162912,255.710000 "/> </g> 
  Visible = true
  X = 0
  Y = 0
FEATURE [Drawing::FeatureView] dim012
  Rotation = 0
  ViewResult = <g> \n  <line x1="25.442500" y1="94.120000" x2="14.882830" y2="94.120000" style="stroke:rgb(0,0,255);stroke-width:0.20" />\n<line x1="25.442500" y1="111.085000" x2="14.882830" y2="111.085000" style="stroke:rgb(0,0,255);stroke-width:0.20" />\n<line x1="15.882830" y1="94.120000" x2="15.882830" y2="111.085000" style="stroke:rgb(0,0,255);stroke-width:0.20" /> \n  <polygon points="15.882830,111.085000 16.632830,108.085000 15.882830,108.085000 15.132830,108.085000" style="fill:rgb(0,0,255);stroke:rgb(0,0,255);stroke-width:0" /><polygon points="15.882830,94.120000 15.132830,97.120000 15.882830,97.120000 16.632830,97.120000" style="fill:rgb(0,0,255);stroke:rgb(0,0,255);stroke-width:0" /> \n  <text x="20.540372" y="102.557210" font-family="Verdana" font-size="3.6" fill="rgb(0,0,255)" text-anchor="middle" transform="rotate(-90.000000 20.540372,102.557210)" >4X 37.7</text> </g>
  Visible = true
  X = 0
  Y = 0
FEATURE [Drawing::FeatureView] dim015
  Rotation = 0
  ViewResult = <g>  <circle cx ="197.362500" cy ="109.195000" r="0.500000" stroke="none" fill="rgb(0,0,255)" /> \n<line x1="178.004318" y1="123.481548" x2="199.715974" y2="107.458111" style="stroke:rgb(0,0,255);stroke-width:0.20" />\n<polygon points="195.009026,110.931889 192.149850,112.109859 192.595206,112.713314 193.040563,113.316769" style="fill:rgb(0,0,255);stroke:rgb(0,0,255);stroke-width:0" />\n<polygon points="199.715974,107.458111 202.575150,106.280141 202.129794,105.676686 201.684437,105.073231" style="fill:rgb(0,0,255);stroke:rgb(0,0,255);stroke-width:0" />\n<line x1="178.004318" y1="123.481548" x2="160.466359" y2="123.481548" style="stroke:rgb(0,0,255);stroke-width:0.20" />\n<text x="169.235338" y="122.481548" font-family="Verdana" font-size="3.6" fill="rgb(0,0,255)" text-anchor="middle"  >Ø13.0</text> </g>
  Visible = true
  X = 0
  Y = 0
FEATURE [Drawing::FeatureView] dimText011
  Rotation = 0
  ViewResult = <g> <text x="140.000000" y="15.000000" font-family="inherit" font-size="4" fill="rgb(0,0,0)" text-anchor="inherit"  >Version</text> </g>
  Visible = true
  X = 0
  Y = 0
FEATURE [Drawing::FeatureView] centerLines010
  Rotation = 0
  ViewResult = <g transform="scale(0.400000,0.400000)" stroke="rgb(0,0,255)"  stroke-width="0.750000" > <path d="M 451.750000,284.250000 L 451.750000,283.558506 "/>\n<path d="M 451.750000,284.250000 L 446.750000,284.250000 M 441.750000,284.250000 L 426.750000,284.250000 "/>\n<path d="M 451.750000,284.250000 L 451.750000,279.250000 M 451.750000,274.250000 L 451.750000,259.250000 "/>\n<path d="M 451.750000,284.250000 L 452.575117,284.250000 "/> </g> 
  Visible = true
  X = 0
  Y = 0
FEATURE [Drawing::FeatureView] dimText012
  Rotation = 0
  ViewResult = <g> <text x="180.000000" y="15.000000" font-family="inherit" font-size="4" fill="rgb(0,0,0)" text-anchor="inherit"  >Description</text> </g>
  Visible = true
  X = 0
  Y = 0
FEATURE [Drawing::FeatureView] dim040
  Rotation = 0
  ViewResult = <g> \n  <line x1="74.000000" y1="85.880000" x2="18.241646" y2="85.880000" style="stroke:rgb(0,0,255);stroke-width:0.20" />\n<line x1="74.000000" y1="113.880000" x2="18.241646" y2="113.880000" style="stroke:rgb(0,0,255);stroke-width:0.20" />\n<line x1="19.241646" y1="85.880000" x2="19.241646" y2="113.880000" style="stroke:rgb(0,0,255);stroke-width:0.20" /> \n  <polygon points="19.241646,113.880000 19.991646,110.880000 19.241646,110.880000 18.491646,110.880000" style="fill:rgb(0,0,255);stroke:rgb(0,0,255);stroke-width:0" /><polygon points="19.241646,85.880000 18.491646,88.880000 19.241646,88.880000 19.991646,88.880000" style="fill:rgb(0,0,255);stroke:rgb(0,0,255);stroke-width:0" /> \n  <text x="18.241646" y="99.880000" font-family="Verdana" font-size="3.6" fill="rgb(0,0,255)" text-anchor="middle" transform="rotate(-90.000000 18.241646,99.880000)" >70.0</text> </g>
  Visible = true
  X = 0
  Y = 0
FEATURE [Drawing::FeatureView] dim047
  Rotation = 0
  ViewResult = <g> <line x1="46.580000" y1="94.220000" x2="25.802005" y2="94.220000" style="stroke:rgb(0,0,255);stroke-width:0.20" />\n<line x1="53.679987" y1="92.680000" x2="25.802005" y2="92.680000" style="stroke:rgb(0,0,255);stroke-width:0.20" />\n<line x1="26.802005" y1="94.220000" x2="26.802005" y2="92.680000" style="stroke:rgb(0,0,255);stroke-width:0.20" />\n<polygon points="26.802005,94.220000 26.052005,97.220000 26.802005,97.220000 27.552005,97.220000" style="fill:rgb(0,0,255);stroke:rgb(0,0,255);stroke-width:0" />\n<polygon points="26.802005,92.680000 27.552005,89.680000 26.802005,89.680000 26.052005,89.680000" style="fill:rgb(0,0,255);stroke:rgb(0,0,255);stroke-width:0" />\n<text x="25.802005" y="93.450000" font-family="Verdana" font-size="3.6" fill="rgb(0,0,255)" text-anchor="middle" transform="rotate(-90.000000 25.802005,93.450000)" >3.85</text> </g> 
  Visible = true
  X = 0
  Y = 0
FEATURE [Drawing::FeatureView] dim023
  Rotation = 0
  ViewResult = <g> \n  <line x1="231.427500" y1="69.885500" x2="231.427500" y2="62.519315" style="stroke:rgb(0,0,255);stroke-width:0.20" />\n<line x1="202.177500" y1="69.885500" x2="202.177500" y2="62.519315" style="stroke:rgb(0,0,255);stroke-width:0.20" />\n<line x1="231.427500" y1="63.519315" x2="202.177500" y2="63.519315" style="stroke:rgb(0,0,255);stroke-width:0.20" /> \n  <polygon points="202.177500,63.519315 205.177500,64.269315 205.177500,63.519315 205.177500,62.769315" style="fill:rgb(0,0,255);stroke:rgb(0,0,255);stroke-width:0" /><polygon points="231.427500,63.519315 228.427500,62.769315 228.427500,63.519315 228.427500,64.269315" style="fill:rgb(0,0,255);stroke:rgb(0,0,255);stroke-width:0" /> \n  <text x="216.802500" y="62.519315" font-family="Verdana" font-size="3.6" fill="rgb(0,0,255)" text-anchor="middle"  >65.0</text> </g>
  Visible = true
  X = 0
  Y = 0
FEATURE [Drawing::FeatureView] dim054
  Rotation = 0
  ViewResult = <g> <line x1="235.000000" y1="78.960000" x2="235.000000" y2="73.965507" style="stroke:rgb(0,0,255);stroke-width:0.20" />\n<line x1="184.000000" y1="82.960000" x2="184.000000" y2="73.965507" style="stroke:rgb(0,0,255);stroke-width:0.20" />\n<line x1="235.000000" y1="74.965507" x2="184.000000" y2="74.965507" style="stroke:rgb(0,0,255);stroke-width:0.20" />\n<polygon points="235.000000,74.965507 232.000000,74.215507 232.000000,74.965507 232.000000,75.715507" style="fill:rgb(0,0,255);stroke:rgb(0,0,255);stroke-width:0" />\n<polygon points="184.000000,74.965507 187.000000,75.715507 187.000000,74.965507 187.000000,74.215507" style="fill:rgb(0,0,255);stroke:rgb(0,0,255);stroke-width:0" />\n<text x="209.500000" y="73.965507" font-family="Verdana" font-size="3.6" fill="rgb(0,0,255)" text-anchor="middle" transform="rotate(0.000000 209.500000,73.965507)" >127.5</text> </g> 
  Visible = true
  X = 0
  Y = 0
FEATURE [Drawing::FeatureView] dimText002
  Rotation = 0
  ViewResult = <g> <text x="156.204277" y="89.017618" font-family="inherit" font-size="3" fill="rgb(0,0,0)" text-anchor="inherit"  >1. ALL COMPONENTS RoHS COMPLIANT</text> </g>
  Visible = true
  X = 0
  Y = 0
FEATURE [Drawing::FeatureView] dim034
  Rotation = 0
  ViewResult = <g> <line x1="43.000000" y1="120.000000" x2="43.000000" y2="138.279968" style="stroke:rgb(0,0,255);stroke-width:0.20" />\n<line x1="75.000000" y1="114.880037" x2="75.000000" y2="138.279968" style="stroke:rgb(0,0,255);stroke-width:0.20" />\n<line x1="43.000000" y1="137.279968" x2="75.000000" y2="137.279968" style="stroke:rgb(0,0,255);stroke-width:0.20" />\n<polygon points="43.000000,137.279968 46.000000,138.029968 46.000000,137.279968 46.000000,136.529968" style="fill:rgb(0,0,255);stroke:rgb(0,0,255);stroke-width:0" />\n<polygon points="75.000000,137.279968 72.000000,136.529968 72.000000,137.279968 72.000000,138.029968" style="fill:rgb(0,0,255);stroke:rgb(0,0,255);stroke-width:0" />\n<text x="59.000000" y="136.279968" font-family="Verdana" font-size="3.6" fill="rgb(0,0,255)" text-anchor="middle"  >80.0</text> </g> 
  Visible = true
  X = 0
  Y = 0
FEATURE [Drawing::FeatureView] dim036
  Rotation = 0
  ViewResult = <g> \n  <line x1="81.000000" y1="105.880000" x2="81.000000" y2="144.664119" style="stroke:rgb(0,0,255);stroke-width:0.20" />\n<line x1="141.000000" y1="105.880000" x2="141.000000" y2="144.664119" style="stroke:rgb(0,0,255);stroke-width:0.20" />\n<line x1="81.000000" y1="143.664119" x2="141.000000" y2="143.664119" style="stroke:rgb(0,0,255);stroke-width:0.20" /> \n  <polygon points="141.000000,143.664119 138.000000,142.914119 138.000000,143.664119 138.000000,144.414119" style="fill:rgb(0,0,255);stroke:rgb(0,0,255);stroke-width:0" /><polygon points="81.000000,143.664119 84.000000,144.414119 84.000000,143.664119 84.000000,142.914119" style="fill:rgb(0,0,255);stroke:rgb(0,0,255);stroke-width:0" /> \n  <text x="111.000000" y="142.664119" font-family="Verdana" font-size="3.6" fill="rgb(0,0,255)" text-anchor="middle"  >150.0</text> </g>
  Visible = true
  X = 0
  Y = 0
FEATURE [Drawing::FeatureView] dim017
  Rotation = 0
  ViewResult = <g> <line x1="239.750000" y1="70.000000" x2="250.106182" y2="70.000000" style="stroke:rgb(0,0,255);stroke-width:0.20" />\n<line x1="230.750000" y1="74.500000" x2="250.106182" y2="74.500000" style="stroke:rgb(0,0,255);stroke-width:0.20" />\n<line x1="249.106182" y1="70.000000" x2="249.106182" y2="74.500000" style="stroke:rgb(0,0,255);stroke-width:0.20" />\n<polygon points="249.106182,70.000000 249.856182,67.000000 249.106182,67.000000 248.356182,67.000000" style="fill:rgb(0,0,255);stroke:rgb(0,0,255);stroke-width:0" />\n<polygon points="249.106182,74.500000 248.356182,77.500000 249.106182,77.500000 249.856182,77.500000" style="fill:rgb(0,0,255);stroke:rgb(0,0,255);stroke-width:0" />\n<text x="249.945741" y="62.635568" font-family="Verdana" font-size="3.6" fill="rgb(0,0,255)" text-anchor="middle" transform="rotate(-90.000000 249.945741,62.635568)" >10.0</text> </g> 
  Visible = true
  X = 0
  Y = 0
FEATURE [Drawing::FeatureView] dim026
  Rotation = 0
  ViewResult = <g> <line x1="240.000000" y1="115.920000" x2="240.000000" y2="127.155052" style="stroke:rgb(0,0,255);stroke-width:0.20" />\n<line x1="228.750000" y1="112.770000" x2="228.750000" y2="127.155052" style="stroke:rgb(0,0,255);stroke-width:0.20" />\n<line x1="240.000000" y1="126.155052" x2="228.750000" y2="126.155052" style="stroke:rgb(0,0,255);stroke-width:0.20" />\n<polygon points="240.000000,126.155052 237.000000,125.405052 237.000000,126.155052 237.000000,126.905052" style="fill:rgb(0,0,255);stroke:rgb(0,0,255);stroke-width:0" />\n<polygon points="228.750000,126.155052 231.750000,126.905052 231.750000,126.155052 231.750000,125.405052" style="fill:rgb(0,0,255);stroke:rgb(0,0,255);stroke-width:0" />\n<text x="234.375000" y="125.155052" font-family="Verdana" font-size="3.6" fill="rgb(0,0,255)" text-anchor="middle"  >25.0</text> </g> 
  Visible = true
  X = 0
  Y = 0
FEATURE [Drawing::FeatureView] dim007
  Rotation = 0
  ViewResult = <g> <line x1="38.750000" y1="41.250000" x2="30.978591" y2="41.250000" style="stroke:rgb(0,0,255);stroke-width:0.20" />\n<line x1="38.750000" y1="158.750000" x2="30.978591" y2="158.750000" style="stroke:rgb(0,0,255);stroke-width:0.20" />\n<line x1="31.978591" y1="41.250000" x2="31.978591" y2="158.750000" style="stroke:rgb(0,0,255);stroke-width:0.20" />\n<polygon points="31.978591,41.250000 31.228591,44.250000 31.978591,44.250000 32.728591,44.250000" style="fill:rgb(0,0,255);stroke:rgb(0,0,255);stroke-width:0" />\n<polygon points="31.978591,158.750000 32.728591,155.750000 31.978591,155.750000 31.228591,155.750000" style="fill:rgb(0,0,255);stroke:rgb(0,0,255);stroke-width:0" />\n<text x="30.978591" y="100.000000" font-family="Verdana" font-size="3.6" fill="rgb(0,0,255)" text-anchor="middle" transform="rotate(-90.000000 30.978591,100.000000)" >470.0</text> </g> 
  Visible = true
  X = 0
  Y = 0
FEATURE [Drawing::FeatureView] dim035
  Rotation = 0
  ViewResult = <g> <line x1="43.000000" y1="120.000000" x2="43.000000" y2="144.781492" style="stroke:rgb(0,0,255);stroke-width:0.20" />\n<line x1="81.000000" y1="105.880037" x2="81.000000" y2="144.781492" style="stroke:rgb(0,0,255);stroke-width:0.20" />\n<line x1="43.000000" y1="143.781492" x2="81.000000" y2="143.781492" style="stroke:rgb(0,0,255);stroke-width:0.20" />\n<polygon points="43.000000,143.781492 46.000000,144.531492 46.000000,143.781492 46.000000,143.031492" style="fill:rgb(0,0,255);stroke:rgb(0,0,255);stroke-width:0" />\n<polygon points="81.000000,143.781492 78.000000,143.031492 78.000000,143.781492 78.000000,144.531492" style="fill:rgb(0,0,255);stroke:rgb(0,0,255);stroke-width:0" />\n<text x="62.000000" y="142.781492" font-family="Verdana" font-size="3.6" fill="rgb(0,0,255)" text-anchor="middle"  >95.0</text> </g> 
  Visible = true
  X = 0
  Y = 0
FEATURE [Drawing::FeatureView] dimText001
  Rotation = 0
  ViewResult = <g> <text x="156.204277" y="83.183483" font-family="inherit" font-size="5" fill="rgb(0,0,0)" text-anchor="inherit"  >NOTES(UNLESS OTHERWISE SPECIFIED):</text> </g>
  Visible = true
  X = 0
  Y = 0
FEATURE [Drawing::FeatureView] dim039
  Rotation = 0
  ViewResult = <g> \n  <line x1="111.000000" y1="83.880000" x2="111.000000" y2="73.917634" style="stroke:rgb(0,0,255);stroke-width:0.20" />\n<line x1="147.000000" y1="83.880000" x2="147.000000" y2="73.917634" style="stroke:rgb(0,0,255);stroke-width:0.20" />\n<line x1="111.000000" y1="74.917634" x2="147.000000" y2="74.917634" style="stroke:rgb(0,0,255);stroke-width:0.20" /> \n  <polygon points="147.000000,74.917634 144.000000,74.167634 144.000000,74.917634 144.000000,75.667634" style="fill:rgb(0,0,255);stroke:rgb(0,0,255);stroke-width:0" /><polygon points="111.000000,74.917634 114.000000,75.667634 114.000000,74.917634 114.000000,74.167634" style="fill:rgb(0,0,255);stroke:rgb(0,0,255);stroke-width:0" /> \n  <text x="129.000000" y="73.917634" font-family="Verdana" font-size="3.6" fill="rgb(0,0,255)" text-anchor="middle"  >90.0</text> </g>
  Visible = true
  X = 0
  Y = 0
FEATURE [Drawing::FeatureView] dim019
  Rotation = 0
  ViewResult = <g> <line x1="239.750000" y1="70.000000" x2="262.119617" y2="70.000000" style="stroke:rgb(0,0,255);stroke-width:0.20" />\n<line x1="199.362712" y1="109.195000" x2="262.119617" y2="109.195000" style="stroke:rgb(0,0,255);stroke-width:0.20" />\n<line x1="261.119617" y1="70.000000" x2="261.119617" y2="109.195000" style="stroke:rgb(0,0,255);stroke-width:0.20" />\n<polygon points="261.119617,70.000000 260.369617,73.000000 261.119617,73.000000 261.869617,73.000000" style="fill:rgb(0,0,255);stroke:rgb(0,0,255);stroke-width:0" />\n<polygon points="261.119617,109.195000 261.869617,106.195000 261.119617,106.195000 260.369617,106.195000" style="fill:rgb(0,0,255);stroke:rgb(0,0,255);stroke-width:0" />\n<text x="260.119617" y="89.597500" font-family="Verdana" font-size="3.6" fill="rgb(0,0,255)" text-anchor="middle" transform="rotate(-90.000000 260.119617,89.597500)" >87.1</text> </g> 
  Visible = true
  X = 0
  Y = 0
FEATURE [Drawing::FeatureView] dim049
  Rotation = 0
  ViewResult = <g> \n  <line x1="231.000000" y1="115.300000" x2="231.000000" y2="135.405299" style="stroke:rgb(0,0,255);stroke-width:0.20" />\n<line x1="202.400000" y1="115.300000" x2="202.400000" y2="135.405299" style="stroke:rgb(0,0,255);stroke-width:0.20" />\n<line x1="231.000000" y1="134.405299" x2="202.400000" y2="134.405299" style="stroke:rgb(0,0,255);stroke-width:0.20" /> \n  <polygon points="202.400000,134.405299 205.400000,135.155299 205.400000,134.405299 205.400000,133.655299" style="fill:rgb(0,0,255);stroke:rgb(0,0,255);stroke-width:0" /><polygon points="231.000000,134.405299 228.000000,133.655299 228.000000,134.405299 228.000000,135.155299" style="fill:rgb(0,0,255);stroke:rgb(0,0,255);stroke-width:0" /> \n  <text x="216.700000" y="133.405299" font-family="Verdana" font-size="3.6" fill="rgb(0,0,255)" text-anchor="middle" transform="rotate(0.000000 216.700000,133.405299)" >71.5</text> </g>
  Visible = true
  X = 0
  Y = 0
FEATURE [Drawing::FeatureView] dim055
  Rotation = 0
  ViewResult = <g> <line x1="184.000000" y1="82.960000" x2="184.000000" y2="73.808675" style="stroke:rgb(0,0,255);stroke-width:0.20" />\n<line x1="178.400000" y1="82.960000" x2="178.400000" y2="73.808675" style="stroke:rgb(0,0,255);stroke-width:0.20" />\n<line x1="184.000000" y1="74.808675" x2="178.400000" y2="74.808675" style="stroke:rgb(0,0,255);stroke-width:0.20" />\n<polygon points="184.000000,74.808675 187.000000,75.558675 187.000000,74.808675 187.000000,74.058675" style="fill:rgb(0,0,255);stroke:rgb(0,0,255);stroke-width:0" />\n<polygon points="178.400000,74.808675 175.400000,74.058675 175.400000,74.808675 175.400000,75.558675" style="fill:rgb(0,0,255);stroke:rgb(0,0,255);stroke-width:0" />\n<text x="181.200000" y="73.808675" font-family="Verdana" font-size="3.6" fill="rgb(0,0,255)" text-anchor="middle"  >14.0</text> </g> 
  Visible = true
  X = 0
  Y = 0
FEATURE [Drawing::FeatureViewPart] Ortho027  label="Ortho_0_1"
  Direction = (1,0,0)
  HiddenWidth = 0.15
  LineWidth = 0.35
  Rotation = -90
  Scale = 0.3
  ShowHiddenLines = false
  ShowSmoothLines = false
  Tolerance = 0.05
  ViewResult = <blob: 18153 chars omitted>
  Visible = true
  X = 50
  Y = 175
FEATURE [Drawing::FeatureView] dim006
  Rotation = 0
  ViewResult = <g> <line x1="80.750000" y1="40.000000" x2="94.391042" y2="40.000000" style="stroke:rgb(0,0,255);stroke-width:0.20" />\n<line x1="81.500000" y1="43.000000" x2="94.391042" y2="43.000000" style="stroke:rgb(0,0,255);stroke-width:0.20" />\n<line x1="93.391042" y1="40.000000" x2="93.391042" y2="43.000000" style="stroke:rgb(0,0,255);stroke-width:0.20" />\n<polygon points="93.391042,40.000000 94.141042,37.000000 93.391042,37.000000 92.641042,37.000000" style="fill:rgb(0,0,255);stroke:rgb(0,0,255);stroke-width:0" />\n<polygon points="93.391042,43.000000 92.641042,46.000000 93.391042,46.000000 94.141042,46.000000" style="fill:rgb(0,0,255);stroke:rgb(0,0,255);stroke-width:0" />\n<text x="94.038739" y="30.623566" font-family="Verdana" font-size="3.6" fill="rgb(0,0,255)" text-anchor="middle" transform="rotate(-90.000000 94.038739,30.623566)" >12.0</text> </g> 
  Visible = true
  X = 0
  Y = 0
FEATURE [Drawing::FeatureView] dim020
  Rotation = 0
  ViewResult = <g> <line x1="239.750000" y1="70.000000" x2="267.573993" y2="70.000000" style="stroke:rgb(0,0,255);stroke-width:0.20" />\n<line x1="230.750000" y1="110.770000" x2="267.573993" y2="110.770000" style="stroke:rgb(0,0,255);stroke-width:0.20" />\n<line x1="266.573993" y1="70.000000" x2="266.573993" y2="110.770000" style="stroke:rgb(0,0,255);stroke-width:0.20" />\n<polygon points="266.573993,70.000000 265.823993,73.000000 266.573993,73.000000 267.323993,73.000000" style="fill:rgb(0,0,255);stroke:rgb(0,0,255);stroke-width:0" />\n<polygon points="266.573993,110.770000 267.323993,107.770000 266.573993,107.770000 265.823993,107.770000" style="fill:rgb(0,0,255);stroke:rgb(0,0,255);stroke-width:0" />\n<text x="265.573993" y="90.385000" font-family="Verdana" font-size="3.6" fill="rgb(0,0,255)" text-anchor="middle" transform="rotate(-90.000000 265.573993,90.385000)" >90.6</text> </g> 
  Visible = true
  X = 0
  Y = 0
FEATURE [Drawing::FeatureView] dim018
  Rotation = 0
  ViewResult = <g> <line x1="239.750000" y1="70.000000" x2="255.767686" y2="70.000000" style="stroke:rgb(0,0,255);stroke-width:0.20" />\n<line x1="192.275000" y1="86.425000" x2="255.767686" y2="86.425000" style="stroke:rgb(0,0,255);stroke-width:0.20" />\n<line x1="254.767686" y1="70.000000" x2="254.767686" y2="86.425000" style="stroke:rgb(0,0,255);stroke-width:0.20" />\n<polygon points="254.767686,70.000000 254.017686,73.000000 254.767686,73.000000 255.517686,73.000000" style="fill:rgb(0,0,255);stroke:rgb(0,0,255);stroke-width:0" />\n<polygon points="254.767686,86.425000 255.517686,83.425000 254.767686,83.425000 254.017686,83.425000" style="fill:rgb(0,0,255);stroke:rgb(0,0,255);stroke-width:0" />\n<text x="255.982617" y="63.566153" font-family="Verdana" font-size="3.6" fill="rgb(0,0,255)" text-anchor="middle" transform="rotate(-90.000000 255.982617,63.566153)" >35.0</text> </g> 
  Visible = true
  X = 0
  Y = 0
FEATURE [Drawing::FeatureView] dim043
  Rotation = 0
  ViewResult = <g> <line x1="235.000000" y1="120.000000" x2="235.000000" y2="130.496551" style="stroke:rgb(0,0,255);stroke-width:0.20" />\n<line x1="231.000000" y1="115.300037" x2="231.000000" y2="130.496551" style="stroke:rgb(0,0,255);stroke-width:0.20" />\n<line x1="235.000000" y1="129.496551" x2="231.000000" y2="129.496551" style="stroke:rgb(0,0,255);stroke-width:0.20" />\n<polygon points="235.000000,129.496551 238.000000,130.246551 238.000000,129.496551 238.000000,128.746551" style="fill:rgb(0,0,255);stroke:rgb(0,0,255);stroke-width:0" />\n<polygon points="231.000000,129.496551 228.000000,128.746551 228.000000,129.496551 228.000000,130.246551" style="fill:rgb(0,0,255);stroke:rgb(0,0,255);stroke-width:0" />\n<text x="243.150189" y="130.104144" font-family="Verdana" font-size="3.6" fill="rgb(0,0,255)" text-anchor="middle"  >10.0</text> </g> 
  Visible = true
  X = 0
  Y = 0
FEATURE [Drawing::FeatureView] dim057
  Rotation = 0
  ViewResult = <g>  <circle cx ="175.000000" cy ="108.000000" r="0.500000" stroke="none" fill="rgb(0,0,255)" /> \n<line x1="183.179313" y1="124.994788" x2="172.334659" y2="102.462016" style="stroke:rgb(0,0,255);stroke-width:0.20" />\n<polygon points="177.665341,113.537984 177.040132,110.509517 176.364329,110.834770 175.688525,111.160024" style="fill:rgb(0,0,255);stroke:rgb(0,0,255);stroke-width:0" />\n<polygon points="172.334659,102.462016 172.959868,105.490483 173.635671,105.165230 174.311475,104.839976" style="fill:rgb(0,0,255);stroke:rgb(0,0,255);stroke-width:0" />\n<line x1="183.179313" y1="124.994788" x2="199.803463" y2="124.994788" style="stroke:rgb(0,0,255);stroke-width:0.20" />\n<text x="191.491388" y="123.994788" font-family="Verdana" font-size="3.6" fill="rgb(0,0,255)" text-anchor="middle"  >Ø30.7</text> </g>
  Visible = true
  X = 0
  Y = 0
FEATURE [Drawing::FeatureView] centerLines007
  Rotation = 0
  ViewResult = <g transform="scale(0.400000,0.400000)" stroke="rgb(0,0,255)"  stroke-width="0.750000" > <path d="M 506.000000,213.950000 L 506.000000,215.347047 "/>\n<path d="M 506.000000,213.950000 L 511.000000,213.950000 M 516.000000,213.950000 L 531.000000,213.950000 M 536.000000,213.950000 L 541.000000,213.950000 M 546.000000,213.950000 L 561.000000,213.950000 M 566.000000,213.950000 L 571.000000,213.950000 M 576.000000,213.950000 L 577.440281,213.950000 "/>\n<path d="M 506.000000,213.950000 L 506.000000,218.950000 M 506.000000,223.950000 L 506.000000,238.950000 M 506.000000,243.950000 L 506.000000,248.950000 M 506.000000,253.950000 L 506.000000,268.950000 M 506.000000,273.950000 L 506.000000,278.950000 M 506.000000,283.950000 L 506.000000,285.439230 "/>\n<path d="M 506.000000,213.950000 L 505.856775,213.950000 "/> </g> 
  Visible = true
  X = 0
  Y = 0
FEATURE [Drawing::FeatureView] dim059
  Rotation = 0
  ViewResult = <g>  <circle cx ="219.401320" cy ="88.085400" r="0.500000" stroke="none" fill="rgb(0,0,255)" /> \n<line x1="227.277631" y1="50.009033" x2="219.198753" y2="89.064668" style="stroke:rgb(0,0,255);stroke-width:0.20" />\n<polygon points="219.603887,87.106132 220.946040,84.320252 220.211589,84.168327 219.477137,84.016401" style="fill:rgb(0,0,255);stroke:rgb(0,0,255);stroke-width:0" />\n<polygon points="219.198753,89.064668 217.856600,91.850548 218.591051,92.002473 219.325503,92.154399" style="fill:rgb(0,0,255);stroke:rgb(0,0,255);stroke-width:0" />\n<line x1="227.277631" y1="50.009033" x2="265.256658" y2="50.009033" style="stroke:rgb(0,0,255);stroke-width:0.20" />\n<text x="234.871010" y="43.134964" font-family="Verdana" font-size="3.6" fill="rgb(0,0,255)" text-anchor="middle"  >Ø5.0 THRU</text> </g>
  Visible = true
  X = 0
  Y = 0
FEATURE [Drawing::FeatureView] dimText021
  Rotation = 0
  ViewResult = <g> <text x="226.740859" y="48.103389" font-family="inherit" font-size="3.6" fill="rgb(0,0,255)" text-anchor="inherit"  >SEE 3D BODY FOR DETAIL</text> </g>
  Visible = true
  X = 0
  Y = 0
FEATURE [Drawing::FeatureView] dimText022
  Rotation = 0
  ViewResult = <g> <text x="79.660416" y="18.801837" font-family="inherit" font-size="3.6" fill="rgb(0,0,255)" text-anchor="inherit"  >INSTALL FROM OTHER SIDE</text> </g>
  Visible = true
  X = 0
  Y = 0
FEATURE [Drawing::FeatureView] dimText024
  Rotation = 0
  ViewResult = <g> <text x="169.366575" y="150.468529" font-family="inherit" font-size="3.6" fill="rgb(0,0,255)" text-anchor="inherit"  >INSTALL STUD TOWARD OTHER SIDE</text> </g>
  Visible = true
  X = 0
  Y = 0
FEATURE [Drawing::FeatureView] dim051
  Rotation = 0
  ViewResult = <g>  <circle cx ="147.000000" cy ="113.880000" r="0.500000" stroke="none" fill="rgb(0,0,255)" /> \n<line x1="160.970215" y1="169.900904" x2="146.758035" y2="112.909715" style="stroke:rgb(0,0,255);stroke-width:0.20" />\n<polygon points="147.241965,114.850285 147.240146,117.942614 147.967859,117.761140 148.695573,117.579666" style="fill:rgb(0,0,255);stroke:rgb(0,0,255);stroke-width:0" />\n<polygon points="146.758035,112.909715 146.759854,109.817386 146.032141,109.998860 145.304427,110.180334" style="fill:rgb(0,0,255);stroke:rgb(0,0,255);stroke-width:0" />\n<line x1="160.970215" y1="169.900904" x2="225.554341" y2="169.900904" style="stroke:rgb(0,0,255);stroke-width:0.20" />\n<text x="195.168218" y="162.277145" font-family="Verdana" font-size="3.6" fill="rgb(0,0,255)" text-anchor="middle"  >6 X SOS-35M3-12 BLIND STANDOFFS</text> </g>
  Visible = true
  X = 0
  Y = 0
FEATURE [Drawing::FeatureView] dim053
  Rotation = 0
  ViewResult = <g>  <circle cx ="155.000000" cy ="108.000000" r="0.500000" stroke="none" fill="rgb(0,0,255)" /> \n<line x1="167.362237" y1="152.759202" x2="154.840264" y2="107.421654" style="stroke:rgb(0,0,255);stroke-width:0.20" />\n<polygon points="155.159736,108.578346 155.235483,111.669748 155.958416,111.470078 156.681349,111.270408" style="fill:rgb(0,0,255);stroke:rgb(0,0,255);stroke-width:0" />\n<polygon points="154.840264,107.421654 154.764517,104.330252 154.041584,104.529922 153.318651,104.729592" style="fill:rgb(0,0,255);stroke:rgb(0,0,255);stroke-width:0" />\n<line x1="167.362237" y1="152.759202" x2="234.507565" y2="152.759202" style="stroke:rgb(0,0,255);stroke-width:0.20" />\n<text x="203.726658" y="146.030352" font-family="Verdana" font-size="3.6" fill="rgb(0,0,255)" text-anchor="middle"  >Ø3 FOR FHA-M3-10 FLUSH HEAD STUD</text> </g>
  Visible = true
  X = 0
  Y = 0
FEATURE [Drawing::FeatureView] dimText023
  Rotation = 0
  ViewResult = <g> <text x="109.594920" y="43.293704" font-family="inherit" font-size="3.6" fill="rgb(0,0,255)" text-anchor="inherit"  >Ø6.0, 90 DEG CHAMFER</text> </g>
  Visible = true
  X = 0
  Y = 0
FEATURE [Drawing::FeatureView] dim058
  Rotation = 0
  ViewResult = <g> \n  <line x1="169.284000" y1="114.538000" x2="169.284000" y2="128.304107" style="stroke:rgb(0,0,255);stroke-width:0.20" />\n<line x1="180.700000" y1="114.938000" x2="180.700000" y2="128.304107" style="stroke:rgb(0,0,255);stroke-width:0.20" />\n<line x1="169.284000" y1="127.304107" x2="180.700000" y2="127.304107" style="stroke:rgb(0,0,255);stroke-width:0.20" /> \n  <polygon points="180.700000,127.304107 177.700000,126.554107 177.700000,127.304107 177.700000,128.054107" style="fill:rgb(0,0,255);stroke:rgb(0,0,255);stroke-width:0" /><polygon points="169.284000,127.304107 172.284000,128.054107 172.284000,127.304107 172.284000,126.554107" style="fill:rgb(0,0,255);stroke:rgb(0,0,255);stroke-width:0" /> \n  <text x="174.992000" y="126.304107" font-family="Verdana" font-size="3.6" fill="rgb(0,0,255)" text-anchor="middle" transform="rotate(0.000000 174.992000,126.304107)" >28.54</text> </g>
  Visible = true
  X = 0
  Y = 0
FEATURE [Drawing::FeatureView] dim060
  Rotation = 0
  ViewResult = <g> <line x1="167.283812" y1="113.700000" x2="165.508058" y2="113.700000" style="stroke:rgb(0,0,255);stroke-width:0.20" />\n<line x1="166.508058" y1="120.000000" x2="166.508058" y2="113.700000" style="stroke:rgb(0,0,255);stroke-width:0.20" />\n<polygon points="166.508058,120.000000 165.758058,123.000000 166.508058,123.000000 167.258058,123.000000" style="fill:rgb(0,0,255);stroke:rgb(0,0,255);stroke-width:0" />\n<polygon points="166.508058,113.700000 167.258058,110.700000 166.508058,110.700000 165.758058,110.700000" style="fill:rgb(0,0,255);stroke:rgb(0,0,255);stroke-width:0" />\n<text x="167.773842" y="130.375695" font-family="Verdana" font-size="3.6" fill="rgb(0,0,255)" text-anchor="middle" transform="rotate(-90.000000 167.773842,130.375695)" >15.75</text> </g> 
  Visible = true
  X = 0
  Y = 0
FEATURE [Drawing::FeatureView] dim061
  Rotation = 0
  ViewResult = <g> <line x1="153.599812" y1="108.000000" x2="152.274868" y2="108.000000" style="stroke:rgb(0,0,255);stroke-width:0.20" />\n<line x1="153.274868" y1="120.000000" x2="153.274868" y2="108.000000" style="stroke:rgb(0,0,255);stroke-width:0.20" />\n<polygon points="153.274868,120.000000 154.024868,117.000000 153.274868,117.000000 152.524868,117.000000" style="fill:rgb(0,0,255);stroke:rgb(0,0,255);stroke-width:0" />\n<polygon points="153.274868,108.000000 152.524868,111.000000 153.274868,111.000000 154.024868,111.000000" style="fill:rgb(0,0,255);stroke:rgb(0,0,255);stroke-width:0" />\n<text x="153.812010" y="124.899978" font-family="Verdana" font-size="3.6" fill="rgb(0,0,255)" text-anchor="middle" transform="rotate(-90.000000 153.812010,124.899978)" >30.0</text> </g> 
  Visible = true
  X = 0
  Y = 0
FEATURE [Drawing::FeatureView] dim062
  Rotation = 0
  ViewResult = <g> <line x1="235.000000" y1="120.000000" x2="235.000000" y2="139.642934" style="stroke:rgb(0,0,255);stroke-width:0.20" />\n<line x1="155.000000" y1="109.400037" x2="155.000000" y2="139.642934" style="stroke:rgb(0,0,255);stroke-width:0.20" />\n<line x1="235.000000" y1="138.642934" x2="155.000000" y2="138.642934" style="stroke:rgb(0,0,255);stroke-width:0.20" />\n<polygon points="235.000000,138.642934 232.000000,137.892934 232.000000,138.642934 232.000000,139.392934" style="fill:rgb(0,0,255);stroke:rgb(0,0,255);stroke-width:0" />\n<polygon points="155.000000,138.642934 158.000000,139.392934 158.000000,138.642934 158.000000,137.892934" style="fill:rgb(0,0,255);stroke:rgb(0,0,255);stroke-width:0" />\n<text x="195.000000" y="137.642934" font-family="Verdana" font-size="3.6" fill="rgb(0,0,255)" text-anchor="middle"  >200.0</text> </g> 
  Visible = true
  X = 0
  Y = 0
FEATURE [Drawing::FeatureView] dim063
  Rotation = 0
  ViewResult = <g> \n  <line x1="183.462000" y1="113.700000" x2="243.704772" y2="113.700000" style="stroke:rgb(0,0,255);stroke-width:0.20" />\n<line x1="183.462000" y1="102.284000" x2="243.704772" y2="102.284000" style="stroke:rgb(0,0,255);stroke-width:0.20" />\n<line x1="242.704772" y1="113.700000" x2="242.704772" y2="102.284000" style="stroke:rgb(0,0,255);stroke-width:0.20" /> \n  <polygon points="242.704772,102.284000 241.954772,105.284000 242.704772,105.284000 243.454772,105.284000" style="fill:rgb(0,0,255);stroke:rgb(0,0,255);stroke-width:0" /><polygon points="242.704772,113.700000 243.454772,110.700000 242.704772,110.700000 241.954772,110.700000" style="fill:rgb(0,0,255);stroke:rgb(0,0,255);stroke-width:0" /> \n  <text x="241.704772" y="107.992000" font-family="Verdana" font-size="3.6" fill="rgb(0,0,255)" text-anchor="middle" transform="rotate(-90.000000 241.704772,107.992000)" >28.54</text> </g>
  Visible = true
  X = 0
  Y = 0
FEATURE [Drawing::FeatureView] dim064
  Rotation = 0
  ViewResult = <g> <line x1="235.800000" y1="79.760000" x2="242.832944" y2="79.760000" style="stroke:rgb(0,0,255);stroke-width:0.20" />\n<line x1="232.120190" y1="85.580000" x2="242.832944" y2="85.580000" style="stroke:rgb(0,0,255);stroke-width:0.20" />\n<line x1="241.832944" y1="79.760000" x2="241.832944" y2="85.580000" style="stroke:rgb(0,0,255);stroke-width:0.20" />\n<polygon points="241.832944,79.760000 242.582944,76.760000 241.832944,76.760000 241.082944,76.760000" style="fill:rgb(0,0,255);stroke:rgb(0,0,255);stroke-width:0" />\n<polygon points="241.832944,85.580000 241.082944,88.580000 241.832944,88.580000 242.582944,88.580000" style="fill:rgb(0,0,255);stroke:rgb(0,0,255);stroke-width:0" />\n<text x="242.692137" y="70.259497" font-family="Verdana" font-size="3.6" fill="rgb(0,0,255)" text-anchor="middle" transform="rotate(-90.000000 242.692137,70.259497)" >14.6</text> </g> 
  Visible = true
  X = 0
  Y = 0
FEATURE [Drawing::FeatureView] dim065
  Rotation = 0
  ViewResult = <g> <line x1="176.400000" y1="84.960000" x2="156.025578" y2="84.960000" style="stroke:rgb(0,0,255);stroke-width:0.20" />\n<line x1="157.025578" y1="79.760000" x2="157.025578" y2="84.960000" style="stroke:rgb(0,0,255);stroke-width:0.20" />\n<polygon points="157.025578,79.760000 157.775578,76.760000 157.025578,76.760000 156.275578,76.760000" style="fill:rgb(0,0,255);stroke:rgb(0,0,255);stroke-width:0" />\n<polygon points="157.025578,84.960000 156.275578,87.960000 157.025578,87.960000 157.775578,87.960000" style="fill:rgb(0,0,255);stroke:rgb(0,0,255);stroke-width:0" />\n<text x="158.727055" y="69.677997" font-family="Verdana" font-size="3.6" fill="rgb(0,0,255)" text-anchor="middle" transform="rotate(-90.000000 158.727055,69.677997)" >13.0</text> </g> 
  Visible = true
  X = 0
  Y = 0
FEATURE [Drawing::FeatureView] dim066
  Rotation = 0
  ViewResult = <g> <line x1="186.000000" y1="84.960000" x2="248.564397" y2="84.960000" style="stroke:rgb(0,0,255);stroke-width:0.20" />\n<line x1="186.000000" y1="90.160000" x2="248.564397" y2="90.160000" style="stroke:rgb(0,0,255);stroke-width:0.20" />\n<line x1="247.564397" y1="84.960000" x2="247.564397" y2="90.160000" style="stroke:rgb(0,0,255);stroke-width:0.20" />\n<polygon points="247.564397,84.960000 248.314397,81.960000 247.564397,81.960000 246.814397,81.960000" style="fill:rgb(0,0,255);stroke:rgb(0,0,255);stroke-width:0" />\n<polygon points="247.564397,90.160000 246.814397,93.160000 247.564397,93.160000 248.314397,93.160000" style="fill:rgb(0,0,255);stroke:rgb(0,0,255);stroke-width:0" />\n<text x="248.382167" y="77.928668" font-family="Verdana" font-size="3.6" fill="rgb(0,0,255)" text-anchor="middle" transform="rotate(-90.000000 248.382167,77.928668)" >13.0</text> </g> 
  Visible = true
  X = 0
  Y = 0
FEATURE [Drawing::FeatureView] dim067
  Rotation = 0
  ViewResult = <g> \n  <line x1="233.880000" y1="114.180000" x2="256.831553" y2="114.180000" style="stroke:rgb(0,0,255);stroke-width:0.20" />\n<line x1="233.880000" y1="85.580000" x2="256.831553" y2="85.580000" style="stroke:rgb(0,0,255);stroke-width:0.20" />\n<line x1="255.831553" y1="114.180000" x2="255.831553" y2="85.580000" style="stroke:rgb(0,0,255);stroke-width:0.20" /> \n  <polygon points="255.831553,85.580000 255.081553,88.580000 255.831553,88.580000 256.581553,88.580000" style="fill:rgb(0,0,255);stroke:rgb(0,0,255);stroke-width:0" /><polygon points="255.831553,114.180000 256.581553,111.180000 255.831553,111.180000 255.081553,111.180000" style="fill:rgb(0,0,255);stroke:rgb(0,0,255);stroke-width:0" /> \n  <text x="254.831553" y="99.880000" font-family="Verdana" font-size="3.6" fill="rgb(0,0,255)" text-anchor="middle" transform="rotate(-90.000000 254.831553,99.880000)" >71.5</text> </g>
  Visible = true
  X = 0
  Y = 0
FEATURE [Drawing::FeatureView] centerLines011
  Rotation = 0
  ViewResult = <g transform="scale(0.300000,0.300000)" stroke="rgb(0,0,255)"  stroke-width="1.000000" > <path d="M 194.556667,419.333333 L 201.223333,419.333333 M 207.890000,419.333333 L 227.890000,419.333333 M 234.556667,419.333333 L 241.223333,419.333333 M 247.890000,419.333333 L 267.890000,419.333333 M 274.556667,419.333333 L 281.223333,419.333333 M 287.890000,419.333333 L 307.890000,419.333333 M 314.556667,419.333333 L 321.223333,419.333333 M 327.890000,419.333333 L 347.890000,419.333333 M 354.556667,419.333333 L 361.223333,419.333333 M 367.890000,419.333333 L 387.890000,419.333333 M 394.556667,419.333333 L 401.223333,419.333333 M 407.890000,419.333333 L 427.890000,419.333333 M 434.556667,419.333333 L 441.223333,419.333333 M 447.890000,419.333333 L 467.890000,419.333333 M 474.556667,419.333333 L 481.223333,419.333333 M 487.890000,419.333333 L 507.890000,419.333333 M 514.556667,419.333333 L 521.223333,419.333333 M 527.890000,419.333333 L 547.890000,419.333333 M 554.556667,419.333333 L 561.223333,419.333333 M 567.890000,419.333333 L 587.890000,419.333333 M 594.556667,419.333333 L 601.223333,419.333333 M 607.890000,419.333333 L 617.916518,419.333333 "/>\n<path d="M 194.556667,419.333333 L 197.085049,419.333333 "/> </g> 
  Visible = true
  X = 0
  Y = 0
FEATURE [Drawing::FeatureView] dim068
  Rotation = 0
  ViewResult = <g> <line x1="55.500000" y1="124.000000" x2="17.966766" y2="124.000000" style="stroke:rgb(0,0,255);stroke-width:0.20" />\n<line x1="50.432984" y1="166.000000" x2="17.966766" y2="166.000000" style="stroke:rgb(0,0,255);stroke-width:0.20" />\n<line x1="18.966766" y1="124.000000" x2="18.966766" y2="166.000000" style="stroke:rgb(0,0,255);stroke-width:0.20" />\n<polygon points="18.966766,124.000000 18.216766,127.000000 18.966766,127.000000 19.716766,127.000000" style="fill:rgb(0,0,255);stroke:rgb(0,0,255);stroke-width:0" />\n<polygon points="18.966766,166.000000 19.716766,163.000000 18.966766,163.000000 18.216766,163.000000" style="fill:rgb(0,0,255);stroke:rgb(0,0,255);stroke-width:0" />\n<text x="17.966766" y="145.000000" font-family="Verdana" font-size="3.6" fill="rgb(0,0,255)" text-anchor="middle" transform="rotate(-90.000000 17.966766,145.000000)" >2X 140 ±0.5</text> </g> 
  Visible = true
  X = 0
  Y = 0
FEATURE [Drawing::FeatureView] dim069
  Rotation = 0
  ViewResult = <g> <line x1="55.500000" y1="124.000000" x2="26.837610" y2="124.000000" style="stroke:rgb(0,0,255);stroke-width:0.20" />\n<line x1="50.432984" y1="149.500000" x2="26.837610" y2="149.500000" style="stroke:rgb(0,0,255);stroke-width:0.20" />\n<line x1="27.837610" y1="124.000000" x2="27.837610" y2="149.500000" style="stroke:rgb(0,0,255);stroke-width:0.20" />\n<polygon points="27.837610,124.000000 27.087610,127.000000 27.837610,127.000000 28.587610,127.000000" style="fill:rgb(0,0,255);stroke:rgb(0,0,255);stroke-width:0" />\n<polygon points="27.837610,149.500000 28.587610,146.500000 27.837610,146.500000 27.087610,146.500000" style="fill:rgb(0,0,255);stroke:rgb(0,0,255);stroke-width:0" />\n<text x="26.837610" y="136.750000" font-family="Verdana" font-size="3.6" fill="rgb(0,0,255)" text-anchor="middle" transform="rotate(-90.000000 26.837610,136.750000)" >2X 85 ±0.5</text> </g> 
  Visible = true
  X = 0
  Y = 0
FEATURE [Drawing::FeatureView] dim070
  Rotation = 0
  ViewResult = <g> <line x1="55.500000" y1="124.000000" x2="34.417804" y2="124.000000" style="stroke:rgb(0,0,255);stroke-width:0.20" />\n<line x1="50.432984" y1="133.000000" x2="34.417804" y2="133.000000" style="stroke:rgb(0,0,255);stroke-width:0.20" />\n<line x1="35.417804" y1="124.000000" x2="35.417804" y2="133.000000" style="stroke:rgb(0,0,255);stroke-width:0.20" />\n<polygon points="35.417804,124.000000 34.667804,127.000000 35.417804,127.000000 36.167804,127.000000" style="fill:rgb(0,0,255);stroke:rgb(0,0,255);stroke-width:0" />\n<polygon points="35.417804,133.000000 36.167804,130.000000 35.417804,130.000000 34.667804,130.000000" style="fill:rgb(0,0,255);stroke:rgb(0,0,255);stroke-width:0" />\n<text x="35.560743" y="112.477312" font-family="Verdana" font-size="3.6" fill="rgb(0,0,255)" text-anchor="middle" transform="rotate(-90.000000 35.560743,112.477312)" >2X 30 ±0.5</text> </g> 
  Visible = true
  X = 0
  Y = 0
FEATURE [Drawing::FeatureView] dim071
  Rotation = 0
  ViewResult = <g> <line x1="55.500000" y1="124.000000" x2="42.912849" y2="124.000000" style="stroke:rgb(0,0,255);stroke-width:0.20" />\n<line x1="57.632984" y1="125.800000" x2="42.912849" y2="125.800000" style="stroke:rgb(0,0,255);stroke-width:0.20" />\n<line x1="43.912849" y1="124.000000" x2="43.912849" y2="125.800000" style="stroke:rgb(0,0,255);stroke-width:0.20" />\n<polygon points="43.912849,124.000000 44.662849,121.000000 43.912849,121.000000 43.162849,121.000000" style="fill:rgb(0,0,255);stroke:rgb(0,0,255);stroke-width:0" />\n<polygon points="43.912849,125.800000 43.162849,128.800000 43.912849,128.800000 44.662849,128.800000" style="fill:rgb(0,0,255);stroke:rgb(0,0,255);stroke-width:0" />\n<text x="45.087962" y="115.102603" font-family="Verdana" font-size="3.6" fill="rgb(0,0,255)" text-anchor="middle" transform="rotate(-90.000000 45.087962,115.102603)" >4X 6.0</text> </g> 
  Visible = true
  X = 0
  Y = 0
FEATURE [Drawing::FeatureView] centerLines012
  Rotation = 0
  ViewResult = <g transform="scale(0.300000,0.300000)" stroke="rgb(0,0,255)"  stroke-width="1.000000" > <path d="M 172.666667,441.223333 L 172.666667,447.890000 M 172.666667,454.556667 L 172.666667,474.556667 M 172.666667,481.223333 L 172.666667,487.890000 M 172.666667,494.556667 L 172.666667,514.556667 M 172.666667,521.223333 L 172.666667,527.890000 M 172.666667,534.556667 L 172.666667,553.170379 "/>\n<path d="M 172.666667,441.223333 L 172.666667,447.890000 M 172.666667,454.556667 L 172.666667,474.556667 M 172.666667,481.223333 L 172.666667,487.890000 M 172.666667,494.556667 L 172.666667,514.556667 M 172.666667,521.223333 L 172.666667,527.890000 M 172.666667,534.556667 L 172.666667,553.170379 "/> </g> 
  Visible = true
  X = 0
  Y = 0
FEATURE [Drawing::FeatureView] centerLines013
  Rotation = 0
  ViewResult = <blob: 2232 chars omitted>
  Visible = true
  X = 0
  Y = 0
FEATURE [Drawing::FeatureView] centerLines014
  Rotation = 0
  ViewResult = <g transform="scale(0.300000,0.300000)" stroke="rgb(0,0,255)"  stroke-width="1.000000" > <path d="M 640.666667,553.333333 L 640.666667,546.666667 M 640.666667,540.000000 L 640.666667,520.000000 M 640.666667,513.333333 L 640.666667,506.666667 M 640.666667,500.000000 L 640.666667,480.000000 M 640.666667,473.333333 L 640.666667,466.666667 M 640.666667,460.000000 L 640.666667,442.103636 "/>\n<path d="M 640.666667,553.333333 L 640.666667,546.666667 M 640.666667,540.000000 L 640.666667,520.000000 M 640.666667,513.333333 L 640.666667,506.666667 M 640.666667,500.000000 L 640.666667,480.000000 M 640.666667,473.333333 L 640.666667,466.666667 M 640.666667,460.000000 L 640.666667,442.103636 "/> </g> 
  Visible = true
  X = 0
  Y = 0
FEATURE [Drawing::FeatureView] centerLines015
  Rotation = 0
  ViewResult = <g transform="scale(0.300000,0.300000)" stroke="rgb(0,0,255)"  stroke-width="1.000000" > <path d="M 640.666667,441.223333 L 640.666667,443.484490 "/>\n<path d="M 640.666667,441.223333 L 640.666667,443.484490 "/> </g> 
  Visible = true
  X = 0
  Y = 0
FEATURE [Drawing::FeatureView] dim076
  Rotation = 0
  ViewResult = <g> <line x1="50.000000" y1="126.500000" x2="50.000000" y2="119.134356" style="stroke:rgb(0,0,255);stroke-width:0.20" />\n<line x1="59.000000" y1="124.432958" x2="59.000000" y2="119.134356" style="stroke:rgb(0,0,255);stroke-width:0.20" />\n<line x1="50.000000" y1="120.134356" x2="59.000000" y2="120.134356" style="stroke:rgb(0,0,255);stroke-width:0.20" />\n<polygon points="50.000000,120.134356 53.000000,120.884356 53.000000,120.134356 53.000000,119.384356" style="fill:rgb(0,0,255);stroke:rgb(0,0,255);stroke-width:0" />\n<polygon points="59.000000,120.134356 56.000000,119.384356 56.000000,120.134356 56.000000,120.884356" style="fill:rgb(0,0,255);stroke:rgb(0,0,255);stroke-width:0" />\n<text x="69.804421" y="121.696764" font-family="Verdana" font-size="3.6" fill="rgb(0,0,255)" text-anchor="middle"  >2X 30 ±0.5</text> </g> 
  Visible = true
  X = 0
  Y = 0
FEATURE [Drawing::FeatureView] dim072
  Rotation = 0
  ViewResult = <g> <line x1="50.000000" y1="126.500000" x2="50.000000" y2="116.165518" style="stroke:rgb(0,0,255);stroke-width:0.20" />\n<line x1="101.000000" y1="123.166958" x2="101.000000" y2="116.165518" style="stroke:rgb(0,0,255);stroke-width:0.20" />\n<line x1="50.000000" y1="117.165518" x2="101.000000" y2="117.165518" style="stroke:rgb(0,0,255);stroke-width:0.20" />\n<polygon points="50.000000,117.165518 53.000000,117.915518 53.000000,117.165518 53.000000,116.415518" style="fill:rgb(0,0,255);stroke:rgb(0,0,255);stroke-width:0" />\n<polygon points="101.000000,117.165518 98.000000,116.415518 98.000000,117.165518 98.000000,117.915518" style="fill:rgb(0,0,255);stroke:rgb(0,0,255);stroke-width:0" />\n<text x="75.500000" y="116.165518" font-family="Verdana" font-size="3.6" fill="rgb(0,0,255)" text-anchor="middle"  >2X 170 ±0.5</text> </g> 
  Visible = true
  X = 0
  Y = 0
FEATURE [Drawing::FeatureView] dim077
  Rotation = 0
  ViewResult = <g> <line x1="50.000000" y1="126.500000" x2="50.000000" y2="110.851428" style="stroke:rgb(0,0,255);stroke-width:0.20" />\n<line x1="143.000000" y1="124.432958" x2="143.000000" y2="110.851428" style="stroke:rgb(0,0,255);stroke-width:0.20" />\n<line x1="50.000000" y1="111.851428" x2="143.000000" y2="111.851428" style="stroke:rgb(0,0,255);stroke-width:0.20" />\n<polygon points="50.000000,111.851428 53.000000,112.601428 53.000000,111.851428 53.000000,111.101428" style="fill:rgb(0,0,255);stroke:rgb(0,0,255);stroke-width:0" />\n<polygon points="143.000000,111.851428 140.000000,111.101428 140.000000,111.851428 140.000000,112.601428" style="fill:rgb(0,0,255);stroke:rgb(0,0,255);stroke-width:0" />\n<text x="96.500000" y="110.851428" font-family="Verdana" font-size="3.6" fill="rgb(0,0,255)" text-anchor="middle"  >2X 310 ±0.5</text> </g> 
  Visible = true
  X = 0
  Y = 0
FEATURE [Drawing::FeatureView] dim078
  Rotation = 0
  ViewResult = <g> <line x1="50.000000" y1="126.500000" x2="50.000000" y2="105.405887" style="stroke:rgb(0,0,255);stroke-width:0.20" />\n<line x1="185.000000" y1="124.432958" x2="185.000000" y2="105.405887" style="stroke:rgb(0,0,255);stroke-width:0.20" />\n<line x1="50.000000" y1="106.405887" x2="185.000000" y2="106.405887" style="stroke:rgb(0,0,255);stroke-width:0.20" />\n<polygon points="50.000000,106.405887 53.000000,107.155887 53.000000,106.405887 53.000000,105.655887" style="fill:rgb(0,0,255);stroke:rgb(0,0,255);stroke-width:0" />\n<polygon points="185.000000,106.405887 182.000000,105.655887 182.000000,106.405887 182.000000,107.155887" style="fill:rgb(0,0,255);stroke:rgb(0,0,255);stroke-width:0" />\n<text x="117.500000" y="105.405887" font-family="Verdana" font-size="3.6" fill="rgb(0,0,255)" text-anchor="middle"  >2X 450 ±0.5</text> </g> 
  Visible = true
  X = 0
  Y = 0
FEATURE [Drawing::FeatureView] dim073
  Rotation = 0
  ViewResult = <g>  <circle cx ="143.000000" cy ="173.200000" r="0.500000" stroke="none" fill="rgb(0,0,255)" /> \n<line x1="134.219074" y1="190.591084" x2="143.285303" y2="172.634942" style="stroke:rgb(0,0,255);stroke-width:0.20" />\n<polygon points="142.714697,173.765058 140.693047,176.105023 141.362548,176.443060 142.032048,176.781097" style="fill:rgb(0,0,255);stroke:rgb(0,0,255);stroke-width:0" />\n<polygon points="143.285303,172.634942 145.306953,170.294977 144.637452,169.956940 143.967952,169.618903" style="fill:rgb(0,0,255);stroke:rgb(0,0,255);stroke-width:0" />\n<line x1="134.219074" y1="190.591084" x2="80.929130" y2="190.591084" style="stroke:rgb(0,0,255);stroke-width:0.20" />\n<text x="106.679308" y="184.029263" font-family="Verdana" font-size="3.6" fill="rgb(0,0,255)" text-anchor="middle"  >14 X S-M3-2-Z1 PEM NUTS</text> </g>
  Visible = true
  X = 0
  Y = 0
FEATURE [Drawing::FeatureView] dimText025
  Rotation = 0
  ViewResult = <g> <text x="83.116404" y="188.900918" font-family="inherit" font-size="3.6" fill="rgb(0,0,255)" text-anchor="inherit"  >INSTALL FROM OTHER SIDE</text> </g>
  Visible = true
  X = 0
  Y = 0
FEATURE [Drawing::FeatureView] centerLines016
  Rotation = 0
  ViewResult = <g transform="scale(0.300000,0.300000)" stroke="rgb(0,0,255)"  stroke-width="1.000000" > <path d="M 260.666667,108.000000 L 260.666667,109.363690 "/>\n<path d="M 260.666667,108.000000 L 267.333333,108.000000 M 274.000000,108.000000 L 294.000000,108.000000 M 300.666667,108.000000 L 307.333333,108.000000 M 314.000000,108.000000 L 334.000000,108.000000 M 340.666667,108.000000 L 347.333333,108.000000 M 354.000000,108.000000 L 356.260504,108.000000 "/>\n<path d="M 260.666667,108.000000 L 260.666667,114.666667 M 260.666667,121.333333 L 260.666667,141.333333 M 260.666667,148.000000 L 260.666667,154.666667 M 260.666667,161.333333 L 260.666667,181.333333 M 260.666667,188.000000 L 260.666667,194.666667 M 260.666667,201.333333 L 260.666667,204.918832 "/>\n<path d="M 260.666667,108.000000 L 260.981532,108.000000 "/> </g> 
  Visible = true
  X = 0
  Y = 0
FEATURE [Drawing::FeatureView] centerLines017
  Rotation = 0
  ViewResult = <g transform="scale(0.300000,0.300000)" stroke="rgb(0,0,255)"  stroke-width="1.000000" > <path d="M 260.666667,108.000000 L 260.666667,108.259006 "/>\n<path d="M 260.666667,108.000000 L 267.333333,108.000000 M 274.000000,108.000000 L 294.000000,108.000000 M 300.666667,108.000000 L 307.333333,108.000000 M 314.000000,108.000000 L 334.000000,108.000000 M 340.666667,108.000000 L 347.333333,108.000000 M 354.000000,108.000000 L 355.708162,108.000000 "/>\n<path d="M 260.666667,108.000000 L 260.666667,108.259006 "/>\n<path d="M 260.666667,108.000000 L 267.333333,108.000000 M 274.000000,108.000000 L 294.000000,108.000000 M 300.666667,108.000000 L 307.333333,108.000000 M 314.000000,108.000000 L 334.000000,108.000000 M 340.666667,108.000000 L 347.333333,108.000000 M 354.000000,108.000000 L 355.708162,108.000000 "/> </g> 
  Visible = true
  X = 0
  Y = 0
FEATURE [Drawing::FeatureView] centerLines018
  Rotation = 0
  ViewResult = <g transform="scale(0.300000,0.300000)" stroke="rgb(0,0,255)"  stroke-width="1.000000" > <path d="M 192.916667,129.000000 L 192.916667,135.666667 M 192.916667,142.333333 L 192.916667,162.333333 M 192.916667,169.000000 L 192.916667,175.666667 M 192.916667,182.333333 L 192.916667,202.333333 M 192.916667,209.000000 L 192.916667,215.666667 M 192.916667,222.333333 L 192.916667,241.419020 "/>\n<path d="M 192.916667,129.000000 L 193.014204,129.000000 "/>\n<path d="M 192.916667,129.000000 L 192.916667,127.425678 "/>\n<path d="M 192.916667,129.000000 L 199.583333,129.000000 M 206.250000,129.000000 L 226.250000,129.000000 M 232.916667,129.000000 L 239.583333,129.000000 M 246.250000,129.000000 L 266.250000,129.000000 M 272.916667,129.000000 L 279.583333,129.000000 M 286.250000,129.000000 L 306.250000,129.000000 M 312.916667,129.000000 L 319.583333,129.000000 M 326.250000,129.000000 L 346.250000,129.000000 M 352.916667,129.000000 L 359.583333,129.000000 M 366.250000,129.000000 L 386.250000,129.000000 M 392.916667,129.000000 L 399.583333,129.000000 M 406.250000,129.000000 L 426.250000,129.000000 M 432.916667,129.000000 L 439.583333,129.000000 M 446.250000,129.000000 L 466.250000,129.000000 M 472.916667,129.000000 L 479.583333,129.000000 M 486.250000,129.000000 L 506.250000,129.000000 M 512.916667,129.000000 L 519.583333,129.000000 M 526.250000,129.000000 L 546.250000,129.000000 M 552.916667,129.000000 L 559.583333,129.000000 M 566.250000,129.000000 L 586.250000,129.000000 M 592.916667,129.000000 L 599.583333,129.000000 M 606.250000,129.000000 L 615.709259,129.000000 "/> </g> 
  Visible = true
  X = 0
  Y = 0
FEATURE [Drawing::FeatureView] centerLines019
  Rotation = 0
  ViewResult = <g transform="scale(0.300000,0.300000)" stroke="rgb(0,0,255)"  stroke-width="1.000000" > <path d="M 615.416667,241.000000 L 615.416667,234.333333 M 615.416667,227.666667 L 615.416667,207.666667 M 615.416667,201.000000 L 615.416667,194.333333 M 615.416667,187.666667 L 615.416667,167.666667 M 615.416667,161.000000 L 615.416667,154.333333 M 615.416667,147.666667 L 615.416667,128.877822 "/>\n<path d="M 615.416667,241.000000 L 614.620150,241.000000 "/>\n<path d="M 615.416667,241.000000 L 615.416667,242.508128 "/>\n<path d="M 615.416667,241.000000 L 608.750000,241.000000 M 602.083333,241.000000 L 582.083333,241.000000 M 575.416667,241.000000 L 568.750000,241.000000 M 562.083333,241.000000 L 542.083333,241.000000 M 535.416667,241.000000 L 528.750000,241.000000 M 522.083333,241.000000 L 502.083333,241.000000 M 495.416667,241.000000 L 488.750000,241.000000 M 482.083333,241.000000 L 462.083333,241.000000 M 455.416667,241.000000 L 448.750000,241.000000 M 442.083333,241.000000 L 422.083333,241.000000 M 415.416667,241.000000 L 408.750000,241.000000 M 402.083333,241.000000 L 382.083333,241.000000 M 375.416667,241.000000 L 368.750000,241.000000 M 362.083333,241.000000 L 342.083333,241.000000 M 335.416667,241.000000 L 328.750000,241.000000 M 322.083333,241.000000 L 302.083333,241.000000 M 295.416667,241.000000 L 288.750000,241.000000 M 282.083333,241.000000 L 262.083333,241.000000 M 255.416667,241.000000 L 248.750000,241.000000 M 242.083333,241.000000 L 222.083333,241.000000 M 215.416667,241.000000 L 208.750000,241.000000 M 202.083333,241.000000 L 193.135216,241.000000 "/> </g> 
  Visible = true
  X = 0
  Y = 0
FEATURE [Drawing::FeatureView] centerLines020
  Rotation = 0
  ViewResult = <g transform="scale(0.300000,0.300000)" stroke="rgb(0,0,255)"  stroke-width="1.000000" > <path d="M 355.916667,204.520000 L 355.916667,197.853333 M 355.916667,191.186667 L 355.916667,171.186667 M 355.916667,164.520000 L 355.916667,157.853333 M 355.916667,151.186667 L 355.916667,131.186667 M 355.916667,124.520000 L 355.916667,117.853333 M 355.916667,111.186667 L 355.916667,107.398185 "/>\n<path d="M 355.916667,204.520000 L 356.077927,204.520000 "/>\n<path d="M 355.916667,204.520000 L 355.916667,204.812877 "/>\n<path d="M 355.916667,204.520000 L 349.250000,204.520000 M 342.583333,204.520000 L 322.583333,204.520000 M 315.916667,204.520000 L 309.250000,204.520000 M 302.583333,204.520000 L 282.583333,204.520000 M 275.916667,204.520000 L 269.250000,204.520000 M 262.583333,204.520000 L 260.780946,204.520000 "/> </g> 
  Visible = true
  X = 0
  Y = 0
FEATURE [Drawing::FeatureView] dim079
  Rotation = 0
  ViewResult = <g> <line x1="50.000000" y1="82.100000" x2="50.000000" y2="86.441858" style="stroke:rgb(0,0,255);stroke-width:0.20" />\n<line x1="57.875000" y1="73.347549" x2="57.875000" y2="86.441858" style="stroke:rgb(0,0,255);stroke-width:0.20" />\n<line x1="50.000000" y1="85.441858" x2="57.875000" y2="85.441858" style="stroke:rgb(0,0,255);stroke-width:0.20" />\n<polygon points="50.000000,85.441858 53.000000,86.191858 53.000000,85.441858 53.000000,84.691858" style="fill:rgb(0,0,255);stroke:rgb(0,0,255);stroke-width:0" />\n<polygon points="57.875000,85.441858 54.875000,84.691858 54.875000,85.441858 54.875000,86.191858" style="fill:rgb(0,0,255);stroke:rgb(0,0,255);stroke-width:0" />\n<text x="41.173007" y="86.568887" font-family="Verdana" font-size="3.6" fill="rgb(0,0,255)" text-anchor="middle"  >2X 26.25</text> </g> 
  Visible = true
  X = 0
  Y = 0
FEATURE [Drawing::FeatureView] dim080
  Rotation = 0
  ViewResult = <g> <line x1="50.000000" y1="82.100000" x2="50.000000" y2="89.347634" style="stroke:rgb(0,0,255);stroke-width:0.20" />\n<line x1="119.090000" y1="67.679049" x2="119.090000" y2="89.347634" style="stroke:rgb(0,0,255);stroke-width:0.20" />\n<line x1="50.000000" y1="88.347634" x2="119.090000" y2="88.347634" style="stroke:rgb(0,0,255);stroke-width:0.20" />\n<polygon points="50.000000,88.347634 53.000000,89.097634 53.000000,88.347634 53.000000,87.597634" style="fill:rgb(0,0,255);stroke:rgb(0,0,255);stroke-width:0" />\n<polygon points="119.090000,88.347634 116.090000,87.597634 116.090000,88.347634 116.090000,89.097634" style="fill:rgb(0,0,255);stroke:rgb(0,0,255);stroke-width:0" />\n<text x="84.545000" y="87.347634" font-family="Verdana" font-size="3.6" fill="rgb(0,0,255)" text-anchor="middle"  >2X 230.3</text> </g> 
  Visible = true
  X = 0
  Y = 0
FEATURE [Drawing::FeatureView] dim075
  Rotation = 0
  ViewResult = <g> <line x1="50.000000" y1="82.100000" x2="50.000000" y2="96.393764" style="stroke:rgb(0,0,255);stroke-width:0.20" />\n<line x1="184.625000" y1="73.347549" x2="184.625000" y2="96.393764" style="stroke:rgb(0,0,255);stroke-width:0.20" />\n<line x1="50.000000" y1="95.393764" x2="184.625000" y2="95.393764" style="stroke:rgb(0,0,255);stroke-width:0.20" />\n<polygon points="50.000000,95.393764 53.000000,96.143764 53.000000,95.393764 53.000000,94.643764" style="fill:rgb(0,0,255);stroke:rgb(0,0,255);stroke-width:0" />\n<polygon points="184.625000,95.393764 181.625000,94.643764 181.625000,95.393764 181.625000,96.143764" style="fill:rgb(0,0,255);stroke:rgb(0,0,255);stroke-width:0" />\n<text x="117.312500" y="94.393764" font-family="Verdana" font-size="3.6" fill="rgb(0,0,255)" text-anchor="middle"  >2X 448.75</text> </g> 
  Visible = true
  X = 0
  Y = 0
FEATURE [Drawing::FeatureView] dim074
  Rotation = 0
  ViewResult = <g> \n  <line x1="152.390000" y1="52.679000" x2="152.390000" y2="89.347634" style="stroke:rgb(0,0,255);stroke-width:0.20" />\n<line x1="119.090000" y1="67.679000" x2="119.090000" y2="89.347634" style="stroke:rgb(0,0,255);stroke-width:0.20" />\n<line x1="152.390000" y1="88.347634" x2="119.090000" y2="88.347634" style="stroke:rgb(0,0,255);stroke-width:0.20" /> \n  <polygon points="119.090000,88.347634 122.090000,89.097634 122.090000,88.347634 122.090000,87.597634" style="fill:rgb(0,0,255);stroke:rgb(0,0,255);stroke-width:0" /><polygon points="152.390000,88.347634 149.390000,87.597634 149.390000,88.347634 149.390000,89.097634" style="fill:rgb(0,0,255);stroke:rgb(0,0,255);stroke-width:0" /> \n  <text x="135.740000" y="87.347634" font-family="Verdana" font-size="3.6" fill="rgb(0,0,255)" text-anchor="middle"  >111.0</text> </g>
  Visible = true
  X = 0
  Y = 0
FEATURE [Drawing::FeatureView] dim081
  Rotation = 0
  ViewResult = <g> \n  <line x1="152.390000" y1="52.679000" x2="152.390000" y2="89.076629" style="stroke:rgb(0,0,255);stroke-width:0.20" />\n<line x1="167.000000" y1="68.939000" x2="167.000000" y2="89.076629" style="stroke:rgb(0,0,255);stroke-width:0.20" />\n<line x1="152.390000" y1="88.076629" x2="167.000000" y2="88.076629" style="stroke:rgb(0,0,255);stroke-width:0.20" /> \n  <polygon points="167.000000,88.076629 164.000000,87.326629 164.000000,88.076629 164.000000,88.826629" style="fill:rgb(0,0,255);stroke:rgb(0,0,255);stroke-width:0" /><polygon points="152.390000,88.076629 155.390000,88.826629 155.390000,88.076629 155.390000,87.326629" style="fill:rgb(0,0,255);stroke:rgb(0,0,255);stroke-width:0" /> \n  <text x="159.695000" y="87.076629" font-family="Verdana" font-size="3.6" fill="rgb(0,0,255)" text-anchor="middle"  >2X 48.7</text> </g>
  Visible = true
  X = 0
  Y = 0
FEATURE [Drawing::FeatureView] dim082
  Rotation = 0
  ViewResult = <g> <line x1="48.900000" y1="81.000000" x2="21.265334" y2="81.000000" style="stroke:rgb(0,0,255);stroke-width:0.20" />\n<line x1="56.827358" y1="72.300000" x2="21.265334" y2="72.300000" style="stroke:rgb(0,0,255);stroke-width:0.20" />\n<line x1="22.265334" y1="81.000000" x2="22.265334" y2="72.300000" style="stroke:rgb(0,0,255);stroke-width:0.20" />\n<polygon points="22.265334,81.000000 23.015334,78.000000 22.265334,78.000000 21.515334,78.000000" style="fill:rgb(0,0,255);stroke:rgb(0,0,255);stroke-width:0" />\n<polygon points="22.265334,72.300000 21.515334,75.300000 22.265334,75.300000 23.015334,75.300000" style="fill:rgb(0,0,255);stroke:rgb(0,0,255);stroke-width:0" />\n<text x="19.266856" y="77.331354" font-family="Verdana" font-size="3.6" fill="rgb(0,0,255)" text-anchor="middle" transform="rotate(-90.000000 19.266856,77.331354)" >2X 29.0</text> </g> 
  Visible = true
  X = 0
  Y = 0
FEATURE [Drawing::FeatureView] dim083
  Rotation = 0
  ViewResult = <g> \n  <line x1="56.827500" y1="72.300000" x2="21.059173" y2="72.300000" style="stroke:rgb(0,0,255);stroke-width:0.20" />\n<line x1="56.827500" y1="38.700000" x2="21.059173" y2="38.700000" style="stroke:rgb(0,0,255);stroke-width:0.20" />\n<line x1="22.059173" y1="72.300000" x2="22.059173" y2="38.700000" style="stroke:rgb(0,0,255);stroke-width:0.20" /> \n  <polygon points="22.059173,38.700000 21.309173,41.700000 22.059173,41.700000 22.809173,41.700000" style="fill:rgb(0,0,255);stroke:rgb(0,0,255);stroke-width:0" /><polygon points="22.059173,72.300000 22.809173,69.300000 22.059173,69.300000 21.309173,69.300000" style="fill:rgb(0,0,255);stroke:rgb(0,0,255);stroke-width:0" /> \n  <text x="21.059173" y="55.500000" font-family="Verdana" font-size="3.6" fill="rgb(0,0,255)" text-anchor="middle" transform="rotate(-90.000000 21.059173,55.500000)" >2X 112.0</text> </g>
  Visible = true
  X = 0
  Y = 0
FEATURE [Drawing::FeatureView] dim084
  Rotation = 0
  ViewResult = <g> \n  <line x1="76.950000" y1="32.400000" x2="35.702952" y2="32.400000" style="stroke:rgb(0,0,255);stroke-width:0.20" />\n<line x1="76.950000" y1="61.356000" x2="35.702952" y2="61.356000" style="stroke:rgb(0,0,255);stroke-width:0.20" />\n<line x1="36.702952" y1="32.400000" x2="36.702952" y2="61.356000" style="stroke:rgb(0,0,255);stroke-width:0.20" /> \n  <polygon points="36.702952,61.356000 37.452952,58.356000 36.702952,58.356000 35.952952,58.356000" style="fill:rgb(0,0,255);stroke:rgb(0,0,255);stroke-width:0" /><polygon points="36.702952,32.400000 35.952952,35.400000 36.702952,35.400000 37.452952,35.400000" style="fill:rgb(0,0,255);stroke:rgb(0,0,255);stroke-width:0" /> \n  <text x="35.702952" y="46.878000" font-family="Verdana" font-size="3.6" fill="rgb(0,0,255)" text-anchor="middle" transform="rotate(-90.000000 35.702952,46.878000)" >2X 96.5</text> </g>
  Visible = true
  X = 0
  Y = 0
FEATURE [Drawing::FeatureView] dim085
  Rotation = 0
  ViewResult = <g> <line x1="50.000000" y1="28.900000" x2="50.000000" y2="22.524741" style="stroke:rgb(0,0,255);stroke-width:0.20" />\n<line x1="78.200000" y1="31.149951" x2="78.200000" y2="22.524741" style="stroke:rgb(0,0,255);stroke-width:0.20" />\n<line x1="50.000000" y1="23.524741" x2="78.200000" y2="23.524741" style="stroke:rgb(0,0,255);stroke-width:0.20" />\n<polygon points="50.000000,23.524741 53.000000,24.274741 53.000000,23.524741 53.000000,22.774741" style="fill:rgb(0,0,255);stroke:rgb(0,0,255);stroke-width:0" />\n<polygon points="78.200000,23.524741 75.200000,22.774741 75.200000,23.524741 75.200000,24.274741" style="fill:rgb(0,0,255);stroke:rgb(0,0,255);stroke-width:0" />\n<text x="64.100000" y="22.524741" font-family="Verdana" font-size="3.6" fill="rgb(0,0,255)" text-anchor="middle"  >2X 94.0</text> </g> 
  Visible = true
  X = 0
  Y = 0
FEATURE [Drawing::FeatureView] dim086
  Rotation = 0
  ViewResult = <g> \n  <line x1="78.200000" y1="31.150000" x2="78.200000" y2="22.524741" style="stroke:rgb(0,0,255);stroke-width:0.20" />\n<line x1="106.775000" y1="31.150000" x2="106.775000" y2="22.524741" style="stroke:rgb(0,0,255);stroke-width:0.20" />\n<line x1="78.200000" y1="23.524741" x2="106.775000" y2="23.524741" style="stroke:rgb(0,0,255);stroke-width:0.20" /> \n  <polygon points="106.775000,23.524741 103.775000,22.774741 103.775000,23.524741 103.775000,24.274741" style="fill:rgb(0,0,255);stroke:rgb(0,0,255);stroke-width:0" /><polygon points="78.200000,23.524741 81.200000,24.274741 81.200000,23.524741 81.200000,22.774741" style="fill:rgb(0,0,255);stroke:rgb(0,0,255);stroke-width:0" /> \n  <text x="92.487500" y="22.524741" font-family="Verdana" font-size="3.6" fill="rgb(0,0,255)" text-anchor="middle"  >2X 95.3</text> </g>
  Visible = true
  X = 0
  Y = 0
FEATURE [Drawing::FeatureView] dim088
  Rotation = 0
  ViewResult = <g> <line x1="48.900000" y1="30.000000" x2="43.791106" y2="30.000000" style="stroke:rgb(0,0,255);stroke-width:0.20" />\n<line x1="76.199858" y1="32.400000" x2="43.791106" y2="32.400000" style="stroke:rgb(0,0,255);stroke-width:0.20" />\n<line x1="44.791106" y1="30.000000" x2="44.791106" y2="32.400000" style="stroke:rgb(0,0,255);stroke-width:0.20" />\n<polygon points="44.791106,30.000000 45.541106,27.000000 44.791106,27.000000 44.041106,27.000000" style="fill:rgb(0,0,255);stroke:rgb(0,0,255);stroke-width:0" />\n<polygon points="44.791106,32.400000 44.041106,35.400000 44.791106,35.400000 45.541106,35.400000" style="fill:rgb(0,0,255);stroke:rgb(0,0,255);stroke-width:0" />\n<text x="46.187669" y="21.077706" font-family="Verdana" font-size="3.6" fill="rgb(0,0,255)" text-anchor="middle" transform="rotate(-90.000000 46.187669,21.077706)" >2X 8.0</text> </g> 
  Visible = true
  X = 0
  Y = 0
FEATURE [Drawing::FeatureView] dim087
  Rotation = 0
  ViewResult = <g>  <circle cx ="106.775000" cy ="32.400000" r="0.500000" stroke="none" fill="rgb(0,0,255)" /> \n<line x1="110.095786" y1="22.019157" x2="106.546486" y2="33.114340" style="stroke:rgb(0,0,255);stroke-width:0.20" />\n<polygon points="107.003514,31.685660 108.631910,29.056815 107.917571,28.828301 107.203231,28.599787" style="fill:rgb(0,0,255);stroke:rgb(0,0,255);stroke-width:0" />\n<polygon points="106.546486,33.114340 104.918090,35.743185 105.632429,35.971699 106.346769,36.200213" style="fill:rgb(0,0,255);stroke:rgb(0,0,255);stroke-width:0" />\n<line x1="110.095786" y1="22.019157" x2="144.536006" y2="22.019157" style="stroke:rgb(0,0,255);stroke-width:0.20" />\n<text x="126.280807" y="12.985657" font-family="Verdana" font-size="3.6" fill="rgb(0,0,255)" text-anchor="middle"  >4X BSOS35M3-12</text> </g>
  Visible = true
  X = 0
  Y = 0
FEATURE [Drawing::FeatureView] dimText026
  Rotation = 0
  ViewResult = <g> <text x="110.848577" y="16.749615" font-family="inherit" font-size="3.6" fill="rgb(0,0,255)" text-anchor="inherit"  >PEM BLIND STANDOFFS</text> </g>
  Visible = true
  X = 0
  Y = 0
FEATURE [Drawing::FeatureView] dimText027
  Rotation = 0
  ViewResult = <g> <text x="110.848577" y="20.701772" font-family="inherit" font-size="3.6" fill="rgb(0,0,255)" text-anchor="inherit"  >INSTALL STANDOFF INSIDE</text> </g>
  Visible = true
  X = 0
  Y = 0
FEATURE [Drawing::FeatureView] dim089
  Rotation = 0
  ViewResult = <g> <line x1="195.100000" y1="81.000000" x2="203.724489" y2="81.000000" style="stroke:rgb(0,0,255);stroke-width:0.20" />\n<line x1="120.460142" y1="66.309000" x2="203.724489" y2="66.309000" style="stroke:rgb(0,0,255);stroke-width:0.20" />\n<line x1="202.724489" y1="81.000000" x2="202.724489" y2="66.309000" style="stroke:rgb(0,0,255);stroke-width:0.20" />\n<polygon points="202.724489,81.000000 203.474489,78.000000 202.724489,78.000000 201.974489,78.000000" style="fill:rgb(0,0,255);stroke:rgb(0,0,255);stroke-width:0" />\n<polygon points="202.724489,66.309000 201.974489,69.309000 202.724489,69.309000 203.474489,69.309000" style="fill:rgb(0,0,255);stroke:rgb(0,0,255);stroke-width:0" />\n<text x="201.724489" y="73.654500" font-family="Verdana" font-size="3.6" fill="rgb(0,0,255)" text-anchor="middle" transform="rotate(-90.000000 201.724489,73.654500)" >2X 49.0</text> </g> 
  Visible = true
  X = 0
  Y = 0
FEATURE [Drawing::FeatureView] dim090
  Rotation = 0
  ViewResult = <g> \n  <line x1="168.370000" y1="66.309000" x2="203.574155" y2="66.309000" style="stroke:rgb(0,0,255);stroke-width:0.20" />\n<line x1="155.020000" y1="51.309000" x2="203.574155" y2="51.309000" style="stroke:rgb(0,0,255);stroke-width:0.20" />\n<line x1="202.574155" y1="66.309000" x2="202.574155" y2="51.309000" style="stroke:rgb(0,0,255);stroke-width:0.20" /> \n  <polygon points="202.574155,51.309000 201.824155,54.309000 202.574155,54.309000 203.324155,54.309000" style="fill:rgb(0,0,255);stroke:rgb(0,0,255);stroke-width:0" /><polygon points="202.574155,66.309000 203.324155,63.309000 202.574155,63.309000 201.824155,63.309000" style="fill:rgb(0,0,255);stroke:rgb(0,0,255);stroke-width:0" /> \n  <text x="201.574155" y="58.809000" font-family="Verdana" font-size="3.6" fill="rgb(0,0,255)" text-anchor="middle" transform="rotate(-90.000000 201.574155,58.809000)" >50.0</text> </g>
  Visible = true
  X = 0
  Y = 0
FEATURE [Drawing::FeatureView] dim091
  Rotation = 0
  ViewResult = <g> \n  <line x1="169.630000" y1="66.309000" x2="211.807814" y2="66.309000" style="stroke:rgb(0,0,255);stroke-width:0.20" />\n<line x1="169.630000" y1="39.609000" x2="211.807814" y2="39.609000" style="stroke:rgb(0,0,255);stroke-width:0.20" />\n<line x1="210.807814" y1="66.309000" x2="210.807814" y2="39.609000" style="stroke:rgb(0,0,255);stroke-width:0.20" /> \n  <polygon points="210.807814,39.609000 210.057814,42.609000 210.807814,42.609000 211.557814,42.609000" style="fill:rgb(0,0,255);stroke:rgb(0,0,255);stroke-width:0" /><polygon points="210.807814,66.309000 211.557814,63.309000 210.807814,63.309000 210.057814,63.309000" style="fill:rgb(0,0,255);stroke:rgb(0,0,255);stroke-width:0" /> \n  <text x="209.807814" y="52.959000" font-family="Verdana" font-size="3.6" fill="rgb(0,0,255)" text-anchor="middle" transform="rotate(-90.000000 209.807814,52.959000)" >2X 89.0</text> </g>
  Visible = true
  X = 0
  Y = 0
FEATURE [Drawing::FeatureView] dim092
  Rotation = 0
  ViewResult = <g>  <circle cx ="167.000000" cy ="39.609000" r="0.500000" stroke="none" fill="rgb(0,0,255)" /> \n<line x1="171.862345" y1="22.132076" x2="166.831138" y2="40.215948" style="stroke:rgb(0,0,255);stroke-width:0.20" />\n<polygon points="167.168862,39.002052 168.695524,36.312851 167.972967,36.111825 167.250410,35.910798" style="fill:rgb(0,0,255);stroke:rgb(0,0,255);stroke-width:0" />\n<polygon points="166.831138,40.215948 165.304476,42.905149 166.027033,43.106175 166.749590,43.307202" style="fill:rgb(0,0,255);stroke:rgb(0,0,255);stroke-width:0" />\n<line x1="171.862345" y1="22.132076" x2="210.480559" y2="22.132076" style="stroke:rgb(0,0,255);stroke-width:0.20" />\n<text x="187.219295" y="15.582788" font-family="Verdana" font-size="3.6" fill="rgb(0,0,255)" text-anchor="middle"  >5 X Ø4.2 THRU</text> </g>
  Visible = true
  X = 0
  Y = 0
FEATURE [Drawing::FeatureView] dimText028
  Rotation = 0
  ViewResult = <g> <text x="173.894882" y="20.325376" font-family="inherit" font-size="3.6" fill="rgb(0,0,255)" text-anchor="inherit"  >Ø8.0, 90 DEG CHAMFER</text> </g>
  Visible = true
  X = 0
  Y = 0
FEATURE [Drawing::FeatureView] dim093
  Rotation = 0
  ViewResult = <g>  <circle cx ="184.625000" cy ="72.300000" r="0.500000" stroke="none" fill="rgb(0,0,255)" /> \n<line x1="188.869541" y1="95.478499" x2="184.453427" y2="71.363080" style="stroke:rgb(0,0,255);stroke-width:0.20" />\n<polygon points="184.796573,73.236920 184.599226,76.322946 185.336959,76.187849 186.074691,76.052753" style="fill:rgb(0,0,255);stroke:rgb(0,0,255);stroke-width:0" />\n<polygon points="184.453427,71.363080 184.650774,68.277054 183.913041,68.412151 183.175309,68.547247" style="fill:rgb(0,0,255);stroke:rgb(0,0,255);stroke-width:0" />\n<line x1="188.869541" y1="95.478499" x2="225.881074" y2="95.478499" style="stroke:rgb(0,0,255);stroke-width:0.20" />\n<text x="210.415735" y="90.613815" font-family="Verdana" font-size="3.6" fill="rgb(0,0,255)" text-anchor="middle"  >4X S-M5-2-Z1 PEM NUT</text> </g>
  Visible = true
  X = 0
  Y = 0
FEATURE [Drawing::FeatureView] dimText029
  Rotation = 0
  ViewResult = <g> <text x="189.940498" y="94.643516" font-family="inherit" font-size="3.6" fill="rgb(0,0,255)" text-anchor="inherit"  >INSTALL FROM OTHER SIDE</text> </g>
  Visible = true
  X = 0
  Y = 0
FEATURE [Drawing::FeatureView] dim094
  Rotation = 0
  ViewResult = <g>  <circle cx ="241.000000" cy ="66.000000" r="0.500000" stroke="none" fill="rgb(0,0,255)" /> \n<line x1="264.957471" y1="112.563631" x2="240.794122" y2="65.599857" style="stroke:rgb(0,0,255);stroke-width:0.20" />\n<polygon points="241.205878,66.400143 241.911491,69.410892 242.578396,69.067763 243.245301,68.724633" style="fill:rgb(0,0,255);stroke:rgb(0,0,255);stroke-width:0" />\n<polygon points="240.794122,65.599857 240.088509,62.589108 239.421604,62.932237 238.754699,63.275367" style="fill:rgb(0,0,255);stroke:rgb(0,0,255);stroke-width:0" />\n<line x1="264.957471" y1="112.563631" x2="217.210700" y2="112.563631" style="stroke:rgb(0,0,255);stroke-width:0.20" />\n<text x="222.900729" y="106.378816" font-family="Verdana" font-size="3.6" fill="rgb(0,0,255)" text-anchor="middle"  >FHA-M3-10 FLUSH HEAD STUD</text> </g>
  Visible = true
  X = 0
  Y = 0
FEATURE [Drawing::FeatureView] dimText030
  Rotation = 0
  ViewResult = <g> <text x="195.687544" y="111.326668" font-family="inherit" font-size="3.6" fill="rgb(0,0,255)" text-anchor="inherit"  >INSTALL STUD TOWARD OTHER SIDE</text> </g>
  Visible = true
  X = 0
  Y = 0
FEATURE [Drawing::FeatureView] dim095
  Rotation = 0
  ViewResult = <g> <line x1="250.500000" y1="81.000000" x2="259.535762" y2="81.000000" style="stroke:rgb(0,0,255);stroke-width:0.20" />\n<line x1="243.450028" y1="66.000000" x2="259.535762" y2="66.000000" style="stroke:rgb(0,0,255);stroke-width:0.20" />\n<line x1="258.535762" y1="81.000000" x2="258.535762" y2="66.000000" style="stroke:rgb(0,0,255);stroke-width:0.20" />\n<polygon points="258.535762,81.000000 259.285762,78.000000 258.535762,78.000000 257.785762,78.000000" style="fill:rgb(0,0,255);stroke:rgb(0,0,255);stroke-width:0" />\n<polygon points="258.535762,66.000000 257.785762,69.000000 258.535762,69.000000 259.285762,69.000000" style="fill:rgb(0,0,255);stroke:rgb(0,0,255);stroke-width:0" />\n<text x="257.535762" y="73.500000" font-family="Verdana" font-size="3.6" fill="rgb(0,0,255)" text-anchor="middle" transform="rotate(-90.000000 257.535762,73.500000)" >50.0</text> </g> 
  Visible = true
  X = 0
  Y = 0
FEATURE [Drawing::FeatureView] dim096
  Rotation = 0
  ViewResult = <g> <line x1="250.000000" y1="78.500000" x2="250.000000" y2="90.479382" style="stroke:rgb(0,0,255);stroke-width:0.20" />\n<line x1="241.000000" y1="67.550042" x2="241.000000" y2="90.479382" style="stroke:rgb(0,0,255);stroke-width:0.20" />\n<line x1="250.000000" y1="89.479382" x2="241.000000" y2="89.479382" style="stroke:rgb(0,0,255);stroke-width:0.20" />\n<polygon points="250.000000,89.479382 247.000000,88.729382 247.000000,89.479382 247.000000,90.229382" style="fill:rgb(0,0,255);stroke:rgb(0,0,255);stroke-width:0" />\n<polygon points="241.000000,89.479382 244.000000,90.229382 244.000000,89.479382 244.000000,88.729382" style="fill:rgb(0,0,255);stroke:rgb(0,0,255);stroke-width:0" />\n<text x="245.500000" y="88.479382" font-family="Verdana" font-size="3.6" fill="rgb(0,0,255)" text-anchor="middle"  >30.0</text> </g> 
  Visible = true
  X = 0
  Y = 0
FEATURE [Drawing::FeatureViewPart] Ortho030  label="Ortho_1_003"
  Direction = (1,0,0)
  HiddenWidth = 0.15
  LineWidth = 0.35
  Rotation = 0
  Scale = 0.3
  ShowHiddenLines = false
  ShowSmoothLines = false
  Tolerance = 0.05
  ViewResult = <blob: 18151 chars omitted>
  Visible = true
  X = 60
  Y = 40
FEATURE [Drawing::FeatureViewPart] Ortho032  label="Ortho_1_004"
  Direction = (0.58,-0.58,-0.58)
  HiddenWidth = 0.15
  LineWidth = 0.35
  Rotation = 180
  Scale = 0.25
  ShowHiddenLines = false
  ShowSmoothLines = true
  Tolerance = 0.05
  ViewResult = <blob: 68477 chars omitted>
  Visible = true
  X = 200
  Y = 65.22
FEATURE [Drawing::FeatureView] dimLine001
  Rotation = 0
  ViewResult = <g   >\n<line x1="100.293535" y1="21.073350" x2="85.500000" y2="43.600000" style="stroke:rgb(0,0,255);stroke-width:0.20" />\n<polygon points="85.500000,43.600000 87.773683,41.504083 87.146780,41.092388 86.519877,40.680693" style="fill:rgb(0,0,255);stroke:rgb(0,0,255);stroke-width:0" />\n<line x1="100.293535" y1="21.073350" x2="160.001359" y2="21.073350" style="stroke:rgb(0,0,255);stroke-width:0.20" />\n</g> 
  Visible = true
  X = 0
  Y = 0
FEATURE [Drawing::FeatureView] dimText031
  Rotation = 0
  ViewResult = <g> <text x="103.415512" y="14.439147" font-family="inherit" font-size="3.6" fill="rgb(0,0,255)" text-anchor="inherit"  >MASK ALL FOUR TABS INSIDE EDGE TOWARD</text> </g>
  Visible = true
  X = 0
  Y = 0
FEATURE [Drawing::FeatureView] dimText032
  Rotation = 0
  ViewResult = <g> <text x="103.014277" y="19.296623" font-family="inherit" font-size="3.6" fill="rgb(0,0,255)" text-anchor="inherit"  >OUTSIDE 7.50 MM WIDE</text> </g>
  Visible = true
  X = 0
  Y = 0
FEATURE [Drawing::FeatureView] dimLine002
  Rotation = 0
  ViewResult = <g   >\n<line x1="120.826544" y1="21.077849" x2="107.400000" y2="112.000000" style="stroke:rgb(0,0,255);stroke-width:0.20" />\n<polygon points="107.400000,112.000000 108.580213,109.141749 107.838260,109.032185 107.096306,108.922620" style="fill:rgb(0,0,255);stroke:rgb(0,0,255);stroke-width:0" />\n<line x1="120.826544" y1="21.077849" x2="135.966971" y2="21.077849" style="stroke:rgb(0,0,255);stroke-width:0.20" />\n</g> 
  Visible = true
  X = 0
  Y = 0
FEATURE [Drawing::FeatureView] dimLine003
  Rotation = 0
  ViewResult = <g   >\n<line x1="111.326668" y1="20.484107" x2="63.600000" y2="112.000000" style="stroke:rgb(0,0,255);stroke-width:0.20" />\n<polygon points="63.600000,112.000000 65.652224,109.686804 64.987224,109.339998 64.322223,108.993192" style="fill:rgb(0,0,255);stroke:rgb(0,0,255);stroke-width:0" />\n<line x1="111.326668" y1="20.484107" x2="142.795007" y2="20.484107" style="stroke:rgb(0,0,255);stroke-width:0.20" />\n</g> 
  Visible = true
  X = 0
  Y = 0
FEATURE [Drawing::FeatureView] dimLine004
  Rotation = 0
  ViewResult = <g   >\n<line x1="118.748446" y1="20.187236" x2="85.500000" y2="180.400000" style="stroke:rgb(0,0,255);stroke-width:0.20" />\n<polygon points="85.500000,180.400000 86.843945,177.614985 86.109592,177.462587 85.375239,177.310189" style="fill:rgb(0,0,255);stroke:rgb(0,0,255);stroke-width:0" />\n<line x1="118.748446" y1="20.187236" x2="130.326420" y2="20.187236" style="stroke:rgb(0,0,255);stroke-width:0.20" />\n</g> 
  Visible = true
  X = 0
  Y = 0
FEATURE [Drawing::FeatureView] dimLine005
  Rotation = 0
  ViewResult = <g   >\n<line x1="206.919168" y1="171.591505" x2="215.909900" y2="147.475852" style="stroke:rgb(0,0,255);stroke-width:0.20" />\n<polygon points="215.909900,147.475852 214.159161,150.024854 214.861911,150.286851 215.564661,150.548849" style="fill:rgb(0,0,255);stroke:rgb(0,0,255);stroke-width:0" />\n<line x1="206.919168" y1="171.591505" x2="143.388749" y2="171.591505" style="stroke:rgb(0,0,255);stroke-width:0.20" />\n</g> 
  Visible = true
  X = 0
  Y = 0
FEATURE [Drawing::FeatureView] dimText033
  Rotation = 0
  ViewResult = <g> <text x="143.982491" y="168.622794" font-family="inherit" font-size="3.6" fill="rgb(0,0,255)" text-anchor="inherit"  >OVERSPRAY ALLOWED INSIDE</text> </g>
  Visible = true
  X = 0
  Y = 0
FEATURE [Drawing::FeatureView] dimLine006
  Rotation = 0
  ViewResult = <g   >\n<line x1="189.403772" y1="37.999503" x2="197.772613" y2="46.583525" style="stroke:rgb(0,0,255);stroke-width:0.20" />\n<polygon points="197.772613,46.583525 196.215405,43.911895 195.678387,44.435452 195.141368,44.959008" style="fill:rgb(0,0,255);stroke:rgb(0,0,255);stroke-width:0" />\n<line x1="189.403772" y1="37.999503" x2="141.310651" y2="37.999503" style="stroke:rgb(0,0,255);stroke-width:0.20" />\n</g> 
  Visible = true
  X = 0
  Y = 0
FEATURE [Drawing::FeatureView] dimText034
  Rotation = 0
  ViewResult = <g> <text x="140.716909" y="36.515147" font-family="inherit" font-size="3.6" fill="rgb(0,0,255)" text-anchor="inherit"  >POWDER COAT OUTSIDE OF CHASSIS</text> </g>
  Visible = true
  X = 0
  Y = 0
FEATURE [Drawing::FeaturePage] Page020  label="Sheet 6"
  EditableTexts = N/A | ELECTRONICS CHASSIS | A | PP-FP0142 | 6 of 8
  Group = -> [Ortho030,Ortho032,dimLine001,dimText031,dimText032,dimLine002,dimLine003,dimLine004,dimLine005,dimText033,dimLine006,dimText034]
  Template = <userpath>/shared-j/Documents/R&D/titleblocks/A4_Landscape_AlephP2.svg
FEATURE [Sketcher::SketchObject] Sketch036
  MapMode = 5
  Placement = pos=(0,0,0) rot=(1,0,0;3.14159rad)
  sketch-geometry (4):
    g0: LineSegment StartX=-100.8 StartY=-433.5 StartZ=0 EndX=-71.8 EndY=-433.5 EndZ=0
    g1: LineSegment StartX=-71.8 StartY=-433.5 StartZ=0 EndX=-71.8 EndY=-466.5 EndZ=0
    g2: LineSegment StartX=-71.8 StartY=-466.5 StartZ=0 EndX=-100.8 EndY=-466.5 EndZ=0
    g3: LineSegment StartX=-100.8 StartY=-466.5 StartZ=0 EndX=-100.8 EndY=-433.5 EndZ=0
  constraints (10):
    c: Coincident(g0,g1)
    c: Coincident(g1,g2)
    c: Coincident(g2,g3)
    c: Coincident(g3,g0)
    c: Horizontal(g0)
    c: Horizontal(g2)
    c: Vertical(g1)
    c: Vertical(g3)
    c: DistanceY(g1) = -33
    c: Distance(g2) = 29
FEATURE [PartDesign::Pocket] Pocket017
  Length = 5
  Profile = -> Sketch036
  Type = 0
FEATURE [Drawing::FeatureView] dimText035
  Rotation = 0
  ViewResult = <g> <text x="145.000000" y="20.000000" font-family="inherit" font-size="3.0" fill="rgb(0,0,0)" text-anchor="inherit"  >IR</text> </g>
  Visible = true
  X = 0
  Y = 0
FEATURE [Drawing::FeatureView] dimText036
  Rotation = 0
  ViewResult = <g> <text x="180.000000" y="20.000000" font-family="inherit" font-size="3.0" fill="rgb(0,0,0)" text-anchor="inherit"  >New part number for silkscreen version</text> </g>
  Visible = true
  X = 0
  Y = 0
FEATURE [Drawing::FeatureView] dimText038
  Rotation = 0
  ViewResult = <g> <text x="160.000000" y="15.000000" font-family="inherit" font-size="4" fill="rgb(0,0,0)" text-anchor="inherit"  >Date</text> </g>
  Visible = true
  X = 0
  Y = 0
FEATURE [Drawing::FeatureView] dimText039
  Rotation = 0
  ViewResult = <g> <text x="160.000000" y="20.000000" font-family="inherit" font-size="3.0" fill="rgb(0,0,0)" text-anchor="inherit"  >6.4.17</text> </g>
  Visible = true
  X = 0
  Y = 0
FEATURE [Drawing::FeatureView] dim056
  Rotation = 0
  ViewResult = <g>  <circle cx ="202.400000" cy ="85.580000" r="0.500000" stroke="none" fill="rgb(0,0,255)" /> \n<line x1="191.177725" y1="64.300957" x2="202.810509" y2="86.358384" style="stroke:rgb(0,0,255);stroke-width:0.20" />\n<polygon points="201.989491,84.801616 201.253423,81.798167 200.590028,82.148033 199.926632,82.497899" style="fill:rgb(0,0,255);stroke:rgb(0,0,255);stroke-width:0" />\n<polygon points="202.810509,86.358384 203.546577,89.361833 204.209972,89.011967 204.873368,88.662101" style="fill:rgb(0,0,255);stroke:rgb(0,0,255);stroke-width:0" />\n<line x1="191.177725" y1="64.300957" x2="166.555163" y2="64.300957" style="stroke:rgb(0,0,255);stroke-width:0.20" />\n<text x="178.866444" y="63.300957" font-family="Verdana" font-size="3.6" fill="rgb(0,0,255)" text-anchor="middle"  >4 X Ø4.0 THRU</text> </g>
  Visible = true
  X = 0
  Y = 0
FEATURE [PartDesign::Chamfer] Chamfer001
  Base = -> Fillet003 [Edge587,Edge586,Edge588,Edge584]
  Size = 1
FEATURE [Sketcher::SketchObject] Sketch037
  ExternalGeometry = -> [Chamfer001]
  MapMode = 5
  Placement = pos=(0,0,170) rot=(0,0,1;0rad)
  Support = -> [Chamfer001]
  sketch-geometry (4):
    g0: LineSegment StartX=-97.6 StartY=477 StartZ=0 EndX=-5 EndY=477 EndZ=0
    g1: LineSegment StartX=-5 StartY=477 StartZ=0 EndX=-5 EndY=471 EndZ=0
    g2: LineSegment StartX=-5 StartY=471 StartZ=0 EndX=-97.6 EndY=471 EndZ=0
    g3: LineSegment StartX=-97.6 StartY=471 StartZ=0 EndX=-97.6 EndY=477 EndZ=0
  constraints (11):
    c: Coincident(g0,g1)
    c: Coincident(g1,g2)
    c: Coincident(g2,g3)
    c: Coincident(g3,g0)
    c: Horizontal(g0)
    c: Horizontal(g2)
    c: Vertical(g1)
    c: Vertical(g3)
    c: Coincident(g0,g-3)
    c: Coincident(g0,g-3)
    c: DistanceY(g1,g1) = 6
FEATURE [PartDesign::Pad] Pad001
  Length = 2.032
  Length2 = 100
  Profile = -> Sketch037
  Reversed = true
  Type = 0
FEATURE [Part::Feature] Pad001001  label="Pad002"
  shape: bbox 100.6 x 480 x 170 mm, 351 faces (baked)
FEATURE [Drawing::FeatureViewPart] Ortho  label="Rear"
  Direction = (-1,0,0)
  HiddenWidth = 0.15
  LineWidth = 0.35
  Rotation = 0
  Scale = 0.25
  ShowHiddenLines = false
  ShowSmoothLines = false
  Source = -> Pad001001
  Tolerance = 0.05
  ViewResult = <blob: 2572 chars omitted>
  Visible = true
  X = 195
  Y = 40
FEATURE [Drawing::FeatureViewPart] Ortho014  label="Ortho_1_002"
  Direction = (0.58,-0.58,0.58)
  HiddenWidth = 0.15
  LineWidth = 0.35
  Rotation = -180
  Scale = 0.25
  ShowHiddenLines = false
  ShowSmoothLines = true
  Source = -> Pad001001
  Tolerance = 0.05
  ViewResult = <blob: 53382 chars omitted>
  Visible = true
  X = 80
  Y = 30
FEATURE [Drawing::FeatureViewPart] Ortho015  label="Front"
  Direction = (1,0,0)
  HiddenWidth = 0.15
  LineWidth = 0.35
  Rotation = 0
  Scale = 0.25
  ShowHiddenLines = false
  ShowSmoothLines = false
  Source = -> Pad001001
  Tolerance = 0.05
  ViewResult = <blob: 15674 chars omitted>
  Visible = true
  X = 40
  Y = 40
FEATURE [Drawing::FeatureViewPart] Ortho012  label="Ortho_1_1"
  Direction = (-0.58,-0.58,0.58)
  HiddenWidth = 0.15
  LineWidth = 0.35
  Rotation = -180
  Scale = 0.25
  ShowHiddenLines = false
  ShowSmoothLines = true
  Source = -> Pad001001
  Tolerance = 0.05
  ViewResult = <blob: 28297 chars omitted>
  Visible = true
  X = 50
  Y = 30
FEATURE [Drawing::FeatureViewPart] Ortho019  label="Ortho_0_0"
  Direction = (0,0,1)
  HiddenWidth = 0.15
  LineWidth = 0.35
  Rotation = -90
  Scale = 0.45
  ShowHiddenLines = false
  ShowSmoothLines = false
  Source = -> Pad001001
  Tolerance = 0.05
  ViewResult = <blob: 13722 chars omitted>
  Visible = true
  X = 240
  Y = 70
FEATURE [Drawing::FeatureViewPart] Ortho034  label="Ortho_0_003"
  Direction = (0,0,1)
  HiddenWidth = 0.15
  LineWidth = 0.35
  Rotation = 180
  Scale = 0.25
  ShowHiddenLines = false
  ShowSmoothLines = false
  Source = -> Pad001001
  Tolerance = 0.05
  ViewResult = <blob: 13719 chars omitted>
  Visible = true
  X = 105
  Y = 40
FEATURE [Drawing::FeatureViewPart] Ortho036  label="Ortho_0_-1"
  Direction = (0,0,-1)
  HiddenWidth = 0.15
  LineWidth = 0.35
  Rotation = 180
  Scale = 0.25
  ShowHiddenLines = false
  ShowSmoothLines = false
  Source = -> Pad001001
  Tolerance = 0.05
  ViewResult = <blob: 13694 chars omitted>
  Visible = true
  X = 240
  Y = 40
FEATURE [Drawing::FeatureView] centerLines021
  Rotation = 0
  ViewResult = <g transform="scale(0.450000,0.450000)" stroke="rgb(0,0,255)"  stroke-width="0.666667" > <path d="M 72.333333,209.155555 L 72.333333,205.616261 "/>\n<path d="M 72.333333,209.155555 L 75.142625,209.155555 "/>\n<path d="M 72.333333,209.155555 L 72.333333,211.984280 "/>\n<path d="M 72.333333,209.155555 L 68.208560,209.155555 "/> </g> 
  Visible = true
  X = 0
  Y = 0
FEATURE [Drawing::FeatureView] centerLines022
  Rotation = 0
  ViewResult = <g transform="scale(0.450000,0.450000)" stroke="rgb(0,0,255)"  stroke-width="0.666667" > <path d="M 72.333333,202.555556 L 72.333333,198.823707 "/>\n<path d="M 72.333333,202.555556 L 68.491583,202.555556 "/>\n<path d="M 72.333333,202.555556 L 72.333333,204.625680 "/>\n<path d="M 72.333333,202.555556 L 75.001114,202.555556 "/> </g> 
  Visible = true
  X = 0
  Y = 0
FEATURE [Drawing::FeatureView] centerLines023
  Rotation = 0
  ViewResult = <g transform="scale(0.450000,0.450000)" stroke="rgb(0,0,255)"  stroke-width="0.666667" > <path d="M 65.833333,187.788856 L 65.833333,190.757550 "/>\n<path d="M 65.833333,187.788856 L 69.199141,187.788856 "/>\n<path d="M 65.833333,187.788856 L 65.833333,184.814065 "/>\n<path d="M 65.833333,187.788856 L 63.963214,187.788856 "/> </g> 
  Visible = true
  X = 0
  Y = 0
FEATURE [Drawing::FeatureView] centerLines024
  Rotation = 0
  ViewResult = <g transform="scale(0.450000,0.450000)" stroke="rgb(0,0,255)"  stroke-width="0.666667" > <path d="M 65.833333,164.855555 L 65.833333,162.313731 "/>\n<path d="M 65.833333,164.855555 L 68.633095,164.855555 "/>\n<path d="M 65.833333,164.855555 L 65.833333,166.700589 "/>\n<path d="M 65.833333,164.855555 L 64.529260,164.855555 "/> </g> 
  Visible = true
  X = 0
  Y = 0
FEATURE [Drawing::FeatureView] centerLines025
  Rotation = 0
  ViewResult = <g transform="scale(0.450000,0.450000)" stroke="rgb(0,0,255)"  stroke-width="0.666667" > <path d="M 65.833333,246.855556 L 65.833333,249.060302 "/>\n<path d="M 65.833333,246.855556 L 68.633095,246.855556 "/>\n<path d="M 65.833333,246.855556 L 65.833333,244.248910 "/>\n<path d="M 65.833333,246.855556 L 63.397168,246.855556 "/> </g> 
  Visible = true
  X = 0
  Y = 0
FEATURE [Drawing::FeatureView] dim097
  Rotation = 0
  ViewResult = <g> \n  <line x1="29.625000" y1="114.077136" x2="29.625000" y2="131.547084" style="stroke:rgb(0,0,255);stroke-width:0.20" />\n<line x1="24.000000" y1="115.920000" x2="24.000000" y2="131.547084" style="stroke:rgb(0,0,255);stroke-width:0.20" />\n<line x1="29.625000" y1="130.547084" x2="24.000000" y2="130.547084" style="stroke:rgb(0,0,255);stroke-width:0.20" /> \n  <polygon points="24.000000,130.547084 21.000000,129.797084 21.000000,130.547084 21.000000,131.297084" style="fill:rgb(0,0,255);stroke:rgb(0,0,255);stroke-width:0" /><polygon points="29.625000,130.547084 32.625000,131.297084 32.625000,130.547084 32.625000,129.797084" style="fill:rgb(0,0,255);stroke:rgb(0,0,255);stroke-width:0" /> \n  <text x="33.269617" y="135.537526" font-family="Verdana" font-size="3" fill="rgb(0,0,255)" text-anchor="middle"  >3X 12.5</text> </g>
  Visible = true
  X = 0
  Y = 0
FEATURE [Drawing::FeatureView] grabPoint001
  Rotation = 0
  ViewResult = <g> <line x1="34.2019117544" y1="41.7326079205" x2="34.2019117544" y2="41.7326079205" style="stroke:rgb(0,0,0);stroke-width:0.01" /> </g> 
  Visible = true
  X = 0
  Y = 0
FEATURE [Drawing::FeatureView] dimText053
  Rotation = 0
  ViewResult = <g> <text x="157.055736" y="125.186336" font-family="inherit" font-size="3" fill="rgb(0,0,0)" text-anchor="inherit"  >6. POWDER COAT WITH CARDINAL COLOR C241-BK109.</text> </g>
  Visible = true
  X = 0
  Y = 0
FEATURE [Drawing::FeatureView] dimText054
  Rotation = 0
  ViewResult = <g> <text x="160.596780" y="129.143974" font-family="inherit" font-size="3" fill="rgb(0,0,0)" text-anchor="inherit"  >COATING THICKNESS: 0.05mm TO 0.12mm</text> </g>
  Visible = true
  X = 0
  Y = 0
FEATURE [Drawing::FeatureView] dim008
  Rotation = 0
  ViewResult = <g>  <circle cx ="189.604000" cy ="86.560000" r="0.500000" stroke="none" fill="rgb(0,0,255)" /> \n<line x1="201.429555" y1="51.686201" x2="189.347092" y2="87.317627" style="stroke:rgb(0,0,255);stroke-width:0.20" />\n<polygon points="189.860908,85.802373 191.534588,83.202124 190.824313,82.961273 190.114038,82.720422" style="fill:rgb(0,0,255);stroke:rgb(0,0,255);stroke-width:0" />\n<polygon points="189.347092,87.317627 187.673412,89.917876 188.383687,90.158727 189.093962,90.399578" style="fill:rgb(0,0,255);stroke:rgb(0,0,255);stroke-width:0" />\n<line x1="201.429555" y1="51.686201" x2="169.171500" y2="51.686201" style="stroke:rgb(0,0,255);stroke-width:0.20" />\n<text x="185.300527" y="50.686201" font-family="Verdana" font-size="3" fill="rgb(0,0,255)" text-anchor="middle"  >Ø4.0 THRU</text> </g>
  Visible = true
  X = 0
  Y = 0
FEATURE [Drawing::FeatureView] dim098
  Rotation = 0
  ViewResult = <g> <line x1="188.403810" y1="86.560000" x2="170.737482" y2="86.560000" style="stroke:rgb(0,0,255);stroke-width:0.20" />\n<line x1="171.737482" y1="79.760000" x2="171.737482" y2="86.560000" style="stroke:rgb(0,0,255);stroke-width:0.20" />\n<polygon points="171.737482,79.760000 172.487482,76.760000 171.737482,76.760000 170.987482,76.760000" style="fill:rgb(0,0,255);stroke:rgb(0,0,255);stroke-width:0" />\n<polygon points="171.737482,86.560000 170.987482,89.560000 171.737482,89.560000 172.487482,89.560000" style="fill:rgb(0,0,255);stroke:rgb(0,0,255);stroke-width:0" />\n<text x="172.837188" y="72.580622" font-family="Verdana" font-size="3" fill="rgb(0,0,255)" text-anchor="middle" transform="rotate(-90.000000 172.837188,72.580622)" >17.0</text> </g> 
  Visible = true
  X = 0
  Y = 0
FEATURE [Drawing::FeatureView] dim099
  Rotation = 0
  ViewResult = <g> \n  <line x1="189.604000" y1="83.760000" x2="189.604000" y2="67.181796" style="stroke:rgb(0,0,255);stroke-width:0.20" />\n<line x1="235.000000" y1="78.960000" x2="235.000000" y2="67.181796" style="stroke:rgb(0,0,255);stroke-width:0.20" />\n<line x1="189.604000" y1="68.181796" x2="235.000000" y2="68.181796" style="stroke:rgb(0,0,255);stroke-width:0.20" /> \n  <polygon points="235.000000,68.181796 232.000000,67.431796 232.000000,68.181796 232.000000,68.931796" style="fill:rgb(0,0,255);stroke:rgb(0,0,255);stroke-width:0" /><polygon points="189.604000,68.181796 192.604000,68.931796 192.604000,68.181796 192.604000,67.431796" style="fill:rgb(0,0,255);stroke:rgb(0,0,255);stroke-width:0" /> \n  <text x="212.302000" y="67.181796" font-family="Verdana" font-size="3" fill="rgb(0,0,255)" text-anchor="middle"  >113.5</text> </g>
  Visible = true
  X = 0
  Y = 0
FEATURE [Drawing::FeatureView] dim100
  Rotation = 0
  ViewResult = <g> <line x1="49.500000" y1="175.000000" x2="42.020514" y2="175.000000" style="stroke:rgb(0,0,255);stroke-width:0.20" />\n<line x1="57.632859" y1="173.200000" x2="42.020514" y2="173.200000" style="stroke:rgb(0,0,255);stroke-width:0.20" />\n<line x1="43.020514" y1="175.000000" x2="43.020514" y2="173.200000" style="stroke:rgb(0,0,255);stroke-width:0.20" />\n<polygon points="43.020514,175.000000 42.270514,178.000000 43.020514,178.000000 43.770514,178.000000" style="fill:rgb(0,0,255);stroke:rgb(0,0,255);stroke-width:0" />\n<polygon points="43.020514,173.200000 43.770514,170.200000 43.020514,170.200000 42.270514,170.200000" style="fill:rgb(0,0,255);stroke:rgb(0,0,255);stroke-width:0" />\n<text x="40.872421" y="174.303463" font-family="Verdana" font-size="3" fill="rgb(0,0,255)" text-anchor="middle" transform="rotate(-90.000000 40.872421,174.303463)" >4X 6 ±0.5</text> </g> 
  Visible = true
  X = 0
  Y = 0
FEATURE [Drawing::FeatureViewPython] text003  # drawing view (typed FeaturePython)
  Rotation = 0
  ViewResult = <g> <text x="27.302604" y="92.381656" font-family="inherit" font-size="40" fill="rgb(255,255,255)" text-anchor="inherit" transform="rotate(90.000000 27.302604,92.381656)" >-</text> </g>
  Visible = true
  X = 0
  Y = 0
  click1_x = 27.3026
  click1_y = 92.3817
  rotation = 90
  text = -
  textRenderer_addText_color = rgb(255,255,255)
  textRenderer_addText_family = inherit
  textRenderer_addText_size = 40
FEATURE [Drawing::FeatureViewPython] text004  # drawing view (typed FeaturePython)
  Rotation = 0
  ViewResult = <g> <text x="29.185542" y="92.617023" font-family="inherit" font-size="40" fill="rgb(255,255,255)" text-anchor="inherit" transform="rotate(90.000000 29.185542,92.617023)" >-</text> </g>
  Visible = true
  X = 0
  Y = 0
  click1_x = 29.1855
  click1_y = 92.617
  rotation = 90
  text = -
  textRenderer_addText_color = rgb(255,255,255)
  textRenderer_addText_family = inherit
  textRenderer_addText_size = 40
FEATURE [Drawing::FeatureViewPython] text005  # drawing view (typed FeaturePython)
  Rotation = 0
  ViewResult = <g> <text x="193.325120" y="171.844551" font-family="inherit" font-size="40" fill="rgb(255,255,255)" text-anchor="inherit" transform="rotate(0.000000 193.325120,171.844551)" >-</text> </g>
  Visible = true
  X = 0
  Y = 0
  click1_x = 193.325
  click1_y = 171.845
  rotation = 0
  text = -
  textRenderer_addText_color = rgb(255,255,255)
  textRenderer_addText_family = inherit
  textRenderer_addText_size = 40
FEATURE [Drawing::FeatureViewPython] text006  # drawing view (typed FeaturePython)
  Rotation = 0
  ViewResult = <g> <text x="203.155211" y="182.038720" font-family="inherit" font-size="80" fill="rgb(255,255,255)" text-anchor="inherit" transform="rotate(0.000000 203.155211,182.038720)" >-</text> </g>
  Visible = true
  X = 0
  Y = 0
  click1_x = 203.155
  click1_y = 182.039
  rotation = 0
  text = -
  textRenderer_addText_color = rgb(255,255,255)
  textRenderer_addText_family = inherit
  textRenderer_addText_size = 80
FEATURE [Drawing::FeatureViewPython] text007  # drawing view (typed FeaturePython)
  Rotation = 0
  ViewResult = <g> <text x="194.428090" y="162.123115" font-family="inherit" font-size="3.5" fill="rgb(0,0,255)" text-anchor="inherit" transform="rotate(0.000000 194.428090,162.123115)" >STANDOFFS</text> </g>
  Visible = true
  X = 0
  Y = 0
  click1_x = 194.428
  click1_y = 162.123
  rotation = 0
  text = STANDOFFS
  textRenderer_addText_color = rgb(0,0,255)
  textRenderer_addText_family = inherit
  textRenderer_addText_size = 3.5
FEATURE [Sketcher::SketchObject] Sketch038
  ExternalGeometry = -> [Pad001001]
  MapMode = 5
  Placement = pos=(0,0,0) rot=(1,0,0;3.14159rad)
  Support = -> [Pad001001]
  sketch-geometry (6):
    g0: LineSegment [constr] StartX=-68.3 StartY=-450 StartZ=0 EndX=-32.3 EndY=-450 EndZ=0
    g1: LineSegment [constr] StartX=-50.3 StartY=-433.95 StartZ=0 EndX=-50.3 EndY=-466.05 EndZ=0
    g2: LineSegment StartX=-64.8 StartY=-433.5 StartZ=0 EndX=-35.8 EndY=-433.5 EndZ=0
    g3: LineSegment StartX=-35.8 StartY=-433.5 StartZ=0 EndX=-35.8 EndY=-466.5 EndZ=0
    g4: LineSegment StartX=-35.8 StartY=-466.5 StartZ=0 EndX=-64.8 EndY=-466.5 EndZ=0
    g5: LineSegment StartX=-64.8 StartY=-466.5 StartZ=0 EndX=-64.8 EndY=-433.5 EndZ=0
  constraints (18):
    c: Coincident(g0,g-8)
    c: Coincident(g0,g-7)
    c: Vertical(g1)
    c: DistanceX(g0,g1) = 18
    c: PointOnObject(g1,g-6)
    c: PointOnObject(g1,g-3)
    c: Coincident(g2,g3)
    c: Coincident(g3,g4)
    c: Coincident(g4,g5)
    c: Coincident(g5,g2)
    c: Horizontal(g2)
    c: Horizontal(g4)
    c: Vertical(g3)
    c: Vertical(g5)
    c: DistanceX(g2) = 29
    c: DistanceY(g3) = -33
    c: Distance(g3,g0) = 16.5
    c: Distance(g2,g1) = 14.5
FEATURE [PartDesign::Pocket] Pocket018
  Length = 5
  Profile = -> Sketch038
  Type = 0
FEATURE [Drawing::FeatureViewPart] Ortho021  label="Ortho_-2_0"
  Direction = (0,0,-1)
  HiddenWidth = 0.15
  LineWidth = 0.35
  Rotation = -90
  Scale = 0.4
  ShowHiddenLines = false
  ShowSmoothLines = false
  Source = -> Pocket018
  Tolerance = 0.05
  ViewResult = <blob: 14267 chars omitted>
  Visible = true
  X = 235
  Y = 120
FEATURE [Drawing::FeatureViewPython] dim101  # drawing view (typed FeaturePython)
  Rotation = 0
  ViewResult = <g> <line x1="46.400000" y1="94.080000" x2="39.347702" y2="94.080000" style="stroke:rgb(0,0,255);stroke-width:0.30" />\n<line x1="46.400000" y1="105.680000" x2="39.347702" y2="105.680000" style="stroke:rgb(0,0,255);stroke-width:0.30" />\n<line x1="40.347702" y1="94.080000" x2="40.347702" y2="105.680000" style="stroke:rgb(0,0,255);stroke-width:0.30" />\n<polygon points="40.347702,94.080000 39.347702,97.080000 40.347702,97.080000 41.347702,97.080000" style="fill:rgb(0,0,255);stroke:rgb(0,0,255);stroke-width:0" />\n<polygon points="40.347702,105.680000 41.347702,102.680000 40.347702,102.680000 39.347702,102.680000" style="fill:rgb(0,0,255);stroke:rgb(0,0,255);stroke-width:0" />\n<text x="38.347702" y="99.880000" font-family="Verdana" font-size="3.0" fill="rgb(0,0,255)" text-anchor="middle" transform="rotate(-90.000000 38.347702,99.880000)" >29.00 </text> </g> 
  Visible = true
  X = 0
  Y = 0
  arrowL1 = 3
  arrowL2 = 0
  arrowW = 2
  arrow_scheme = 0
  autoPlaceOffset = 2
  autoPlaceText = true
  click1_x = 40.3477
  click1_y = 100.817
  click2_x = 40.3477
  click2_y = 100.817
  comma_decimal_place = false
  dimension_line_overshoot = 1
  gap_datum_points = 2
  halfDimension_linear = false
  lineColor = rgb(0,0,255)
  strokeWidth = 0.3
  textFormat_linear = %(value)3.2f 
  textRenderer_color = rgb(0,0,255)
  textRenderer_family = Verdana
  textRenderer_size = 3
  unit_custom_scale = 1
  unit_scheme = 0
FEATURE [Drawing::FeatureViewPython] text012  # drawing view (typed FeaturePython)
  Rotation = 0
  ViewResult = <g> <text x="139.102646" y="78.359132" font-family="inherit" font-size="80" fill="rgb(255,255,255)" text-anchor="inherit" transform="rotate(0.000000 139.102646,78.359132)" >-</text> </g>
  Visible = true
  X = 0
  Y = 0
  click1_x = 139.103
  click1_y = 78.3591
  rotation = 0
  text = -
  textRenderer_addText_color = rgb(255,255,255)
  textRenderer_addText_family = inherit
  textRenderer_addText_size = 80
FEATURE [Drawing::FeatureViewPython] text013  # drawing view (typed FeaturePython)
  Rotation = 0
  ViewResult = <g> <text x="118.905427" y="58.465632" font-family="inherit" font-size="3" fill="rgb(0,0,255)" text-anchor="inherit" transform="rotate(0.000000 118.905427,58.465632)" >SHARP CORNERS ACCEPTABLE</text> </g>
  Visible = true
  X = 0
  Y = 0
  click1_x = 118.905
  click1_y = 58.4656
  rotation = 0
  text = SHARP CORNERS ACCEPTABLE
  textRenderer_addText_color = rgb(0,0,255)
  textRenderer_addText_family = inherit
  textRenderer_addText_size = 3
FEATURE [Drawing::FeatureViewPython] text014  # drawing view (typed FeaturePython)
  Rotation = 0
  ViewResult = <g> <text x="10.983806" y="81.495919" font-family="inherit" font-size="100" fill="rgb(255,255,255)" text-anchor="inherit" transform="rotate(90.000000 10.983806,81.495919)" >-</text> </g>
  Visible = true
  X = 0
  Y = 0
  click1_x = 10.9838
  click1_y = 81.4959
  rotation = 90
  text = -
  textRenderer_addText_color = rgb(255,255,255)
  textRenderer_addText_family = inherit
  textRenderer_addText_size = 100
FEATURE [Drawing::FeatureViewPython] text015  # drawing view (typed FeaturePython)
  Rotation = 0
  ViewResult = <g> <text x="19.221661" y="125.136935" font-family="inherit" font-size="60" fill="rgb(255,255,255)" text-anchor="inherit" transform="rotate(0.000000 19.221661,125.136935)" >-</text> </g>
  Visible = true
  X = 0
  Y = 0
  click1_x = 19.2217
  click1_y = 125.137
  rotation = 0
  text = -
  textRenderer_addText_color = rgb(255,255,255)
  textRenderer_addText_family = inherit
  textRenderer_addText_size = 60
FEATURE [Drawing::FeatureViewPython] text016  # drawing view (typed FeaturePython)
  Rotation = 0
  ViewResult = <g> <text x="16.475709" y="125.529213" font-family="inherit" font-size="80" fill="rgb(255,255,255)" text-anchor="inherit" transform="rotate(0.000000 16.475709,125.529213)" >-</text> </g>
  Visible = true
  X = 0
  Y = 0
  click1_x = 16.4757
  click1_y = 125.529
  rotation = 0
  text = -
  textRenderer_addText_color = rgb(255,255,255)
  textRenderer_addText_family = inherit
  textRenderer_addText_size = 80
FEATURE [Drawing::FeatureViewPython] text017  # drawing view (typed FeaturePython)
  Rotation = 0
  ViewResult = <g> <text x="17.750615" y="112.976292" font-family="inherit" font-size="80" fill="rgb(255,255,255)" text-anchor="inherit" transform="rotate(0.000000 17.750615,112.976292)" >-</text> </g>
  Visible = true
  X = 0
  Y = 0
  click1_x = 17.7506
  click1_y = 112.976
  rotation = 0
  text = -
  textRenderer_addText_color = rgb(255,255,255)
  textRenderer_addText_family = inherit
  textRenderer_addText_size = 80
FEATURE [Drawing::FeatureViewPython] text018  # drawing view (typed FeaturePython)
  Rotation = 0
  ViewResult = <g> <text x="17.260267" y="117.193289" font-family="inherit" font-size="80" fill="rgb(255,255,255)" text-anchor="inherit" transform="rotate(0.000000 17.260267,117.193289)" >-</text> </g>
  Visible = true
  X = 0
  Y = 0
  click1_x = 17.2603
  click1_y = 117.193
  rotation = 0
  text = -
  textRenderer_addText_color = rgb(255,255,255)
  textRenderer_addText_family = inherit
  textRenderer_addText_size = 80
FEATURE [Drawing::FeatureViewPython] text019  # drawing view (typed FeaturePython)
  Rotation = 0
  ViewResult = <g> <text x="18.633243" y="115.526104" font-family="inherit" font-size="60" fill="rgb(255,255,255)" text-anchor="inherit" transform="rotate(0.000000 18.633243,115.526104)" >-</text> </g>
  Visible = true
  X = 0
  Y = 0
  click1_x = 18.6332
  click1_y = 115.526
  rotation = 0
  text = -
  textRenderer_addText_color = rgb(255,255,255)
  textRenderer_addText_family = inherit
  textRenderer_addText_size = 60
FEATURE [Drawing::FeatureViewPython] dim102  # drawing view (typed FeaturePython)
  Rotation = 0
  ViewResult = <g> <line x1="46.400000" y1="94.080000" x2="38.424019" y2="94.080000" style="stroke:rgb(0,0,255);stroke-width:0.30" />\n<line x1="46.400000" y1="105.680000" x2="38.424019" y2="105.680000" style="stroke:rgb(0,0,255);stroke-width:0.30" />\n<line x1="39.424019" y1="94.080000" x2="39.424019" y2="105.680000" style="stroke:rgb(0,0,255);stroke-width:0.30" />\n<polygon points="39.424019,94.080000 38.424019,97.080000 39.424019,97.080000 40.424019,97.080000" style="fill:rgb(0,0,255);stroke:rgb(0,0,255);stroke-width:0" />\n<polygon points="39.424019,105.680000 40.424019,102.680000 39.424019,102.680000 38.424019,102.680000" style="fill:rgb(0,0,255);stroke:rgb(0,0,255);stroke-width:0" />\n<text x="37.424019" y="99.880000" font-family="Verdana" font-size="3.0" fill="rgb(0,0,255)" text-anchor="middle" transform="rotate(-90.000000 37.424019,99.880000)" >29.00 </text> </g> 
  Visible = true
  X = 0
  Y = 0
  arrowL1 = 3
  arrowL2 = 0
  arrowW = 2
  arrow_scheme = 0
  autoPlaceOffset = 2
  autoPlaceText = true
  click1_x = 39.424
  click1_y = 101.894
  click2_x = 39.424
  click2_y = 101.894
  comma_decimal_place = false
  dimension_line_overshoot = 1
  gap_datum_points = 2
  halfDimension_linear = false
  lineColor = rgb(0,0,255)
  strokeWidth = 0.3
  textFormat_linear = %(value)3.2f 
  textRenderer_color = rgb(0,0,255)
  textRenderer_family = Verdana
  textRenderer_size = 3
  unit_custom_scale = 1
  unit_scheme = 0
FEATURE [Drawing::FeatureViewPython] dim103  # drawing view (typed FeaturePython)
  Rotation = 0
  ViewResult = <g> <line x1="46.400000" y1="105.680000" x2="27.946409" y2="105.680000" style="stroke:rgb(0,0,255);stroke-width:0.30" />\n<line x1="53.679987" y1="107.080000" x2="27.946409" y2="107.080000" style="stroke:rgb(0,0,255);stroke-width:0.30" />\n<line x1="28.946409" y1="105.680000" x2="28.946409" y2="107.080000" style="stroke:rgb(0,0,255);stroke-width:0.30" />\n<polygon points="28.946409,105.680000 29.946409,102.680000 28.946409,102.680000 27.946409,102.680000" style="fill:rgb(0,0,255);stroke:rgb(0,0,255);stroke-width:0" />\n<polygon points="28.946409,107.080000 27.946409,110.080000 28.946409,110.080000 29.946409,110.080000" style="fill:rgb(0,0,255);stroke:rgb(0,0,255);stroke-width:0" />\n<text x="26.946409" y="106.380000" font-family="Verdana" font-size="3.0" fill="rgb(0,0,255)" text-anchor="middle" transform="rotate(-90.000000 26.946409,106.380000)" >3.50 </text> </g> 
  Visible = true
  X = 0
  Y = 0
  arrowL1 = 3
  arrowL2 = 0
  arrowW = 2
  arrow_scheme = 0
  autoPlaceOffset = 2
  autoPlaceText = true
  click1_x = 28.9464
  click1_y = 110.041
  click2_x = 28.9464
  click2_y = 110.041
  comma_decimal_place = false
  dimension_line_overshoot = 1
  gap_datum_points = 2
  halfDimension_linear = false
  lineColor = rgb(0,0,255)
  strokeWidth = 0.3
  textFormat_linear = %(value)3.2f 
  textRenderer_color = rgb(0,0,255)
  textRenderer_family = Verdana
  textRenderer_size = 3
  unit_custom_scale = 1
  unit_scheme = 0
FEATURE [Drawing::FeatureViewPython] dim104  # drawing view (typed FeaturePython)
  Rotation = 0
  ViewResult = <g> <line x1="46.400000" y1="94.080000" x2="26.603534" y2="94.080000" style="stroke:rgb(0,0,255);stroke-width:0.30" />\n<line x1="53.499987" y1="92.680000" x2="26.603534" y2="92.680000" style="stroke:rgb(0,0,255);stroke-width:0.30" />\n<line x1="27.603534" y1="94.080000" x2="27.603534" y2="92.680000" style="stroke:rgb(0,0,255);stroke-width:0.30" />\n<polygon points="27.603534,94.080000 26.603534,97.080000 27.603534,97.080000 28.603534,97.080000" style="fill:rgb(0,0,255);stroke:rgb(0,0,255);stroke-width:0" />\n<polygon points="27.603534,92.680000 28.603534,89.680000 27.603534,89.680000 26.603534,89.680000" style="fill:rgb(0,0,255);stroke:rgb(0,0,255);stroke-width:0" />\n<text x="25.603534" y="93.380000" font-family="Verdana" font-size="3.0" fill="rgb(0,0,255)" text-anchor="middle" transform="rotate(-90.000000 25.603534,93.380000)" >3.50 </text> </g> 
  Visible = true
  X = 0
  Y = 0
  arrowL1 = 3
  arrowL2 = 0
  arrowW = 2
  arrow_scheme = 0
  autoPlaceOffset = 2
  autoPlaceText = true
  click1_x = 27.6035
  click1_y = 89.525
  click2_x = 27.6035
  click2_y = 89.525
  comma_decimal_place = false
  dimension_line_overshoot = 1
  gap_datum_points = 2
  halfDimension_linear = false
  lineColor = rgb(0,0,255)
  strokeWidth = 0.3
  textFormat_linear = %(value)3.2f 
  textRenderer_color = rgb(0,0,255)
  textRenderer_family = Verdana
  textRenderer_size = 3
  unit_custom_scale = 1
  unit_scheme = 0
FEATURE [Drawing::FeatureViewPython] text020  # drawing view (typed FeaturePython)
  Rotation = 0
  ViewResult = <g> <text x="45.945650" y="143.406120" font-family="inherit" font-size="50" fill="rgb(255,255,255)" text-anchor="inherit" transform="rotate(0.000000 45.945650,143.406120)" >-</text> </g>
  Visible = true
  X = 0
  Y = 0
  click1_x = 45.9457
  click1_y = 143.406
  rotation = 0
  text = -
  textRenderer_addText_color = rgb(255,255,255)
  textRenderer_addText_family = inherit
  textRenderer_addText_size = 50
FEATURE [Drawing::FeatureViewPython] text021  # drawing view (typed FeaturePython)
  Rotation = 0
  ViewResult = <g> <text x="46.409748" y="142.013828" font-family="inherit" font-size="50" fill="rgb(255,255,255)" text-anchor="inherit" transform="rotate(0.000000 46.409748,142.013828)" >-</text> </g>
  Visible = true
  X = 0
  Y = 0
  click1_x = 46.4097
  click1_y = 142.014
  rotation = 0
  text = -
  textRenderer_addText_color = rgb(255,255,255)
  textRenderer_addText_family = inherit
  textRenderer_addText_size = 50
FEATURE [Drawing::FeatureViewPython] dim105  # drawing view (typed FeaturePython)
  Rotation = 0
  ViewResult = <g> <line x1="61.600000" y1="92.080000" x2="61.600000" y2="60.570265" style="stroke:rgb(0,0,255);stroke-width:0.30" />\n<line x1="48.400000" y1="92.080000" x2="48.400000" y2="60.570265" style="stroke:rgb(0,0,255);stroke-width:0.30" />\n<line x1="61.600000" y1="61.570265" x2="48.400000" y2="61.570265" style="stroke:rgb(0,0,255);stroke-width:0.30" />\n<polygon points="61.600000,61.570265 58.600000,60.570265 58.600000,61.570265 58.600000,62.570265" style="fill:rgb(0,0,255);stroke:rgb(0,0,255);stroke-width:0" />\n<polygon points="48.400000,61.570265 51.400000,62.570265 51.400000,61.570265 51.400000,60.570265" style="fill:rgb(0,0,255);stroke:rgb(0,0,255);stroke-width:0" />\n<text x="55.000000" y="59.570265" font-family="Verdana" font-size="3.0" fill="rgb(0,0,255)" text-anchor="middle" transform="rotate(0.000000 55.000000,59.570265)" >33.00 </text> </g> 
  Visible = true
  X = 0
  Y = 0
  arrowL1 = 3
  arrowL2 = 0
  arrowW = 2
  arrow_scheme = 0
  autoPlaceOffset = 2
  autoPlaceText = true
  click1_x = 51.0507
  click1_y = 61.5703
  click2_x = 51.0507
  click2_y = 61.5703
  comma_decimal_place = false
  dimension_line_overshoot = 1
  gap_datum_points = 2
  halfDimension_linear = false
  lineColor = rgb(0,0,255)
  strokeWidth = 0.3
  textFormat_linear = %(value)3.2f 
  textRenderer_color = rgb(0,0,255)
  textRenderer_family = Verdana
  textRenderer_size = 3
  unit_custom_scale = 1
  unit_scheme = 0
FEATURE [Drawing::FeatureViewPython] tolerance001  # drawing view (typed FeaturePython)
  Rotation = 0
  ViewResult = <g > <text x="64.973647" y="59.570265" font-family="Verdana" font-size="2.4" fill="rgb(0,0,255)" text-anchor="end" transform="rotate(0.000000 64.973647,59.570265)" >-0.0</text> \n <text x="64.973647" y="57.170265" font-family="Verdana" font-size="2.4" fill="rgb(0,0,255)" text-anchor="end" transform="rotate(0.000000 64.973647,57.170265)" >+0.3</text> </g> 
  Visible = true
  X = 0
  Y = 0
  click1_x = 64.9736
  click1_y = 57.7028
  comma_decimal_place = false
  lower_text = 0
  toleranceText_sizeRatio = 0.8
  upper_text = +0.3
FEATURE [Drawing::FeatureViewPython] text022  # drawing view (typed FeaturePython)
  Rotation = 0
  ViewResult = <g> <text x="49.511577" y="145.333844" font-family="inherit" font-size="80" fill="rgb(255,255,255)" text-anchor="inherit" transform="rotate(0.000000 49.511577,145.333844)" >-</text> </g>
  Visible = true
  X = 0
  Y = 0
  click1_x = 49.5116
  click1_y = 145.334
  rotation = 0
  text = -
  textRenderer_addText_color = rgb(255,255,255)
  textRenderer_addText_family = inherit
  textRenderer_addText_size = 80
FEATURE [Drawing::FeatureViewPython] text023  # drawing view (typed FeaturePython)
  Rotation = 0
  ViewResult = <g> <text x="47.249293" y="134.349635" font-family="inherit" font-size="10" fill="rgb(255,255,255)" text-anchor="inherit" transform="rotate(0.000000 47.249293,134.349635)" >-</text> </g>
  Visible = true
  X = 0
  Y = 0
  click1_x = 47.2493
  click1_y = 134.35
  rotation = 0
  text = -
  textRenderer_addText_color = rgb(255,255,255)
  textRenderer_addText_family = inherit
  textRenderer_addText_size = 10
FEATURE [Drawing::FeatureViewPython] text025  # drawing view (typed FeaturePython)
  Rotation = 0
  ViewResult = <g> <text x="60.678040" y="134.598315" font-family="inherit" font-size="10" fill="rgb(255,255,255)" text-anchor="inherit" transform="rotate(0.000000 60.678040,134.598315)" >-</text> </g>
  Visible = true
  X = 0
  Y = 0
  click1_x = 60.678
  click1_y = 134.598
  rotation = 0
  text = -
  textRenderer_addText_color = rgb(255,255,255)
  textRenderer_addText_family = inherit
  textRenderer_addText_size = 10
FEATURE [Drawing::FeatureViewPython] text024  # drawing view (typed FeaturePython)
  Rotation = 0
  ViewResult = <g> <text x="59.965711" y="120.137326" font-family="inherit" font-size="10" fill="rgb(255,255,255)" text-anchor="inherit" transform="rotate(0.000000 59.965711,120.137326)" >-</text> </g>
  Visible = true
  X = 0
  Y = 0
  click1_x = 59.9657
  click1_y = 120.137
  rotation = 0
  text = -
  textRenderer_addText_color = rgb(255,255,255)
  textRenderer_addText_family = inherit
  textRenderer_addText_size = 10
FEATURE [Drawing::FeatureViewPython] text026  # drawing view (typed FeaturePython)
  Rotation = 0
  ViewResult = <g> <text x="58.365992" y="123.210054" font-family="inherit" font-size="15" fill="rgb(255,255,255)" text-anchor="inherit" transform="rotate(0.000000 58.365992,123.210054)" >-</text> </g>
  Visible = true
  X = 0
  Y = 0
  click1_x = 58.366
  click1_y = 123.21
  rotation = 0
  text = -
  textRenderer_addText_color = rgb(255,255,255)
  textRenderer_addText_family = inherit
  textRenderer_addText_size = 15
FEATURE [Drawing::FeatureViewPython] text027  # drawing view (typed FeaturePython)
  Rotation = 0
  ViewResult = <g> <text x="60.710135" y="120.850073" font-family="inherit" font-size="5" fill="rgb(255,255,255)" text-anchor="inherit" transform="rotate(0.000000 60.710135,120.850073)" >-</text> </g>
  Visible = true
  X = 0
  Y = 0
  click1_x = 60.7101
  click1_y = 120.85
  rotation = 0
  text = -
  textRenderer_addText_color = rgb(255,255,255)
  textRenderer_addText_family = inherit
  textRenderer_addText_size = 5
FEATURE [Drawing::FeatureViewPython] text028  # drawing view (typed FeaturePython)
  Rotation = 0
  ViewResult = <g> <text x="56.168979" y="107.459330" font-family="inherit" font-size="20" fill="rgb(255,255,255)" text-anchor="inherit" transform="rotate(90.000000 56.168979,107.459330)" >-</text> </g>
  Visible = true
  X = 0
  Y = 0
  click1_x = 56.169
  click1_y = 107.459
  rotation = 90
  text = -
  textRenderer_addText_color = rgb(255,255,255)
  textRenderer_addText_family = inherit
  textRenderer_addText_size = 20
FEATURE [Drawing::FeatureViewPython] text029  # drawing view (typed FeaturePython)
  Rotation = 0
  ViewResult = <g> <text x="58.673053" y="106.552682" font-family="inherit" font-size="10" fill="rgb(255,255,255)" text-anchor="inherit" transform="rotate(90.000000 58.673053,106.552682)" >-</text> </g>
  Visible = true
  X = 0
  Y = 0
  click1_x = 58.6731
  click1_y = 106.553
  rotation = 90
  text = -
  textRenderer_addText_color = rgb(255,255,255)
  textRenderer_addText_family = inherit
  textRenderer_addText_size = 10
FEATURE [Drawing::FeatureViewPython] text030  # drawing view (typed FeaturePython)
  Rotation = 0
  ViewResult = <g> <text x="58.587735" y="113.389996" font-family="inherit" font-size="10" fill="rgb(255,255,255)" text-anchor="inherit" transform="rotate(90.000000 58.587735,113.389996)" >-</text> </g>
  Visible = true
  X = 0
  Y = 0
  click1_x = 58.5877
  click1_y = 113.39
  rotation = 90
  text = -
  textRenderer_addText_color = rgb(255,255,255)
  textRenderer_addText_family = inherit
  textRenderer_addText_size = 10
FEATURE [Drawing::FeatureViewPython] text031  # drawing view (typed FeaturePython)
  Rotation = 0
  ViewResult = <g> <text x="60.092421" y="118.996932" font-family="inherit" font-size="10" fill="rgb(255,255,255)" text-anchor="inherit" transform="rotate(0.000000 60.092421,118.996932)" >-</text> </g>
  Visible = true
  X = 0
  Y = 0
  click1_x = 60.0924
  click1_y = 118.997
  rotation = 0
  text = -
  textRenderer_addText_color = rgb(255,255,255)
  textRenderer_addText_family = inherit
  textRenderer_addText_size = 10
FEATURE [Drawing::FeaturePage] Page018  label="Sheet 4"
  EditableTexts = N/A | ELECTRONICS CHASSIS | A | PP-FP0142 | 4 of 8
  Group = -> [Ortho021,dim021,dim033,dim034,dim035,dim036,centerLines004,centerLines005,centerLines006,dim037,dim038,dim039,dim041,dim042,dim044,dim045,dim046,dim047,dim048,dim040,dim050,dim052,centerLines007,centerLines008,dim043,dim049,centerLines009,centerLines010,dimText010,dim054,dim055,dim056,dim057,dim059,dimText021,dimText022,dimText024,dim051,dim053,dimText023,dim058,dim060,dim061,dim062,dim063,dim064,+36 more]
  Template = <userpath>/shared-j/Documents/R&D/titleblocks/A4_Landscape_AlephP2.svg
FEATURE [Drawing::FeatureView] dim106
  Rotation = 0
  ViewResult = <g> \n  <line x1="185.000000" y1="124.433000" x2="185.000000" y2="118.816289" style="stroke:rgb(0,0,255);stroke-width:0.25" />\n<line x1="192.200000" y1="130.367000" x2="192.200000" y2="118.816289" style="stroke:rgb(0,0,255);stroke-width:0.25" />\n<line x1="185.000000" y1="119.816289" x2="192.200000" y2="119.816289" style="stroke:rgb(0,0,255);stroke-width:0.25" /> \n  <polygon points="192.200000,119.816289 190.200000,118.816289 190.200000,119.816289 190.200000,120.816289" style="fill:rgb(0,0,255);stroke:rgb(0,0,255);stroke-width:0" /><polygon points="185.000000,119.816289 187.000000,120.816289 187.000000,119.816289 187.000000,118.816289" style="fill:rgb(0,0,255);stroke:rgb(0,0,255);stroke-width:0" /> \n  <text x="191.501185" y="117.745571" font-family="inherit" font-size="3" fill="rgb(0,0,255)" text-anchor="middle"  >24 ±0.5</text> </g>
  Visible = true
  X = 0
  Y = 0
FEATURE [Drawing::FeatureView] dim107
  Rotation = 0
  ViewResult = <g> \n  <line x1="51.800000" y1="135.633000" x2="51.800000" y2="141.090546" style="stroke:rgb(0,0,255);stroke-width:0.25" />\n<line x1="59.000000" y1="128.433000" x2="59.000000" y2="141.090546" style="stroke:rgb(0,0,255);stroke-width:0.25" />\n<line x1="51.800000" y1="140.090546" x2="59.000000" y2="140.090546" style="stroke:rgb(0,0,255);stroke-width:0.25" /> \n  <polygon points="59.000000,140.090546 57.000000,139.090546 57.000000,140.090546 57.000000,141.090546" style="fill:rgb(0,0,255);stroke:rgb(0,0,255);stroke-width:0" /><polygon points="51.800000,140.090546 53.800000,141.090546 53.800000,140.090546 53.800000,139.090546" style="fill:rgb(0,0,255);stroke:rgb(0,0,255);stroke-width:0" /> \n  <text x="65.589815" y="138.028365" font-family="inherit" font-size="3" fill="rgb(0,0,255)" text-anchor="middle"  >24 ±0.5</text> </g>
  Visible = true
  X = 0
  Y = 0
FEATURE [Drawing::FeaturePage] Page019  label="Sheet 5"
  EditableTexts = N/A | ELECTRONICS CHASSIS | A | PP-FP0142 | 5 of 8
  Group = -> [Ortho023,Ortho025,Ortho027,centerLines011,dim068,dim069,dim070,dim071,centerLines012,centerLines013,centerLines014,centerLines015,dim076,dim072,dim077,dim078,dim073,dimText025,centerLines016,centerLines017,centerLines018,centerLines019,centerLines020,dim079,dim080,dim075,dim074,dim081,dim082,dim083,dim084,dim085,dim086,dim088,dim087,dimText026,dimText027,dim089,dim090,dim091,dim092,dimText028,+9 more]
  Template = <userpath>/shared-j/Documents/R&D/titleblocks/A4_Landscape_AlephP2.svg
FEATURE [Drawing::FeatureView] dimLine007
  Rotation = 0
  ViewResult = <g   >\n<line x1="200.000000" y1="25.000000" x2="194.250000" y2="40.000000" style="stroke:rgb(0,0,255);stroke-width:0.25" />\n<polygon points="194.250000,40.000000 195.899618,38.490444 194.965872,38.132508 194.032126,37.774572" style="fill:rgb(0,0,255);stroke:rgb(0,0,255);stroke-width:0" />\n<line x1="200.000000" y1="25.000000" x2="250.000000" y2="25.000000" style="stroke:rgb(0,0,255);stroke-width:0.25" />\n</g> 
  Visible = true
  X = 0
  Y = 0
FEATURE [Drawing::FeatureView] dimText013
  Rotation = 0
  ViewResult = <g> <text x="199.823912" y="23.805737" font-family="inherit" font-size="3" fill="rgb(0,0,0)" text-anchor="inherit" transform="rotate(0.000000 199.823912,23.805737)" >Weld and grind 4 edges to mimic bend radius</text> </g>
  Visible = true
  X = 0
  Y = 0
FEATURE [Drawing::FeaturePage] Page  label="Sheet 2"
  EditableTexts = N/A | ELECTRONICS CHASSIS | A | PP-FP0142 | 2 of 8
  Group = -> [Ortho015,Ortho,dim001,dim002,dim003,dim004,dim005,dim006,dim007,Ortho034,Ortho036,dimLine007,dimText013]
  Template = <userpath>/shared-j/Documents/R&D/titleblocks/A4_Landscape_AlephP2.svg
FEATURE [Drawing::FeatureViewPart] View
  Direction = (0,0,1)
  HiddenWidth = 0.15
  LineWidth = 0.35
  Rotation = 270
  Scale = 0.5
  ShowHiddenLines = false
  ShowSmoothLines = false
  Source = -> Pocket018
  Tolerance = 0.05
  ViewResult = <blob: 14439 chars omitted>
  Visible = true
  X = 250
  Y = 80
FEATURE [Drawing::FeatureViewPart] Ortho037  label="Ortho_0_004"
  Direction = (0,0,-1)
  HiddenWidth = 0.15
  LineWidth = 0.35
  Rotation = -90
  Scale = 0.5
  ShowHiddenLines = false
  ShowSmoothLines = false
  Source = -> Pocket018
  Tolerance = 0.05
  ViewResult = <blob: 14952 chars omitted>
  Visible = true
  X = 260
  Y = 106
FEATURE [Drawing::FeatureView] dimText014
  Rotation = 0
  ViewResult = <g> <text x="75.862918" y="35.824156" font-family="inherit" font-size="5" fill="rgb(0,0,0)" text-anchor="inherit" transform="rotate(0.000000 75.862918,35.824156)" >GRAPHICS NOT TO SCALE. FOR REFERENCE ONLY</text> </g>
  Visible = true
  X = 0
  Y = 0
FEATURE [Drawing::FeatureViewSymbol] Symbol002
  Rotation = 90
  Scale = 0.5
  Symbol = <blob: 2762 chars omitted>
  ViewResult = <blob: 2824 chars omitted>
  Visible = true
  X = 252
  Y = 40
FEATURE [Drawing::FeatureViewSymbol] Symbol
  Rotation = 90
  Scale = 0.5
  Symbol = <blob: 9260 chars omitted>
  ViewResult = <blob: 9324 chars omitted>
  Visible = true
  X = 160
  Y = 48.5
FEATURE [Drawing::FeatureView] grabPoint002
  Rotation = 0
  ViewResult = <g> <line x1="51.8923432126" y1="95.8822991339" x2="51.8923432126" y2="95.8822991339" style="stroke:rgb(0,0,0);stroke-width:0.01" /> </g> 
  Visible = true
  X = 0
  Y = 0
FEATURE [Drawing::FeatureView] grabPoint003
  Rotation = 0
  ViewResult = <g> <line x1="87.9799118426" y1="114.057789904" x2="87.9799118426" y2="114.057789904" style="stroke:rgb(0,0,0);stroke-width:0.01" /> </g> 
  Visible = true
  X = 0
  Y = 0
FEATURE [Drawing::FeatureView] dim108
  Rotation = 0
  ViewResult = <g> <line x1="39.825000" y1="82.650000" x2="39.825000" y2="74.376298" style="stroke:rgb(0,0,255);stroke-width:0.25" />\n<line x1="51.892343" y1="93.882280" x2="51.892343" y2="74.376298" style="stroke:rgb(0,0,255);stroke-width:0.25" />\n<line x1="39.825000" y1="75.376298" x2="51.892343" y2="75.376298" style="stroke:rgb(0,0,255);stroke-width:0.25" />\n<polygon points="39.825000,75.376298 41.825000,76.376298 41.825000,75.376298 41.825000,74.376298" style="fill:rgb(0,0,255);stroke:rgb(0,0,255);stroke-width:0" />\n<polygon points="51.892343,75.376298 49.892343,74.376298 49.892343,75.376298 49.892343,76.376298" style="fill:rgb(0,0,255);stroke:rgb(0,0,255);stroke-width:0" />\n<text x="45.858672" y="73.376298" font-family="inherit" font-size="3" fill="rgb(0,0,0)" text-anchor="middle"  >28 ±2</text> </g> 
  Visible = true
  X = 0
  Y = 0
FEATURE [Drawing::FeatureView] dim109
  Rotation = 0
  ViewResult = <g> <line x1="89.980149" y1="114.057790" x2="101.424422" y2="114.057790" style="stroke:rgb(0,0,255);stroke-width:0.25" />\n<line x1="100.424422" y1="130.300000" x2="100.424422" y2="114.057790" style="stroke:rgb(0,0,255);stroke-width:0.25" />\n<polygon points="100.424422,130.300000 101.424422,128.300000 100.424422,128.300000 99.424422,128.300000" style="fill:rgb(0,0,255);stroke:rgb(0,0,255);stroke-width:0" />\n<polygon points="100.424422,114.057790 99.424422,116.057790 100.424422,116.057790 101.424422,116.057790" style="fill:rgb(0,0,255);stroke:rgb(0,0,255);stroke-width:0" />\n<text x="98.424422" y="122.178895" font-family="inherit" font-size="3" fill="rgb(0,0,0)" text-anchor="middle" transform="rotate(-90.000000 98.424422,122.178895)" >30 ±2</text> </g> 
  Visible = true
  X = 0
  Y = 0
FEATURE [Drawing::FeatureView] grabPoint004
  Rotation = 0
  ViewResult = <g> <line x1="197.299071168" y1="90.2609696332" x2="197.299071168" y2="90.2609696332" style="stroke:rgb(0,0,0);stroke-width:0.01" /> </g> 
  Visible = true
  X = 0
  Y = 0
FEATURE [Drawing::FeatureView] grabPoint006
  Rotation = 0
  ViewResult = <g> <line x1="177.434946996" y1="89.5227758295" x2="177.434946996" y2="89.5227758295" style="stroke:rgb(0,0,0);stroke-width:0.01" /> </g> 
  Visible = true
  X = 0
  Y = 0
FEATURE [Drawing::FeatureView] grabPoint007
  Rotation = 0
  ViewResult = <g> <line x1="199.379435524" y1="91.670248713" x2="199.379435524" y2="91.670248713" style="stroke:rgb(0,0,0);stroke-width:0.01" /> </g> 
  Visible = true
  X = 0
  Y = 0
FEATURE [Drawing::FeatureView] dim110
  Rotation = 0
  ViewResult = <g> \n  <line x1="177.434947" y1="87.522776" x2="177.434947" y2="74.351551" style="stroke:rgb(0,0,255);stroke-width:0.25" />\n<line x1="179.700000" y1="84.750000" x2="179.700000" y2="74.351551" style="stroke:rgb(0,0,255);stroke-width:0.25" />\n<line x1="177.434947" y1="75.351551" x2="179.700000" y2="75.351551" style="stroke:rgb(0,0,255);stroke-width:0.25" /> \n  <polygon points="179.700000,75.351551 181.700000,76.351551 181.700000,75.351551 181.700000,74.351551" style="fill:rgb(0,0,255);stroke:rgb(0,0,255);stroke-width:0" /><polygon points="177.434947,75.351551 175.434947,74.351551 175.434947,75.351551 175.434947,76.351551" style="fill:rgb(0,0,255);stroke:rgb(0,0,255);stroke-width:0" /> \n  <text x="178.567473" y="73.351551" font-family="inherit" font-size="3" fill="rgb(0,0,0)" text-anchor="middle"  >6.0 ±1</text> </g>
  Visible = true
  X = 0
  Y = 0
FEATURE [Drawing::FeatureView] dim111
  Rotation = 0
  ViewResult = <g> \n  <line x1="195.000000" y1="84.750000" x2="195.000000" y2="73.732241" style="stroke:rgb(0,0,255);stroke-width:0.25" />\n<line x1="197.299071" y1="88.260970" x2="197.299071" y2="73.732241" style="stroke:rgb(0,0,255);stroke-width:0.25" />\n<line x1="195.000000" y1="74.732241" x2="197.299071" y2="74.732241" style="stroke:rgb(0,0,255);stroke-width:0.25" /> \n  <polygon points="197.299071,74.732241 199.299071,75.732241 199.299071,74.732241 199.299071,73.732241" style="fill:rgb(0,0,255);stroke:rgb(0,0,255);stroke-width:0" /><polygon points="195.000000,74.732241 193.000000,73.732241 193.000000,74.732241 193.000000,75.732241" style="fill:rgb(0,0,255);stroke:rgb(0,0,255);stroke-width:0" /> \n  <text x="196.149536" y="72.732241" font-family="inherit" font-size="3" fill="rgb(0,0,0)" text-anchor="middle"  >6.0 ±1</text> </g>
  Visible = true
  X = 0
  Y = 0
FEATURE [Drawing::FeatureView] dim112
  Rotation = 0
  ViewResult = <g> \n  <line x1="197.299071" y1="92.260970" x2="197.299071" y2="110.376807" style="stroke:rgb(0,0,255);stroke-width:0.25" />\n<line x1="199.379436" y1="93.670249" x2="199.379436" y2="110.376807" style="stroke:rgb(0,0,255);stroke-width:0.25" />\n<line x1="197.299071" y1="109.376807" x2="199.379436" y2="109.376807" style="stroke:rgb(0,0,255);stroke-width:0.25" /> \n  <polygon points="199.379436,109.376807 201.379436,110.376807 201.379436,109.376807 201.379436,108.376807" style="fill:rgb(0,0,255);stroke:rgb(0,0,255);stroke-width:0" /><polygon points="197.299071,109.376807 195.299071,108.376807 195.299071,109.376807 195.299071,110.376807" style="fill:rgb(0,0,255);stroke:rgb(0,0,255);stroke-width:0" /> \n  <text x="204.593074" y="107.406354" font-family="inherit" font-size="3" fill="rgb(0,0,0)" text-anchor="middle"  >2X 3.0</text> </g>
  Visible = true
  X = 0
  Y = 0
FEATURE [Drawing::FeatureView] grabPoint005
  Rotation = 0
  ViewResult = <g> <line x1="148.828293985" y1="102.731034786" x2="148.828293985" y2="102.731034786" style="stroke:rgb(0,0,0);stroke-width:0.01" /> </g> 
  Visible = true
  X = 0
  Y = 0
FEATURE [Drawing::FeatureView] dim113
  Rotation = 0
  ViewResult = <g> \n  <line x1="10.000000" y1="79.500000" x2="10.000000" y2="58.614534" style="stroke:rgb(0,0,255);stroke-width:0.25" />\n<line x1="148.828294" y1="100.731035" x2="148.828294" y2="58.614534" style="stroke:rgb(0,0,255);stroke-width:0.25" />\n<line x1="10.000000" y1="59.614534" x2="148.828294" y2="59.614534" style="stroke:rgb(0,0,255);stroke-width:0.25" /> \n  <polygon points="148.828294,59.614534 146.828294,58.614534 146.828294,59.614534 146.828294,60.614534" style="fill:rgb(0,0,255);stroke:rgb(0,0,255);stroke-width:0" /><polygon points="10.000000,59.614534 12.000000,60.614534 12.000000,59.614534 12.000000,58.614534" style="fill:rgb(0,0,255);stroke:rgb(0,0,255);stroke-width:0" /> \n  <text x="79.414147" y="57.614534" font-family="inherit" font-size="3" fill="rgb(0,0,0)" text-anchor="middle"  >280 ±2</text> </g>
  Visible = true
  X = 0
  Y = 0
FEATURE [Drawing::FeatureView] grabPoint008
  Rotation = 0
  ViewResult = <g> <line x1="165.117231514" y1="88.1693954689" x2="165.117231514" y2="88.1693954689" style="stroke:rgb(0,0,0);stroke-width:0.01" /> </g> 
  Visible = true
  X = 0
  Y = 0
FEATURE [Drawing::FeatureView] grabPoint009
  Rotation = 0
  ViewResult = <g> <line x1="165.117231514" y1="118.026758934" x2="165.117231514" y2="118.026758934" style="stroke:rgb(0,0,0);stroke-width:0.01" /> </g> 
  Visible = true
  X = 0
  Y = 0
FEATURE [Drawing::FeatureViewSymbol] Symbol003
  Rotation = 90
  Scale = 0.5
  Symbol = <blob: 11931 chars omitted>
  ViewResult = <blob: 11993 chars omitted>
  Visible = true
  X = 230
  Y = 53
FEATURE [Drawing::FeatureView] dim114
  Rotation = 0
  ViewResult = <g> \n  <line x1="167.117232" y1="118.026759" x2="176.959824" y2="118.026759" style="stroke:rgb(0,0,255);stroke-width:0.25" />\n<line x1="13.500000" y1="130.300000" x2="176.959824" y2="130.300000" style="stroke:rgb(0,0,255);stroke-width:0.25" />\n<line x1="175.959824" y1="118.026759" x2="175.959824" y2="130.300000" style="stroke:rgb(0,0,255);stroke-width:0.25" /> \n  <polygon points="175.959824,130.300000 176.959824,128.300000 175.959824,128.300000 174.959824,128.300000" style="fill:rgb(0,0,255);stroke:rgb(0,0,255);stroke-width:0" /><polygon points="175.959824,118.026759 174.959824,120.026759 175.959824,120.026759 176.959824,120.026759" style="fill:rgb(0,0,255);stroke:rgb(0,0,255);stroke-width:0" /> \n  <text x="175.737636" y="136.662563" font-family="inherit" font-size="3" fill="rgb(0,0,0)" text-anchor="middle" transform="rotate(-90.000000 175.737636,136.662563)" >20.3 ±2</text> </g>
  Visible = true
  X = 0
  Y = 0
FEATURE [Drawing::FeatureView] dim115
  Rotation = 0
  ViewResult = <g> \n  <line x1="13.500000" y1="80.000000" x2="174.931788" y2="80.000000" style="stroke:rgb(0,0,255);stroke-width:0.25" />\n<line x1="167.117232" y1="88.169395" x2="174.931788" y2="88.169395" style="stroke:rgb(0,0,255);stroke-width:0.25" />\n<line x1="173.931788" y1="80.000000" x2="173.931788" y2="88.169395" style="stroke:rgb(0,0,255);stroke-width:0.25" /> \n  <polygon points="173.931788,88.169395 174.931788,86.169395 173.931788,86.169395 172.931788,86.169395" style="fill:rgb(0,0,255);stroke:rgb(0,0,255);stroke-width:0" /><polygon points="173.931788,80.000000 172.931788,82.000000 173.931788,82.000000 174.931788,82.000000" style="fill:rgb(0,0,255);stroke:rgb(0,0,255);stroke-width:0" /> \n  <text x="171.529551" y="72.539366" font-family="inherit" font-size="3" fill="rgb(0,0,0)" text-anchor="middle" transform="rotate(-90.000000 171.529551,72.539366)" >20.3 ±2</text> </g>
  Visible = true
  X = 0
  Y = 0
FEATURE [Drawing::FeatureView] dim116
  Rotation = 0
  ViewResult = <g> \n  <line x1="163.117232" y1="88.169395" x2="140.310051" y2="88.169395" style="stroke:rgb(0,0,255);stroke-width:0.25" />\n<line x1="163.117232" y1="118.026759" x2="140.310051" y2="118.026759" style="stroke:rgb(0,0,255);stroke-width:0.25" />\n<line x1="141.310051" y1="88.169395" x2="141.310051" y2="118.026759" style="stroke:rgb(0,0,255);stroke-width:0.25" /> \n  <polygon points="141.310051,118.026759 142.310051,116.026759 141.310051,116.026759 140.310051,116.026759" style="fill:rgb(0,0,255);stroke:rgb(0,0,255);stroke-width:0" /><polygon points="141.310051,88.169395 140.310051,90.169395 141.310051,90.169395 142.310051,90.169395" style="fill:rgb(0,0,255);stroke:rgb(0,0,255);stroke-width:0" /> \n  <text x="139.310051" y="103.098077" font-family="inherit" font-size="3" fill="rgb(0,0,0)" text-anchor="middle" transform="rotate(-90.000000 139.310051,103.098077)" >59 ±1</text> </g>
  Visible = true
  X = 0
  Y = 0
FEATURE [Drawing::FeatureView] dimLine008
  Rotation = 0
  ViewResult = <g   >\n<line x1="68.223944" y1="142.506384" x2="87.979912" y2="114.057790" style="stroke:rgb(0,0,255);stroke-width:0.25" />\n<polygon points="87.979912,114.057790 86.017750,115.130134 86.839120,115.700530 87.660490,116.270926" style="fill:rgb(0,0,255);stroke:rgb(0,0,255);stroke-width:0" />\n<line x1="68.223944" y1="142.506384" x2="10.536516" y2="142.506384" style="stroke:rgb(0,0,255);stroke-width:0.25" />\n</g> 
  Visible = true
  X = 0
  Y = 0
FEATURE [Drawing::FeatureView] dimText015
  Rotation = 0
  ViewResult = <g> <text x="11.590168" y="140.662494" font-family="inherit" font-size="3" fill="rgb(0,0,0)" text-anchor="inherit" transform="rotate(0.000000 11.590168,140.662494)" >Silk screen Enthone 50-700R black</text> </g>
  Visible = true
  X = 0
  Y = 0
FEATURE [Drawing::FeatureView] dimText016
  Rotation = 0
  ViewResult = <g> <text x="11.326755" y="145.667339" font-family="inherit" font-size="2" fill="rgb(0,0,0)" text-anchor="inherit"  >TAZ_silkscreen_Back_LulzBotTAZ6_Octopus_02.svg</text> </g>
  Visible = true
  X = 0
  Y = 0
FEATURE [Drawing::FeatureView] dimLine009
  Rotation = 0
  ViewResult = <g   >\n<line x1="109.052945" y1="159.101397" x2="148.828294" y2="102.731035" style="stroke:rgb(0,0,255);stroke-width:0.25" />\n<polygon points="148.828294,102.731035 146.858154,103.788649 147.675227,104.365182 148.492301,104.941715" style="fill:rgb(0,0,255);stroke:rgb(0,0,255);stroke-width:0" />\n<line x1="109.052945" y1="159.101397" x2="48.467975" y2="159.101397" style="stroke:rgb(0,0,255);stroke-width:0.25" />\n</g> 
  Visible = true
  X = 0
  Y = 0
FEATURE [Drawing::FeatureView] dimText017
  Rotation = 0
  ViewResult = <g> <text x="49.258214" y="157.784333" font-family="inherit" font-size="3" fill="rgb(0,0,0)" text-anchor="inherit" transform="rotate(0.000000 49.258214,157.784333)" >Silk screen PMS 877C metallic silver</text> </g>
  Visible = true
  X = 0
  Y = 0
FEATURE [Drawing::FeatureView] dimText018
  Rotation = 0
  ViewResult = <g> <text x="49.258214" y="162.789178" font-family="inherit" font-size="2" fill="rgb(0,0,0)" text-anchor="inherit"  >TAZ_silkscreen_Back_LulzBotTAZ6_LulzBot_TAZ.svg</text> </g>
  Visible = true
  X = 0
  Y = 0
FEATURE [Drawing::FeatureView] dimLine010
  Rotation = 0
  ViewResult = <g   >\n<line x1="214.418109" y1="59.531318" x2="199.379436" y2="91.670249" style="stroke:rgb(0,0,255);stroke-width:0.25" />\n<polygon points="199.379436,91.670249 201.132826,90.282581 200.227081,89.858758 199.321336,89.434936" style="fill:rgb(0,0,255);stroke:rgb(0,0,255);stroke-width:0" />\n<line x1="214.418109" y1="59.531318" x2="267.627516" y2="59.531318" style="stroke:rgb(0,0,255);stroke-width:0.25" />\n</g> 
  Visible = true
  X = 0
  Y = 0
FEATURE [Drawing::FeatureView] dimText019
  Rotation = 0
  ViewResult = <g> <text x="213.627870" y="57.687427" font-family="inherit" font-size="3" fill="rgb(0,0,0)" text-anchor="inherit" transform="rotate(0.000000 213.627870,57.687427)" >Silk screen PMS 877C metallic silver</text> </g>
  Visible = true
  X = 0
  Y = 0
FEATURE [Drawing::FeatureView] dimText020
  Rotation = 0
  ViewResult = <g> <text x="219.159541" y="63.219098" font-family="inherit" font-size="2" fill="rgb(0,0,0)" text-anchor="inherit" transform="rotate(0.000000 219.159541,63.219098)" >TAZ_silkscreen_Back_LulzBotTAZ6_On_Off.svg</text> </g>
  Visible = true
  X = 0
  Y = 0
FEATURE [Drawing::FeaturePage] Page021  label="Sheet 7"
  EditableTexts = N/A | ELECTRONICS CHASSIS | A | PP-FP0142 | 7 of 8
  Group = -> [View,Symbol,Symbol002,dimText014,grabPoint002,grabPoint003,dim108,dim109,grabPoint004,grabPoint006,grabPoint007,dim110,dim111,dim112,grabPoint005,dim113,grabPoint008,grabPoint009,Symbol003,dim114,dim115,dim116,dimLine008,dimText015,dimText016,dimLine009,dimText017,dimText018,dimLine010,dimText019,dimText020]
  Template = <userpath>/shared-j/Documents/R&D/titleblocks/A4_Landscape_AlephP2.svg
FEATURE [Drawing::FeatureViewSymbol] Symbol004
  Rotation = 90
  Scale = 0.5
  Symbol = <blob: 25927 chars omitted>
  ViewResult = <blob: 25989 chars omitted>
  Visible = true
  X = 110
  Y = 64
FEATURE [Drawing::FeatureViewSymbol] Symbol005
  Rotation = 90
  Scale = 0.5
  Symbol = <blob: 7358 chars omitted>
  ViewResult = <blob: 7420 chars omitted>
  Visible = true
  X = 230
  Y = 51
FEATURE [Drawing::FeatureViewSymbol] Symbol006
  Rotation = 90
  Scale = 0.5
  Symbol = <blob: 17148 chars omitted>
  ViewResult = <blob: 17210 chars omitted>
  Visible = true
  X = 223
  Y = 33
FEATURE [Drawing::FeatureViewSymbol] Symbol007
  Rotation = 90
  Scale = 0.5
  Symbol = <blob: 5576 chars omitted>
  ViewResult = <blob: 5640 chars omitted>
  Visible = true
  X = 275
  Y = 37.5
FEATURE [Drawing::FeatureView] dimText037
  Rotation = 0
  ViewResult = <g> <text x="78.497047" y="176.486650" font-family="inherit" font-size="5" fill="rgb(0,0,0)" text-anchor="inherit" transform="rotate(0.000000 78.497047,176.486650)" >GRAPHICS NOT TO SCALE. FOR REFERENCE ONLY</text> </g>
  Visible = true
  X = 0
  Y = 0
FEATURE [Drawing::FeatureView] grabPoint011
  Rotation = 0
  ViewResult = <g> <line x1="159.101397464" y1="58.4776659553" x2="159.101397464" y2="58.4776659553" style="stroke:rgb(0,0,0);stroke-width:0.01" /> </g> 
  Visible = true
  X = 0
  Y = 0
FEATURE [Drawing::FeatureView] grabPoint012
  Rotation = 0
  ViewResult = <g> <line x1="164.106242748" y1="91.6676925786" x2="164.106242748" y2="91.6676925786" style="stroke:rgb(0,0,0);stroke-width:0.01" /> </g> 
  Visible = true
  X = 0
  Y = 0
FEATURE [Drawing::FeatureView] grabPoint013
  Rotation = 0
  ViewResult = <g> <line x1="197.296269372" y1="63.4825112398" x2="197.296269372" y2="63.4825112398" style="stroke:rgb(0,0,0);stroke-width:0.01" /> </g> 
  Visible = true
  X = 0
  Y = 0
FEATURE [Drawing::FeatureView] dim118
  Rotation = 0
  ViewResult = <g> <line x1="20.000000" y1="55.200000" x2="20.000000" y2="41.409478" style="stroke:rgb(0,0,255);stroke-width:0.25" />\n<line x1="159.101397" y1="56.477620" x2="159.101397" y2="41.409478" style="stroke:rgb(0,0,255);stroke-width:0.25" />\n<line x1="20.000000" y1="42.409478" x2="159.101397" y2="42.409478" style="stroke:rgb(0,0,255);stroke-width:0.25" />\n<polygon points="20.000000,42.409478 22.000000,43.409478 22.000000,42.409478 22.000000,41.409478" style="fill:rgb(0,0,255);stroke:rgb(0,0,255);stroke-width:0" />\n<polygon points="159.101397,42.409478 157.101397,41.409478 157.101397,42.409478 157.101397,43.409478" style="fill:rgb(0,0,255);stroke:rgb(0,0,255);stroke-width:0" />\n<text x="89.550699" y="40.409478" font-family="inherit" font-size="3" fill="rgb(0,0,0)" text-anchor="middle"  >280 ±2</text> </g> 
  Visible = true
  X = 0
  Y = 0
FEATURE [Drawing::FeatureView] dim119
  Rotation = 0
  ViewResult = <g> <line x1="20.000000" y1="55.200000" x2="20.000000" y2="31.399788" style="stroke:rgb(0,0,255);stroke-width:0.25" />\n<line x1="197.296269" y1="61.482465" x2="197.296269" y2="31.399788" style="stroke:rgb(0,0,255);stroke-width:0.25" />\n<line x1="20.000000" y1="32.399788" x2="197.296269" y2="32.399788" style="stroke:rgb(0,0,255);stroke-width:0.25" />\n<polygon points="20.000000,32.399788 22.000000,33.399788 22.000000,32.399788 22.000000,31.399788" style="fill:rgb(0,0,255);stroke:rgb(0,0,255);stroke-width:0" />\n<polygon points="197.296269,32.399788 195.296269,31.399788 195.296269,32.399788 195.296269,33.399788" style="fill:rgb(0,0,255);stroke:rgb(0,0,255);stroke-width:0" />\n<text x="108.648135" y="30.399788" font-family="inherit" font-size="3" fill="rgb(0,0,0)" text-anchor="middle"  >355</text> </g> 
  Visible = true
  X = 0
  Y = 0
FEATURE [Drawing::FeatureView] dim120
  Rotation = 0
  ViewResult = <g> <line x1="20.000000" y1="105.500000" x2="20.000000" y2="116.111442" style="stroke:rgb(0,0,255);stroke-width:0.25" />\n<line x1="164.106243" y1="93.667739" x2="164.106243" y2="116.111442" style="stroke:rgb(0,0,255);stroke-width:0.25" />\n<line x1="20.000000" y1="115.111442" x2="164.106243" y2="115.111442" style="stroke:rgb(0,0,255);stroke-width:0.25" />\n<polygon points="20.000000,115.111442 22.000000,116.111442 22.000000,115.111442 22.000000,114.111442" style="fill:rgb(0,0,255);stroke:rgb(0,0,255);stroke-width:0" />\n<polygon points="164.106243,115.111442 162.106243,114.111442 162.106243,115.111442 162.106243,116.111442" style="fill:rgb(0,0,255);stroke:rgb(0,0,255);stroke-width:0" />\n<text x="92.053121" y="113.111442" font-family="inherit" font-size="3" fill="rgb(0,0,0)" text-anchor="middle"  >290 ±1</text> </g> 
  Visible = true
  X = 0
  Y = 0
FEATURE [Drawing::FeatureView] grabPoint014
  Rotation = 0
  ViewResult = <g> <line x1="199.930398469" y1="62.9556854203" x2="199.930398469" y2="62.9556854203" style="stroke:rgb(0,0,0);stroke-width:0.01" /> </g> 
  Visible = true
  X = 0
  Y = 0
FEATURE [Drawing::FeatureView] dim121
  Rotation = 0
  ViewResult = <g> \n  <line x1="197.296269" y1="61.482511" x2="197.296269" y2="50.498942" style="stroke:rgb(0,0,255);stroke-width:0.25" />\n<line x1="199.930398" y1="60.955685" x2="199.930398" y2="50.498942" style="stroke:rgb(0,0,255);stroke-width:0.25" />\n<line x1="197.296269" y1="51.498942" x2="199.930398" y2="51.498942" style="stroke:rgb(0,0,255);stroke-width:0.25" /> \n  <polygon points="199.930398,51.498942 201.930398,52.498942 201.930398,51.498942 201.930398,50.498942" style="fill:rgb(0,0,255);stroke:rgb(0,0,255);stroke-width:0" /><polygon points="197.296269,51.498942 195.296269,50.498942 195.296269,51.498942 195.296269,52.498942" style="fill:rgb(0,0,255);stroke:rgb(0,0,255);stroke-width:0" /> \n  <text x="200.486492" y="49.389921" font-family="inherit" font-size="3" fill="rgb(0,0,0)" text-anchor="middle"  >3.0</text> </g>
  Visible = true
  X = 0
  Y = 0
FEATURE [Drawing::FeatureView] grabPoint015
  Rotation = 0
  ViewResult = <g> <line x1="53.7296891604" y1="70.654541246" x2="53.7296891604" y2="70.654541246" style="stroke:rgb(0,0,0);stroke-width:0.01" /> </g> 
  Visible = true
  X = 0
  Y = 0
FEATURE [Drawing::FeatureView] grabPoint016
  Rotation = 0
  ViewResult = <g> <line x1="26.4738857399" y1="81.1327162622" x2="26.4738857399" y2="81.1327162622" style="stroke:rgb(0,0,0);stroke-width:0.01" /> </g> 
  Visible = true
  X = 0
  Y = 0
FEATURE [Drawing::FeatureView] dim122
  Rotation = 0
  ViewResult = <g> \n  <line x1="51.729689" y1="70.654541" x2="12.059299" y2="70.654541" style="stroke:rgb(0,0,255);stroke-width:0.25" />\n<line x1="24.473886" y1="81.132716" x2="12.059299" y2="81.132716" style="stroke:rgb(0,0,255);stroke-width:0.25" />\n<line x1="13.059299" y1="70.654541" x2="13.059299" y2="81.132716" style="stroke:rgb(0,0,255);stroke-width:0.25" /> \n  <polygon points="13.059299,81.132716 14.059299,79.132716 13.059299,79.132716 12.059299,79.132716" style="fill:rgb(0,0,255);stroke:rgb(0,0,255);stroke-width:0" /><polygon points="13.059299,70.654541 12.059299,72.654541 13.059299,72.654541 14.059299,72.654541" style="fill:rgb(0,0,255);stroke:rgb(0,0,255);stroke-width:0" /> \n  <text x="11.059299" y="75.893629" font-family="inherit" font-size="3" fill="rgb(0,0,0)" text-anchor="middle" transform="rotate(-90.000000 11.059299,75.893629)" >19 ±1</text> </g>
  Visible = true
  X = 0
  Y = 0
FEATURE [Drawing::FeatureView] grabPoint017
  Rotation = 0
  ViewResult = <g> <line x1="53.5431277397" y1="90.8554118789" x2="53.5431277397" y2="90.8554118789" style="stroke:rgb(0,0,0);stroke-width:0.01" /> </g> 
  Visible = true
  X = 0
  Y = 0
FEATURE [Drawing::FeatureView] dim123
  Rotation = 0
  ViewResult = <g> \n  <line x1="55.729689" y1="70.654541" x2="61.632462" y2="70.654541" style="stroke:rgb(0,0,255);stroke-width:0.25" />\n<line x1="55.543128" y1="90.855412" x2="61.632462" y2="90.855412" style="stroke:rgb(0,0,255);stroke-width:0.25" />\n<line x1="60.632462" y1="70.654541" x2="60.632462" y2="90.855412" style="stroke:rgb(0,0,255);stroke-width:0.25" /> \n  <polygon points="60.632462,90.855412 61.632462,88.855412 60.632462,88.855412 59.632462,88.855412" style="fill:rgb(0,0,255);stroke:rgb(0,0,255);stroke-width:0" /><polygon points="60.632462,70.654541 59.632462,72.654541 60.632462,72.654541 61.632462,72.654541" style="fill:rgb(0,0,255);stroke:rgb(0,0,255);stroke-width:0" /> \n  <text x="58.632462" y="80.754977" font-family="inherit" font-size="3" fill="rgb(0,0,0)" text-anchor="middle" transform="rotate(-90.000000 58.632462,80.754977)" >38 ±1</text> </g>
  Visible = true
  X = 0
  Y = 0
FEATURE [Drawing::FeatureView] grabPoint018
  Rotation = 0
  ViewResult = <g> <line x1="165.106857316" y1="82.4601479476" x2="165.106857316" y2="82.4601479476" style="stroke:rgb(0,0,0);stroke-width:0.01" /> </g> 
  Visible = true
  X = 0
  Y = 0
FEATURE [Drawing::FeatureView] grabPoint019
  Rotation = 0
  ViewResult = <g> <line x1="165.853102999" y1="99.4372372309" x2="165.853102999" y2="99.4372372309" style="stroke:rgb(0,0,0);stroke-width:0.01" /> </g> 
  Visible = true
  X = 0
  Y = 0
FEATURE [Drawing::FeatureView] dim124
  Rotation = 0
  ViewResult = <g> \n  <line x1="183.000000" y1="91.000000" x2="158.883138" y2="91.000000" style="stroke:rgb(0,0,255);stroke-width:0.25" />\n<line x1="163.853103" y1="99.437237" x2="158.883138" y2="99.437237" style="stroke:rgb(0,0,255);stroke-width:0.25" />\n<line x1="159.883138" y1="91.000000" x2="159.883138" y2="99.437237" style="stroke:rgb(0,0,255);stroke-width:0.25" /> \n  <polygon points="159.883138,99.437237 160.883138,97.437237 159.883138,97.437237 158.883138,97.437237" style="fill:rgb(0,0,255);stroke:rgb(0,0,255);stroke-width:0" /><polygon points="159.883138,91.000000 158.883138,93.000000 159.883138,93.000000 160.883138,93.000000" style="fill:rgb(0,0,255);stroke:rgb(0,0,255);stroke-width:0" /> \n  <text x="158.950330" y="107.086255" font-family="inherit" font-size="3" fill="rgb(0,0,0)" text-anchor="middle" transform="rotate(-90.000000 158.950330,107.086255)" >17.5 ±1</text> </g>
  Visible = true
  X = 0
  Y = 0
FEATURE [Drawing::FeatureView] dim125
  Rotation = 0
  ViewResult = <g> \n  <line x1="183.000000" y1="91.000000" x2="158.883138" y2="91.000000" style="stroke:rgb(0,0,255);stroke-width:0.25" />\n<line x1="163.106857" y1="82.460148" x2="158.883138" y2="82.460148" style="stroke:rgb(0,0,255);stroke-width:0.25" />\n<line x1="159.883138" y1="91.000000" x2="159.883138" y2="82.460148" style="stroke:rgb(0,0,255);stroke-width:0.25" /> \n  <polygon points="159.883138,82.460148 158.883138,84.460148 159.883138,84.460148 160.883138,84.460148" style="fill:rgb(0,0,255);stroke:rgb(0,0,255);stroke-width:0" /><polygon points="159.883138,91.000000 160.883138,89.000000 159.883138,89.000000 158.883138,89.000000" style="fill:rgb(0,0,255);stroke:rgb(0,0,255);stroke-width:0" /> \n  <text x="157.830962" y="76.117060" font-family="inherit" font-size="3" fill="rgb(0,0,0)" text-anchor="middle" transform="rotate(-90.000000 157.830962,76.117060)" >17.5 ±1</text> </g>
  Visible = true
  X = 0
  Y = 0
FEATURE [Drawing::FeatureView] dim126
  Rotation = 0
  ViewResult = <g> \n  <line x1="163.106857" y1="82.460148" x2="151.607242" y2="82.460148" style="stroke:rgb(0,0,255);stroke-width:0.25" />\n<line x1="163.853103" y1="99.437237" x2="151.607242" y2="99.437237" style="stroke:rgb(0,0,255);stroke-width:0.25" />\n<line x1="152.607242" y1="82.460148" x2="152.607242" y2="99.437237" style="stroke:rgb(0,0,255);stroke-width:0.25" /> \n  <polygon points="152.607242,99.437237 153.607242,97.437237 152.607242,97.437237 151.607242,97.437237" style="fill:rgb(0,0,255);stroke:rgb(0,0,255);stroke-width:0" /><polygon points="152.607242,82.460148 151.607242,84.460148 152.607242,84.460148 153.607242,84.460148" style="fill:rgb(0,0,255);stroke:rgb(0,0,255);stroke-width:0" /> \n  <text x="150.607242" y="90.948693" font-family="inherit" font-size="3" fill="rgb(0,0,0)" text-anchor="middle" transform="rotate(-90.000000 150.607242,90.948693)" >35.0</text> </g>
  Visible = true
  X = 0
  Y = 0
FEATURE [Drawing::FeatureView] grabPoint020
  Rotation = 0
  ViewResult = <g> <line x1="178.166156765" y1="67.3486728712" x2="178.166156765" y2="67.3486728712" style="stroke:rgb(0,0,0);stroke-width:0.01" /> </g> 
  Visible = true
  X = 0
  Y = 0
FEATURE [Drawing::FeatureView] dim127
  Rotation = 0
  ViewResult = <g> <line x1="180.166394" y1="67.348673" x2="184.203315" y2="67.348673" style="stroke:rgb(0,0,255);stroke-width:0.25" />\n<line x1="183.203315" y1="55.700000" x2="183.203315" y2="67.348673" style="stroke:rgb(0,0,255);stroke-width:0.25" />\n<polygon points="183.203315,55.700000 182.203315,57.700000 183.203315,57.700000 184.203315,57.700000" style="fill:rgb(0,0,255);stroke:rgb(0,0,255);stroke-width:0" />\n<polygon points="183.203315,67.348673 184.203315,65.348673 183.203315,65.348673 182.203315,65.348673" style="fill:rgb(0,0,255);stroke:rgb(0,0,255);stroke-width:0" />\n<text x="181.203315" y="61.524336" font-family="inherit" font-size="3" fill="rgb(0,0,0)" text-anchor="middle" transform="rotate(-90.000000 181.203315,61.524336)" >28 ±2</text> </g> 
  Visible = true
  X = 0
  Y = 0
FEATURE [Drawing::FeatureView] dim128
  Rotation = 0
  ViewResult = <g> \n  <line x1="159.101397" y1="56.477666" x2="159.101397" y2="49.185022" style="stroke:rgb(0,0,255);stroke-width:0.25" />\n<line x1="178.166157" y1="65.348673" x2="178.166157" y2="49.185022" style="stroke:rgb(0,0,255);stroke-width:0.25" />\n<line x1="159.101397" y1="50.185022" x2="178.166157" y2="50.185022" style="stroke:rgb(0,0,255);stroke-width:0.25" /> \n  <polygon points="178.166157,50.185022 176.166157,49.185022 176.166157,50.185022 176.166157,51.185022" style="fill:rgb(0,0,255);stroke:rgb(0,0,255);stroke-width:0" /><polygon points="159.101397,50.185022 161.101397,51.185022 161.101397,50.185022 161.101397,49.185022" style="fill:rgb(0,0,255);stroke:rgb(0,0,255);stroke-width:0" /> \n  <text x="168.633777" y="48.185022" font-family="inherit" font-size="3" fill="rgb(0,0,0)" text-anchor="middle"  >37 ±1</text> </g>
  Visible = true
  X = 0
  Y = 0
FEATURE [Drawing::FeatureView] grabPoint021
  Rotation = 0
  ViewResult = <g> <line x1="199.620720145" y1="97.1985001826" x2="199.620720145" y2="97.1985001826" style="stroke:rgb(0,0,0);stroke-width:0.01" /> </g> 
  Visible = true
  X = 0
  Y = 0
FEATURE [Drawing::FeatureView] grabPoint022
  Rotation = 0
  ViewResult = <g> <line x1="199.807281565" y1="84.6988849959" x2="199.807281565" y2="84.6988849959" style="stroke:rgb(0,0,0);stroke-width:0.01" /> </g> 
  Visible = true
  X = 0
  Y = 0
FEATURE [Drawing::FeatureView] dim129
  Rotation = 0
  ViewResult = <g> \n  <line x1="187.000000" y1="91.000000" x2="205.657879" y2="91.000000" style="stroke:rgb(0,0,255);stroke-width:0.25" />\n<line x1="201.807282" y1="84.698885" x2="205.657879" y2="84.698885" style="stroke:rgb(0,0,255);stroke-width:0.25" />\n<line x1="204.657879" y1="91.000000" x2="204.657879" y2="84.698885" style="stroke:rgb(0,0,255);stroke-width:0.25" /> \n  <polygon points="204.657879,84.698885 203.657879,86.698885 204.657879,86.698885 205.657879,86.698885" style="fill:rgb(0,0,255);stroke:rgb(0,0,255);stroke-width:0" /><polygon points="204.657879,91.000000 205.657879,89.000000 204.657879,89.000000 203.657879,89.000000" style="fill:rgb(0,0,255);stroke:rgb(0,0,255);stroke-width:0" /> \n  <text x="209.321914" y="85.631692" font-family="inherit" font-size="3" fill="rgb(0,0,0)" text-anchor="middle" transform="rotate(-90.000000 209.321914,85.631692)" >12 ±1</text> </g>
  Visible = true
  X = 0
  Y = 0
FEATURE [Drawing::FeatureView] dim130
  Rotation = 0
  ViewResult = <g> \n  <line x1="187.000000" y1="91.000000" x2="205.657879" y2="91.000000" style="stroke:rgb(0,0,255);stroke-width:0.25" />\n<line x1="201.620720" y1="97.198500" x2="205.657879" y2="97.198500" style="stroke:rgb(0,0,255);stroke-width:0.25" />\n<line x1="204.657879" y1="91.000000" x2="204.657879" y2="97.198500" style="stroke:rgb(0,0,255);stroke-width:0.25" /> \n  <polygon points="204.657879,97.198500 205.657879,95.198500 204.657879,95.198500 203.657879,95.198500" style="fill:rgb(0,0,255);stroke:rgb(0,0,255);stroke-width:0" /><polygon points="204.657879,91.000000 203.657879,93.000000 204.657879,93.000000 205.657879,93.000000" style="fill:rgb(0,0,255);stroke:rgb(0,0,255);stroke-width:0" /> \n  <text x="209.321914" y="96.079132" font-family="inherit" font-size="3" fill="rgb(0,0,0)" text-anchor="middle" transform="rotate(-90.000000 209.321914,96.079132)" >12 ±1</text> </g>
  Visible = true
  X = 0
  Y = 0
FEATURE [Drawing::FeatureView] grabPoint023
  Rotation = 0
  ViewResult = <g> <line x1="199.434158724" y1="63.2443216159" x2="199.434158724" y2="63.2443216159" style="stroke:rgb(0,0,0);stroke-width:0.01" /> </g> 
  Visible = true
  X = 0
  Y = 0
FEATURE [Drawing::FeatureView] grabPoint024
  Rotation = 0
  ViewResult = <g> <line x1="199.247597303" y1="67.5352342919" x2="199.247597303" y2="67.5352342919" style="stroke:rgb(0,0,0);stroke-width:0.01" /> </g> 
  Visible = true
  X = 0
  Y = 0
FEATURE [Drawing::FeatureView] grabPoint025
  Rotation = 0
  ViewResult = <g> <line x1="196.262614572" y1="65.669620085" x2="196.262614572" y2="65.669620085" style="stroke:rgb(0,0,0);stroke-width:0.01" /> </g> 
  Visible = true
  X = 0
  Y = 0
FEATURE [Drawing::FeatureView] dim131
  Rotation = 0
  ViewResult = <g> \n  <line x1="198.262615" y1="65.669620" x2="212.543624" y2="65.669620" style="stroke:rgb(0,0,255);stroke-width:0.25" />\n<line x1="201.434159" y1="63.244322" x2="212.543624" y2="63.244322" style="stroke:rgb(0,0,255);stroke-width:0.25" />\n<line x1="211.543624" y1="65.669620" x2="211.543624" y2="63.244322" style="stroke:rgb(0,0,255);stroke-width:0.25" /> \n  <polygon points="211.543624,63.244322 212.543624,61.244322 211.543624,61.244322 210.543624,61.244322" style="fill:rgb(0,0,255);stroke:rgb(0,0,255);stroke-width:0" /><polygon points="211.543624,65.669620 210.543624,67.669620 211.543624,67.669620 212.543624,67.669620" style="fill:rgb(0,0,255);stroke:rgb(0,0,255);stroke-width:0" /> \n  <text x="209.363372" y="56.616209" font-family="inherit" font-size="3" fill="rgb(0,0,0)" text-anchor="middle" transform="rotate(-90.000000 209.363372,56.616209)" >3.75 ±1</text> </g>
  Visible = true
  X = 0
  Y = 0
FEATURE [Drawing::FeatureView] dim132
  Rotation = 0
  ViewResult = <g> \n  <line x1="198.262615" y1="65.669620" x2="217.698145" y2="65.669620" style="stroke:rgb(0,0,255);stroke-width:0.25" />\n<line x1="201.247597" y1="67.535234" x2="217.698145" y2="67.535234" style="stroke:rgb(0,0,255);stroke-width:0.25" />\n<line x1="216.698145" y1="65.669620" x2="216.698145" y2="67.535234" style="stroke:rgb(0,0,255);stroke-width:0.25" /> \n  <polygon points="216.698145,67.535234 215.698145,69.535234 216.698145,69.535234 217.698145,69.535234" style="fill:rgb(0,0,255);stroke:rgb(0,0,255);stroke-width:0" /><polygon points="216.698145,65.669620 217.698145,63.669620 216.698145,63.669620 215.698145,63.669620" style="fill:rgb(0,0,255);stroke:rgb(0,0,255);stroke-width:0" /> \n  <text x="214.416077" y="73.588116" font-family="inherit" font-size="3" fill="rgb(0,0,0)" text-anchor="middle" transform="rotate(-90.000000 214.416077,73.588116)" >3.75 ±1</text> </g>
  Visible = true
  X = 0
  Y = 0
FEATURE [Drawing::FeatureView] dimLine011
  Rotation = 0
  ViewResult = <g   >\n<line x1="208.471194" y1="113.638293" x2="199.620720" y2="97.198500" style="stroke:rgb(0,0,255);stroke-width:0.25" />\n<polygon points="199.620720,97.198500 199.688267,99.433548 200.568777,98.959519 201.449286,98.485491" style="fill:rgb(0,0,255);stroke:rgb(0,0,255);stroke-width:0" />\n<line x1="208.471194" y1="113.638293" x2="261.932235" y2="113.638293" style="stroke:rgb(0,0,255);stroke-width:0.25" />\n</g> 
  Visible = true
  X = 0
  Y = 0
FEATURE [Drawing::FeatureView] dimText040
  Rotation = 0
  ViewResult = <g> <text x="209.277139" y="112.295050" font-family="inherit" font-size="3" fill="rgb(0,0,0)" text-anchor="inherit" transform="rotate(0.000000 209.277139,112.295050)" >Silk screen PMS 877C metallic silver</text> </g>
  Visible = true
  X = 0
  Y = 0
FEATURE [Drawing::FeatureView] dimText041
  Rotation = 0
  ViewResult = <g> <text x="209.814436" y="116.056129" font-family="inherit" font-size="2" fill="rgb(0,0,0)" text-anchor="inherit" transform="rotate(0.000000 209.814436,116.056129)" >TAZ_silkscreen_Back_LulzBotTAZ6_USB_Extruder2.svg</text> </g>
  Visible = true
  X = 0
  Y = 0
FEATURE [Drawing::FeatureView] dimLine012
  Rotation = 0
  ViewResult = <g   >\n<line x1="203.635522" y1="125.458824" x2="178.166157" y2="67.348673" style="stroke:rgb(0,0,255);stroke-width:0.25" />\n<polygon points="178.166157,67.348673 178.053126,69.581882 178.969016,69.180453 179.884906,68.779023" style="fill:rgb(0,0,255);stroke:rgb(0,0,255);stroke-width:0" />\n<line x1="203.635522" y1="125.458824" x2="261.394938" y2="125.458824" style="stroke:rgb(0,0,255);stroke-width:0.25" />\n</g> 
  Visible = true
  X = 0
  Y = 0
FEATURE [Drawing::FeatureView] dimLine013
  Rotation = 0
  ViewResult = <g   >\n<line x1="194.232826" y1="141.846379" x2="165.853103" y2="99.437237" style="stroke:rgb(0,0,255);stroke-width:0.25" />\n<polygon points="165.853103,99.437237 166.134322,101.655551 166.965404,101.099400 167.796486,100.543250" style="fill:rgb(0,0,255);stroke:rgb(0,0,255);stroke-width:0" />\n<line x1="194.232826" y1="141.846379" x2="260.588992" y2="141.846379" style="stroke:rgb(0,0,255);stroke-width:0.25" />\n</g> 
  Visible = true
  X = 0
  Y = 0
FEATURE [Drawing::FeatureView] dimLine014
  Rotation = 0
  ViewResult = <g   >\n<line x1="67.968057" y1="126.802066" x2="53.543128" y2="90.855412" style="stroke:rgb(0,0,255);stroke-width:0.25" />\n<polygon points="53.543128,90.855412 53.359904,93.083961 54.287968,92.711540 55.216032,92.339120" style="fill:rgb(0,0,255);stroke:rgb(0,0,255);stroke-width:0" />\n<line x1="67.968057" y1="126.802066" x2="139.428543" y2="126.802066" style="stroke:rgb(0,0,255);stroke-width:0.25" />\n</g> 
  Visible = true
  X = 0
  Y = 0
FEATURE [Drawing::FeatureView] dimText042
  Rotation = 0
  ViewResult = <g> <text x="204.710116" y="124.115582" font-family="inherit" font-size="3" fill="rgb(0,0,0)" text-anchor="inherit" transform="rotate(0.000000 204.710116,124.115582)" >Silk screen PMS 877C metallic silver</text> </g>
  Visible = true
  X = 0
  Y = 0
FEATURE [Drawing::FeatureView] dimText043
  Rotation = 0
  ViewResult = <g> <text x="198.531201" y="140.234489" font-family="inherit" font-size="3" fill="rgb(0,0,0)" text-anchor="inherit" transform="rotate(0.000000 198.531201,140.234489)" >Silk screen PMS 877C metallic silver</text> </g>
  Visible = true
  X = 0
  Y = 0
FEATURE [Drawing::FeatureView] dimText044
  Rotation = 0
  ViewResult = <g> <text x="74.415619" y="125.458824" font-family="inherit" font-size="3" fill="rgb(0,0,0)" text-anchor="inherit" transform="rotate(0.000000 74.415619,125.458824)" >Silk screen PMS 877C metallic silver</text> </g>
  Visible = true
  X = 0
  Y = 0
FEATURE [Drawing::FeatureView] dimText045
  Rotation = 0
  ViewResult = <g> <text x="214.650108" y="127.876660" font-family="inherit" font-size="2" fill="rgb(0,0,0)" text-anchor="inherit" transform="rotate(0.000000 214.650108,127.876660)" >TAZ_silkscreen_Back_AOLogo.svg</text> </g>
  Visible = true
  X = 0
  Y = 0
FEATURE [Drawing::FeatureView] dimText046
  Rotation = 0
  ViewResult = <g> <text x="199.605795" y="144.264215" font-family="inherit" font-size="2" fill="rgb(0,0,0)" text-anchor="inherit" transform="rotate(0.000000 199.605795,144.264215)" >TAZ_silkscreen_Back_LulzBotTAZ6_sticker_area.svg</text> </g>
  Visible = true
  X = 0
  Y = 0
FEATURE [Drawing::FeatureView] dimText047
  Rotation = 0
  ViewResult = <g> <text x="86.236151" y="129.757199" font-family="inherit" font-size="2" fill="rgb(0,0,0)" text-anchor="inherit" transform="rotate(0.000000 86.236151,129.757199)" >TAZ_silkscreen_Back_Certs.svg</text> </g>
  Visible = true
  X = 0
  Y = 0
FEATURE [Drawing::FeatureView] dimText048
  Rotation = 0
  ViewResult = <g > <text x="115.000000" y="30.399788" font-family="inherit" font-size="2.4" fill="rgb(0,0,0)" text-anchor="end" transform="rotate(0.000000 115.000000,30.399788)" >-1</text> \n <text x="115.000000" y="27.999788" font-family="inherit" font-size="2.4" fill="rgb(0,0,0)" text-anchor="end" transform="rotate(0.000000 115.000000,27.999788)" >+2</text> </g> 
  Visible = true
  X = 0
  Y = 0
FEATURE [Drawing::FeatureView] grabPoint010
  Rotation = 0
  ViewResult = <g> <line x1="45.0" y1="75.0" x2="45.0" y2="75.0" style="stroke:rgb(0,0,0);stroke-width:0.01" /> </g> 
  Visible = true
  X = 0
  Y = 0
FEATURE [Drawing::FeatureView] dim117
  Rotation = 0
  ViewResult = <g> <line x1="20.000000" y1="55.200000" x2="20.000000" y2="49.000000" style="stroke:rgb(0,0,255);stroke-width:0.25" />\n<line x1="45.000000" y1="72.999954" x2="45.000000" y2="49.000000" style="stroke:rgb(0,0,255);stroke-width:0.25" />\n<line x1="20.000000" y1="50.000000" x2="45.000000" y2="50.000000" style="stroke:rgb(0,0,255);stroke-width:0.25" />\n<polygon points="20.000000,50.000000 22.000000,51.000000 22.000000,50.000000 22.000000,49.000000" style="fill:rgb(0,0,255);stroke:rgb(0,0,255);stroke-width:0" />\n<polygon points="45.000000,50.000000 43.000000,49.000000 43.000000,50.000000 43.000000,51.000000" style="fill:rgb(0,0,255);stroke:rgb(0,0,255);stroke-width:0" />\n<text x="32.500000" y="48.000000" font-family="inherit" font-size="3" fill="rgb(0,0,0)" text-anchor="middle"  >50 ±1</text> </g> 
  Visible = true
  X = 0
  Y = 0
FEATURE [Drawing::FeaturePage] Page022  label="Sheet 8"
  EditableTexts = N/A | ELECTRONICS CHASSIS | A | PP-FP0142 | 8 of 8
  Group = -> [Ortho037,Symbol004,Symbol005,Symbol006,Symbol007,dimText037,grabPoint011,grabPoint012,grabPoint013,dim118,dim119,dim120,grabPoint014,dim121,grabPoint015,grabPoint016,dim122,grabPoint017,dim123,grabPoint018,grabPoint019,dim124,dim125,dim126,grabPoint020,dim127,dim128,grabPoint021,grabPoint022,dim129,dim130,grabPoint023,grabPoint024,grabPoint025,dim131,dim132,dimLine011,dimText040,dimText041,+12 more]
  Template = <userpath>/shared-j/Documents/R&D/titleblocks/A4_Landscape_AlephP2.svg
FEATURE [Drawing::FeatureView] dimText049
  Rotation = 0
  ViewResult = <g> <text x="10.000000" y="165.000000" font-family="inherit" font-size="4" fill="rgb(0,0,0)" text-anchor="inherit"  >REV</text> </g>
  Visible = true
  X = 0
  Y = 0
FEATURE [Drawing::FeatureView] dimText050
  Rotation = 0
  ViewResult = <g> <text x="20.000000" y="165.000000" font-family="inherit" font-size="4" fill="rgb(0,0,0)" text-anchor="inherit"  >DATE</text> </g>
  Visible = true
  X = 0
  Y = 0
FEATURE [Drawing::FeatureView] dimText051
  Rotation = 0
  ViewResult = <g> <text x="35.000000" y="165.000000" font-family="inherit" font-size="4" fill="rgb(0,0,0)" text-anchor="inherit"  >INIT</text> </g>
  Visible = true
  X = 0
  Y = 0
FEATURE [Drawing::FeatureView] dimText052
  Rotation = 0
  ViewResult = <g> <text x="45.000000" y="165.000000" font-family="inherit" font-size="4" fill="rgb(0,0,0)" text-anchor="inherit"  >NOTES</text> </g>
  Visible = true
  X = 0
  Y = 0
FEATURE [Drawing::FeatureView] dimText055
  Rotation = 0
  ViewResult = <g> <text x="10.000000" y="170.000000" font-family="inherit" font-size="3" fill="rgb(0,0,0)" text-anchor="inherit" transform="rotate(0.000000 10.000000,170.000000)" >A</text> </g>
  Visible = true
  X = 0
  Y = 0
FEATURE [Drawing::FeatureView] dimText056
  Rotation = 0
  ViewResult = <g> <text x="20.000000" y="170.000000" font-family="inherit" font-size="3" fill="rgb(0,0,0)" text-anchor="inherit" transform="rotate(0.000000 20.000000,170.000000)" >3/12/18</text> </g>
  Visible = true
  X = 0
  Y = 0
FEATURE [Drawing::FeatureView] dimText057
  Rotation = 0
  ViewResult = <g> <text x="35.000000" y="170.000000" font-family="inherit" font-size="3" fill="rgb(0,0,0)" text-anchor="inherit" transform="rotate(0.000000 35.000000,170.000000)" >SAW</text> </g>
  Visible = true
  X = 0
  Y = 0
FEATURE [Drawing::FeatureView] dimText058
  Rotation = 0
  ViewResult = <g> <text x="45.000000" y="170.000000" font-family="inherit" font-size="3" fill="rgb(0,0,0)" text-anchor="inherit"  >Adjusted silk screen dimensions and tolerances pages 7,8</text> </g>
  Visible = true
  X = 0
  Y = 0
FEATURE [Drawing::FeatureView] dim016
  Rotation = 0
  ViewResult = <g> <line x1="230.750000" y1="74.500000" x2="246.000000" y2="74.500000" style="stroke:rgb(0,0,255);stroke-width:0.25" />\n<line x1="233.427524" y1="72.835000" x2="246.000000" y2="72.835000" style="stroke:rgb(0,0,255);stroke-width:0.25" />\n<line x1="245.000000" y1="74.500000" x2="245.000000" y2="72.835000" style="stroke:rgb(0,0,255);stroke-width:0.25" />\n<polygon points="245.000000,74.500000 244.000000,76.500000 245.000000,76.500000 246.000000,76.500000" style="fill:rgb(0,0,255);stroke:rgb(0,0,255);stroke-width:0" />\n<polygon points="245.000000,72.835000 246.000000,70.835000 245.000000,70.835000 244.000000,70.835000" style="fill:rgb(0,0,255);stroke:rgb(0,0,255);stroke-width:0" />\n<text x="245.000000" y="80.000000" font-family="inherit" font-size="3.6" fill="rgb(0,0,255)" text-anchor="middle" transform="rotate(-90.000000 245.000000,80.000000)" >3.70</text> </g> 
  Visible = true
  X = 0
  Y = 0
FEATURE [Drawing::FeatureView] dim025
  Rotation = 0
  ViewResult = <g> <line x1="230.750000" y1="110.770000" x2="246.000000" y2="110.770000" style="stroke:rgb(0,0,255);stroke-width:0.25" />\n<line x1="233.427524" y1="112.435000" x2="246.000000" y2="112.435000" style="stroke:rgb(0,0,255);stroke-width:0.25" />\n<line x1="245.000000" y1="110.770000" x2="245.000000" y2="112.435000" style="stroke:rgb(0,0,255);stroke-width:0.25" />\n<polygon points="245.000000,110.770000 246.000000,108.770000 245.000000,108.770000 244.000000,108.770000" style="fill:rgb(0,0,255);stroke:rgb(0,0,255);stroke-width:0" />\n<polygon points="245.000000,112.435000 244.000000,114.435000 245.000000,114.435000 246.000000,114.435000" style="fill:rgb(0,0,255);stroke:rgb(0,0,255);stroke-width:0" />\n<text x="245.000000" y="105.000000" font-family="inherit" font-size="3.6" fill="rgb(0,0,255)" text-anchor="middle" transform="rotate(-90.000000 245.000000,105.000000)" >3.70</text> </g> 
  Visible = true
  X = 0
  Y = 0
FEATURE [Drawing::FeatureView] dim022
  Rotation = 0
  ViewResult = <g> <line x1="228.750000" y1="72.500000" x2="228.750000" y2="59.000000" style="stroke:rgb(0,0,255);stroke-width:0.25" />\n<line x1="231.427500" y1="70.834964" x2="231.427500" y2="59.000000" style="stroke:rgb(0,0,255);stroke-width:0.25" />\n<line x1="228.750000" y1="60.000000" x2="231.427500" y2="60.000000" style="stroke:rgb(0,0,255);stroke-width:0.25" />\n<polygon points="228.750000,60.000000 226.750000,59.000000 226.750000,60.000000 226.750000,61.000000" style="fill:rgb(0,0,255);stroke:rgb(0,0,255);stroke-width:0" />\n<polygon points="231.427500,60.000000 233.427500,61.000000 233.427500,60.000000 233.427500,59.000000" style="fill:rgb(0,0,255);stroke:rgb(0,0,255);stroke-width:0" />\n<text x="230.088750" y="58.000000" font-family="inherit" font-size="3.6" fill="rgb(0,0,255)" text-anchor="middle"  >5.95</text> </g> 
  Visible = true
  X = 0
  Y = 0
FEATURE [Drawing::FeatureView] dim133
  Rotation = 0
  ViewResult = <g> <line x1="204.855000" y1="72.500000" x2="204.855000" y2="59.000000" style="stroke:rgb(0,0,255);stroke-width:0.25" />\n<line x1="202.177500" y1="70.834964" x2="202.177500" y2="59.000000" style="stroke:rgb(0,0,255);stroke-width:0.25" />\n<line x1="204.855000" y1="60.000000" x2="202.177500" y2="60.000000" style="stroke:rgb(0,0,255);stroke-width:0.25" />\n<polygon points="204.855000,60.000000 206.855000,61.000000 206.855000,60.000000 206.855000,59.000000" style="fill:rgb(0,0,255);stroke:rgb(0,0,255);stroke-width:0" />\n<polygon points="202.177500,60.000000 200.177500,59.000000 200.177500,60.000000 200.177500,61.000000" style="fill:rgb(0,0,255);stroke:rgb(0,0,255);stroke-width:0" />\n<text x="203.516250" y="58.000000" font-family="inherit" font-size="3.6" fill="rgb(0,0,255)" text-anchor="middle"  >5.95</text> </g> 
  Visible = true
  X = 0
  Y = 0
FEATURE [Drawing::FeaturePage] Page017  label="Sheet 3"
  EditableTexts = N/A | ELECTRONICS CHASSIS | A | PP-FP0142 | 3 of 8
  Group = -> [Ortho019,dim009,dim010,dim011,dim012,dim013,dim014,centerLines001,centerLines002,centerLines003,dim015,dim017,dim018,dim019,dim020,dim023,dim026,dim027,dim028,dim029,dim030,dim031,dim032,dim024,dimText009,centerLines021,centerLines022,centerLines023,centerLines024,centerLines025,dim097,text012,text013,dim016,dim025,dim022,dim133]
  Template = <userpath>/shared-j/Documents/R&D/titleblocks/A4_Landscape_AlephP2.svg
FEATURE [Drawing::FeatureView] dimText059
  Rotation = 0
  ViewResult = <g> <text x="45.000000" y="175.000000" font-family="inherit" font-size="3" fill="rgb(0,0,0)" text-anchor="inherit"  >Page 3 Insert locations now feature instead of edge based.</text> </g>
  Visible = true
  X = 0
  Y = 0
FEATURE [Drawing::FeaturePage] Page016  label="Sheet 1"
  EditableTexts = SAW | 12/6/17 | N/A | ELECTRONICS CHASSIS | A | PP-FP0142 | 1 of 8 | 2.03mm AL
  Group = -> [dimText011,dimText012,Ortho012,Ortho014,dimText001,dimText002,dimText003,dimText004,dimText005,dimText006,dimText007,dimText008,dimText035,dimText036,dimText038,dimText039,dimText053,dimText054,dimText049,dimText050,dimText051,dimText052,dimText055,dimText056,dimText057,dimText058,dimText059]
  Template = <userpath>/shared-j/Documents/R&D/titleblocks/A4_Landscape_Aleph.svg
